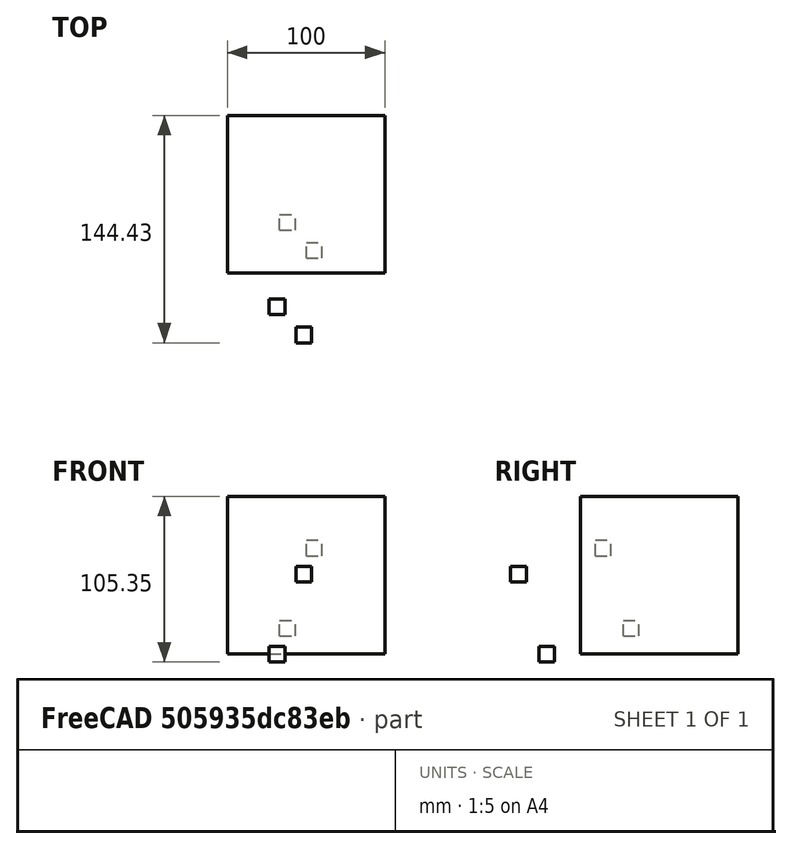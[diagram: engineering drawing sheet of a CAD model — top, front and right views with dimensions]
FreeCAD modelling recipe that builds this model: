
FCSTD DOCUMENT  (FreeCAD 0.20R29603 (Git))
Label: PartArrayPart
License: All rights reserved
LicenseURL: http://en.wikipedia.org/wiki/All_rights_reserved
objects: App::DocumentObjectGroupPython×1251, Part::FeaturePython×3, App::Part×2, Part::Part2DObjectPython×1
note: 4 computed .brp shape members not serialized (recipe doc carries the construction recipe); baked Part::Feature solids carry a one-line shape summary decoded from their .brp

FEATURE [App::DocumentObjectGroupPython] HALFPI  # scripted group (container) (typed FeaturePython)
  name = HALFPI
  value = pi/2.
FEATURE [App::DocumentObjectGroupPython] PI  # scripted group (container) (typed FeaturePython)
  name = PI
  value = 1.*pi
FEATURE [App::DocumentObjectGroupPython] TWOPI  # scripted group (container) (typed FeaturePython)
  name = TWOPI
  value = 2.*pi
FEATURE [App::DocumentObjectGroupPython] Constants  # scripted group (container) (typed FeaturePython)
  Group = -> [HALFPI,PI,TWOPI]
FEATURE [App::DocumentObjectGroupPython] Variables  # scripted group (container) (typed FeaturePython)
FEATURE [App::DocumentObjectGroupPython] Quantities  # scripted group (container) (typed FeaturePython)
FEATURE [App::DocumentObjectGroupPython] Isotopes  # scripted group (container) (typed FeaturePython)
FEATURE [App::DocumentObjectGroupPython] Elements  # scripted group (container) (typed FeaturePython)
FEATURE [App::DocumentObjectGroupPython] Matrix  # scripted group (container) (typed FeaturePython)
FEATURE [App::DocumentObjectGroupPython] Surfaces  # scripted group (container) (typed FeaturePython)
FEATURE [App::DocumentObjectGroupPython] Opticals  # scripted group (container) (typed FeaturePython)
  Group = -> [Matrix,Surfaces]
FEATURE [App::DocumentObjectGroupPython] G4Isotopes  # scripted group (container) (typed FeaturePython)
FEATURE [App::DocumentObjectGroupPython] H_element  # scripted group (container) (typed FeaturePython)
  Z = 1
  atom_value = 1.008
  formula = H
  name = H_element
FEATURE [App::DocumentObjectGroupPython] He_element  # scripted group (container) (typed FeaturePython)
  Z = 2
  atom_value = 4.0026
  formula = He
  name = He_element
FEATURE [App::DocumentObjectGroupPython] Li_element  # scripted group (container) (typed FeaturePython)
  Z = 3
  atom_value = 6.94
  formula = Li
  name = Li_element
FEATURE [App::DocumentObjectGroupPython] Be_element  # scripted group (container) (typed FeaturePython)
  Z = 4
  atom_value = 9.01218
  formula = Be
  name = Be_element
FEATURE [App::DocumentObjectGroupPython] B_element  # scripted group (container) (typed FeaturePython)
  Z = 5
  atom_value = 10.81
  formula = B
  name = B_element
FEATURE [App::DocumentObjectGroupPython] C_element  # scripted group (container) (typed FeaturePython)
  Z = 6
  atom_value = 12.011
  formula = C
  name = C_element
FEATURE [App::DocumentObjectGroupPython] N_element  # scripted group (container) (typed FeaturePython)
  Z = 7
  atom_value = 14.007
  formula = N
  name = N_element
FEATURE [App::DocumentObjectGroupPython] O_element  # scripted group (container) (typed FeaturePython)
  Z = 8
  atom_value = 15.999
  formula = O
  name = O_element
FEATURE [App::DocumentObjectGroupPython] F_element  # scripted group (container) (typed FeaturePython)
  Z = 9
  atom_value = 18.9984
  formula = F
  name = F_element
FEATURE [App::DocumentObjectGroupPython] Ne_element  # scripted group (container) (typed FeaturePython)
  Z = 10
  atom_value = 20.1797
  formula = Ne
  name = Ne_element
FEATURE [App::DocumentObjectGroupPython] Na_element  # scripted group (container) (typed FeaturePython)
  Z = 11
  atom_value = 22.9898
  formula = Na
  name = Na_element
FEATURE [App::DocumentObjectGroupPython] Mg_element  # scripted group (container) (typed FeaturePython)
  Z = 12
  atom_value = 24.305
  formula = Mg
  name = Mg_element
FEATURE [App::DocumentObjectGroupPython] Al_element  # scripted group (container) (typed FeaturePython)
  Z = 13
  atom_value = 26.9815
  formula = Al
  name = Al_element
FEATURE [App::DocumentObjectGroupPython] Si_element  # scripted group (container) (typed FeaturePython)
  Z = 14
  atom_value = 28.085
  formula = Si
  name = Si_element
FEATURE [App::DocumentObjectGroupPython] P_element  # scripted group (container) (typed FeaturePython)
  Z = 15
  atom_value = 30.9738
  formula = P
  name = P_element
FEATURE [App::DocumentObjectGroupPython] S_element  # scripted group (container) (typed FeaturePython)
  Z = 16
  atom_value = 32.06
  formula = S
  name = S_element
FEATURE [App::DocumentObjectGroupPython] Cl_element  # scripted group (container) (typed FeaturePython)
  Z = 17
  atom_value = 35.45
  formula = Cl
  name = Cl_element
FEATURE [App::DocumentObjectGroupPython] Ar_element  # scripted group (container) (typed FeaturePython)
  Z = 18
  atom_value = 39.95
  formula = Ar
  name = Ar_element
FEATURE [App::DocumentObjectGroupPython] K_element  # scripted group (container) (typed FeaturePython)
  Z = 19
  atom_value = 39.0983
  formula = K
  name = K_element
FEATURE [App::DocumentObjectGroupPython] Ca_element  # scripted group (container) (typed FeaturePython)
  Z = 20
  atom_value = 40.078
  formula = Ca
  name = Ca_element
FEATURE [App::DocumentObjectGroupPython] Sc_element  # scripted group (container) (typed FeaturePython)
  Z = 21
  atom_value = 44.9559
  formula = Sc
  name = Sc_element
FEATURE [App::DocumentObjectGroupPython] Ti_element  # scripted group (container) (typed FeaturePython)
  Z = 22
  atom_value = 47.867
  formula = Ti
  name = Ti_element
FEATURE [App::DocumentObjectGroupPython] V_element  # scripted group (container) (typed FeaturePython)
  Z = 23
  atom_value = 50.9415
  formula = V
  name = V_element
FEATURE [App::DocumentObjectGroupPython] Cr_element  # scripted group (container) (typed FeaturePython)
  Z = 24
  atom_value = 51.9961
  formula = Cr
  name = Cr_element
FEATURE [App::DocumentObjectGroupPython] Mn_element  # scripted group (container) (typed FeaturePython)
  Z = 25
  atom_value = 54.938
  formula = Mn
  name = Mn_element
FEATURE [App::DocumentObjectGroupPython] Fe_element  # scripted group (container) (typed FeaturePython)
  Z = 26
  atom_value = 55.845
  formula = Fe
  name = Fe_element
FEATURE [App::DocumentObjectGroupPython] Co_element  # scripted group (container) (typed FeaturePython)
  Z = 27
  atom_value = 58.9332
  formula = Co
  name = Co_element
FEATURE [App::DocumentObjectGroupPython] Ni_element  # scripted group (container) (typed FeaturePython)
  Z = 28
  atom_value = 58.6934
  formula = Ni
  name = Ni_element
FEATURE [App::DocumentObjectGroupPython] Cu_element  # scripted group (container) (typed FeaturePython)
  Z = 29
  atom_value = 63.546
  formula = Cu
  name = Cu_element
FEATURE [App::DocumentObjectGroupPython] Zn_element  # scripted group (container) (typed FeaturePython)
  Z = 30
  atom_value = 65.38
  formula = Zn
  name = Zn_element
FEATURE [App::DocumentObjectGroupPython] Ga_element  # scripted group (container) (typed FeaturePython)
  Z = 31
  atom_value = 69.723
  formula = Ga
  name = Ga_element
FEATURE [App::DocumentObjectGroupPython] Ge_element  # scripted group (container) (typed FeaturePython)
  Z = 32
  atom_value = 72.63
  formula = Ge
  name = Ge_element
FEATURE [App::DocumentObjectGroupPython] As_element  # scripted group (container) (typed FeaturePython)
  Z = 33
  atom_value = 74.9216
  formula = As
  name = As_element
FEATURE [App::DocumentObjectGroupPython] Se_element  # scripted group (container) (typed FeaturePython)
  Z = 34
  atom_value = 78.971
  formula = Se
  name = Se_element
FEATURE [App::DocumentObjectGroupPython] Br_element  # scripted group (container) (typed FeaturePython)
  Z = 35
  atom_value = 79.904
  formula = Br
  name = Br_element
FEATURE [App::DocumentObjectGroupPython] Kr_element  # scripted group (container) (typed FeaturePython)
  Z = 36
  atom_value = 83.798
  formula = Kr
  name = Kr_element
FEATURE [App::DocumentObjectGroupPython] Rb_element  # scripted group (container) (typed FeaturePython)
  Z = 37
  atom_value = 85.4678
  formula = Rb
  name = Rb_element
FEATURE [App::DocumentObjectGroupPython] Sr_element  # scripted group (container) (typed FeaturePython)
  Z = 38
  atom_value = 87.62
  formula = Sr
  name = Sr_element
FEATURE [App::DocumentObjectGroupPython] Y_element  # scripted group (container) (typed FeaturePython)
  Z = 39
  atom_value = 88.9058
  formula = Y
  name = Y_element
FEATURE [App::DocumentObjectGroupPython] Zr_element  # scripted group (container) (typed FeaturePython)
  Z = 40
  atom_value = 91.224
  formula = Zr
  name = Zr_element
FEATURE [App::DocumentObjectGroupPython] Nb_element  # scripted group (container) (typed FeaturePython)
  Z = 41
  atom_value = 92.9064
  formula = Nb
  name = Nb_element
FEATURE [App::DocumentObjectGroupPython] Mo_element  # scripted group (container) (typed FeaturePython)
  Z = 42
  atom_value = 95.95
  formula = Mo
  name = Mo_element
FEATURE [App::DocumentObjectGroupPython] Tc_element  # scripted group (container) (typed FeaturePython)
  Z = 43
  atom_value = 97
  formula = Tc
  name = Tc_element
FEATURE [App::DocumentObjectGroupPython] Ru_element  # scripted group (container) (typed FeaturePython)
  Z = 44
  atom_value = 101.07
  formula = Ru
  name = Ru_element
FEATURE [App::DocumentObjectGroupPython] Rh_element  # scripted group (container) (typed FeaturePython)
  Z = 45
  atom_value = 102.905
  formula = Rh
  name = Rh_element
FEATURE [App::DocumentObjectGroupPython] Pd_element  # scripted group (container) (typed FeaturePython)
  Z = 46
  atom_value = 106.42
  formula = Pd
  name = Pd_element
FEATURE [App::DocumentObjectGroupPython] Ag_element  # scripted group (container) (typed FeaturePython)
  Z = 47
  atom_value = 107.868
  formula = Ag
  name = Ag_element
FEATURE [App::DocumentObjectGroupPython] Cd_element  # scripted group (container) (typed FeaturePython)
  Z = 48
  atom_value = 112.414
  formula = Cd
  name = Cd_element
FEATURE [App::DocumentObjectGroupPython] In_element  # scripted group (container) (typed FeaturePython)
  Z = 49
  atom_value = 114.818
  formula = In
  name = In_element
FEATURE [App::DocumentObjectGroupPython] Sn_element  # scripted group (container) (typed FeaturePython)
  Z = 50
  atom_value = 118.71
  formula = Sn
  name = Sn_element
FEATURE [App::DocumentObjectGroupPython] Sb_element  # scripted group (container) (typed FeaturePython)
  Z = 51
  atom_value = 121.76
  formula = Sb
  name = Sb_element
FEATURE [App::DocumentObjectGroupPython] Te_element  # scripted group (container) (typed FeaturePython)
  Z = 52
  atom_value = 127.6
  formula = Te
  name = Te_element
FEATURE [App::DocumentObjectGroupPython] I_element  # scripted group (container) (typed FeaturePython)
  Z = 53
  atom_value = 126.904
  formula = I
  name = I_element
FEATURE [App::DocumentObjectGroupPython] Xe_element  # scripted group (container) (typed FeaturePython)
  Z = 54
  atom_value = 131.293
  formula = Xe
  name = Xe_element
FEATURE [App::DocumentObjectGroupPython] Cs_element  # scripted group (container) (typed FeaturePython)
  Z = 55
  atom_value = 132.905
  formula = Cs
  name = Cs_element
FEATURE [App::DocumentObjectGroupPython] Ba_element  # scripted group (container) (typed FeaturePython)
  Z = 56
  atom_value = 137.327
  formula = Ba
  name = Ba_element
FEATURE [App::DocumentObjectGroupPython] La_element  # scripted group (container) (typed FeaturePython)
  Z = 57
  atom_value = 138.905
  formula = La
  name = La_element
FEATURE [App::DocumentObjectGroupPython] Ce_element  # scripted group (container) (typed FeaturePython)
  Z = 58
  atom_value = 140.116
  formula = Ce
  name = Ce_element
FEATURE [App::DocumentObjectGroupPython] Pr_element  # scripted group (container) (typed FeaturePython)
  Z = 59
  atom_value = 140.908
  formula = Pr
  name = Pr_element
FEATURE [App::DocumentObjectGroupPython] Nd_element  # scripted group (container) (typed FeaturePython)
  Z = 60
  atom_value = 144.242
  formula = Nd
  name = Nd_element
FEATURE [App::DocumentObjectGroupPython] Pm_element  # scripted group (container) (typed FeaturePython)
  Z = 61
  atom_value = 145
  formula = Pm
  name = Pm_element
FEATURE [App::DocumentObjectGroupPython] Sm_element  # scripted group (container) (typed FeaturePython)
  Z = 62
  atom_value = 150.36
  formula = Sm
  name = Sm_element
FEATURE [App::DocumentObjectGroupPython] Eu_element  # scripted group (container) (typed FeaturePython)
  Z = 63
  atom_value = 151.964
  formula = Eu
  name = Eu_element
FEATURE [App::DocumentObjectGroupPython] Gd_element  # scripted group (container) (typed FeaturePython)
  Z = 64
  atom_value = 157.25
  formula = Gd
  name = Gd_element
FEATURE [App::DocumentObjectGroupPython] Tb_element  # scripted group (container) (typed FeaturePython)
  Z = 65
  atom_value = 158.925
  formula = Tb
  name = Tb_element
FEATURE [App::DocumentObjectGroupPython] Dy_element  # scripted group (container) (typed FeaturePython)
  Z = 66
  atom_value = 162.5
  formula = Dy
  name = Dy_element
FEATURE [App::DocumentObjectGroupPython] Ho_element  # scripted group (container) (typed FeaturePython)
  Z = 67
  atom_value = 164.93
  formula = Ho
  name = Ho_element
FEATURE [App::DocumentObjectGroupPython] Er_element  # scripted group (container) (typed FeaturePython)
  Z = 68
  atom_value = 167.259
  formula = Er
  name = Er_element
FEATURE [App::DocumentObjectGroupPython] Tm_element  # scripted group (container) (typed FeaturePython)
  Z = 69
  atom_value = 168.934
  formula = Tm
  name = Tm_element
FEATURE [App::DocumentObjectGroupPython] Yb_element  # scripted group (container) (typed FeaturePython)
  Z = 70
  atom_value = 173.045
  formula = Yb
  name = Yb_element
FEATURE [App::DocumentObjectGroupPython] Lu_element  # scripted group (container) (typed FeaturePython)
  Z = 71
  atom_value = 174.967
  formula = Lu
  name = Lu_element
FEATURE [App::DocumentObjectGroupPython] Hf_element  # scripted group (container) (typed FeaturePython)
  Z = 72
  atom_value = 178.49
  formula = Hf
  name = Hf_element
FEATURE [App::DocumentObjectGroupPython] Ta_element  # scripted group (container) (typed FeaturePython)
  Z = 73
  atom_value = 180.948
  formula = Ta
  name = Ta_element
FEATURE [App::DocumentObjectGroupPython] W_element  # scripted group (container) (typed FeaturePython)
  Z = 74
  atom_value = 183.84
  formula = W
  name = W_element
FEATURE [App::DocumentObjectGroupPython] Re_element  # scripted group (container) (typed FeaturePython)
  Z = 75
  atom_value = 186.207
  formula = Re
  name = Re_element
FEATURE [App::DocumentObjectGroupPython] Os_element  # scripted group (container) (typed FeaturePython)
  Z = 76
  atom_value = 190.23
  formula = Os
  name = Os_element
FEATURE [App::DocumentObjectGroupPython] Ir_element  # scripted group (container) (typed FeaturePython)
  Z = 77
  atom_value = 192.217
  formula = Ir
  name = Ir_element
FEATURE [App::DocumentObjectGroupPython] Pt_element  # scripted group (container) (typed FeaturePython)
  Z = 78
  atom_value = 195.084
  formula = Pt
  name = Pt_element
FEATURE [App::DocumentObjectGroupPython] Au_element  # scripted group (container) (typed FeaturePython)
  Z = 79
  atom_value = 196.967
  formula = Au
  name = Au_element
FEATURE [App::DocumentObjectGroupPython] Hg_element  # scripted group (container) (typed FeaturePython)
  Z = 80
  atom_value = 200.592
  formula = Hg
  name = Hg_element
FEATURE [App::DocumentObjectGroupPython] Tl_element  # scripted group (container) (typed FeaturePython)
  Z = 81
  atom_value = 204.38
  formula = Tl
  name = Tl_element
FEATURE [App::DocumentObjectGroupPython] Pb_element  # scripted group (container) (typed FeaturePython)
  Z = 82
  atom_value = 207.2
  formula = Pb
  name = Pb_element
FEATURE [App::DocumentObjectGroupPython] Bi_element  # scripted group (container) (typed FeaturePython)
  Z = 83
  atom_value = 208.98
  formula = Bi
  name = Bi_element
FEATURE [App::DocumentObjectGroupPython] Po_element  # scripted group (container) (typed FeaturePython)
  Z = 84
  atom_value = 209
  formula = Po
  name = Po_element
FEATURE [App::DocumentObjectGroupPython] At_element  # scripted group (container) (typed FeaturePython)
  Z = 85
  atom_value = 210
  formula = At
  name = At_element
FEATURE [App::DocumentObjectGroupPython] Rn_element  # scripted group (container) (typed FeaturePython)
  Z = 86
  atom_value = 222
  formula = Rn
  name = Rn_element
FEATURE [App::DocumentObjectGroupPython] Fr_element  # scripted group (container) (typed FeaturePython)
  Z = 87
  atom_value = 223
  formula = Fr
  name = Fr_element
FEATURE [App::DocumentObjectGroupPython] Ra_element  # scripted group (container) (typed FeaturePython)
  Z = 88
  atom_value = 226
  formula = Ra
  name = Ra_element
FEATURE [App::DocumentObjectGroupPython] Ac_element  # scripted group (container) (typed FeaturePython)
  Z = 89
  atom_value = 227
  formula = Ac
  name = Ac_element
FEATURE [App::DocumentObjectGroupPython] Th_element  # scripted group (container) (typed FeaturePython)
  Z = 90
  atom_value = 232.038
  formula = Th
  name = Th_element
FEATURE [App::DocumentObjectGroupPython] Pa_element  # scripted group (container) (typed FeaturePython)
  Z = 91
  atom_value = 231.036
  formula = Pa
  name = Pa_element
FEATURE [App::DocumentObjectGroupPython] U_element  # scripted group (container) (typed FeaturePython)
  Z = 92
  atom_value = 238.029
  formula = U
  name = U_element
FEATURE [App::DocumentObjectGroupPython] Np_element  # scripted group (container) (typed FeaturePython)
  Z = 93
  atom_value = 237
  formula = Np
  name = Np_element
FEATURE [App::DocumentObjectGroupPython] Pu_element  # scripted group (container) (typed FeaturePython)
  Z = 94
  atom_value = 244
  formula = Pu
  name = Pu_element
FEATURE [App::DocumentObjectGroupPython] Am_element  # scripted group (container) (typed FeaturePython)
  Z = 95
  atom_value = 243
  formula = Am
  name = Am_element
FEATURE [App::DocumentObjectGroupPython] Cm_element  # scripted group (container) (typed FeaturePython)
  Z = 96
  atom_value = 247
  formula = Cm
  name = Cm_element
FEATURE [App::DocumentObjectGroupPython] Bk_element  # scripted group (container) (typed FeaturePython)
  Z = 97
  atom_value = 247
  formula = Bk
  name = Bk_element
FEATURE [App::DocumentObjectGroupPython] Cf_element  # scripted group (container) (typed FeaturePython)
  Z = 98
  atom_value = 251
  formula = Cf
  name = Cf_element
FEATURE [App::DocumentObjectGroupPython] G4Elements  # scripted group (container) (typed FeaturePython)
  Group = -> [H_element,He_element,Li_element,Be_element,B_element,C_element,N_element,O_element,F_element,Ne_element,Na_element,Mg_element,Al_element,Si_element,P_element,S_element,Cl_element,Ar_element,K_element,Ca_element,Sc_element,Ti_element,V_element,Cr_element,Mn_element,Fe_element,Co_element,Ni_element,Cu_element,Zn_element,Ga_element,Ge_element,As_element,Se_element,Br_element,Kr_element,Rb_element,+61 more]
FEATURE [App::DocumentObjectGroupPython] H_element001  label="H_element : 0.101"  # scripted group (container) (typed FeaturePython)
  n = 0.101327
FEATURE [App::DocumentObjectGroupPython] C_element001  label="C_element : 0.775"  # scripted group (container) (typed FeaturePython)
  n = 0.7755
FEATURE [App::DocumentObjectGroupPython] N_element001  label="N_element : 0.035"  # scripted group (container) (typed FeaturePython)
  n = 0.035057
FEATURE [App::DocumentObjectGroupPython] O_element001  label="O_element : 0.052"  # scripted group (container) (typed FeaturePython)
  n = 0.0523159
FEATURE [App::DocumentObjectGroupPython] F_element001  label="F_element : 0.017"  # scripted group (container) (typed FeaturePython)
  n = 0.017422
FEATURE [App::DocumentObjectGroupPython] Ca_element001  label="Ca_element : 0.018"  # scripted group (container) (typed FeaturePython)
  n = 0.018378
FEATURE [App::DocumentObjectGroupPython] G4_A_150_TISSUE  label="G4_A-150_TISSUE"  # scripted group (container) (typed FeaturePython)
  Dunit = g/cm3
  Dvalue = 1.127
  Group = -> [H_element001,C_element001,N_element001,O_element001,F_element001,Ca_element001]
  conduct = 2
  density = 1
  expand = 3
  formula = G4_A-150_TISSUE
  name = G4_A-150_TISSUE
  specific = 4
FEATURE [App::DocumentObjectGroupPython] C_element002  label="C_element : 3"  # scripted group (container) (typed FeaturePython)
  n = 3
  ref = C_element
FEATURE [App::DocumentObjectGroupPython] H_element002  label="H_element : 6"  # scripted group (container) (typed FeaturePython)
  n = 6
  ref = H_element
FEATURE [App::DocumentObjectGroupPython] O_element002  label="O_element : 1"  # scripted group (container) (typed FeaturePython)
  n = 1
  ref = O_element
FEATURE [App::DocumentObjectGroupPython] G4_ACETONE  # scripted group (container) (typed FeaturePython)
  Dunit = g/cm3
  Dvalue = 0.7899
  Group = -> [C_element002,H_element002,O_element002]
  conduct = 2
  density = 1
  expand = 3
  formula = G4_ACETONE
  name = G4_ACETONE
  specific = 4
FEATURE [App::DocumentObjectGroupPython] C_element003  label="C_element : 2"  # scripted group (container) (typed FeaturePython)
  n = 2
  ref = C_element
FEATURE [App::DocumentObjectGroupPython] H_element003  label="H_element : 2"  # scripted group (container) (typed FeaturePython)
  n = 2
  ref = H_element
FEATURE [App::DocumentObjectGroupPython] G4_ACETYLENE  # scripted group (container) (typed FeaturePython)
  Dunit = g/cm3
  Dvalue = 0.0010967
  Group = -> [C_element003,H_element003]
  conduct = 2
  density = 1
  expand = 3
  formula = G4_ACETYLENE
  name = G4_ACETYLENE
  specific = 4
FEATURE [App::DocumentObjectGroupPython] C_element004  label="C_element : 5"  # scripted group (container) (typed FeaturePython)
  n = 5
  ref = C_element
FEATURE [App::DocumentObjectGroupPython] H_element004  label="H_element : 5"  # scripted group (container) (typed FeaturePython)
  n = 5
  ref = H_element
FEATURE [App::DocumentObjectGroupPython] N_element002  label="N_element : 5"  # scripted group (container) (typed FeaturePython)
  n = 5
  ref = N_element
FEATURE [App::DocumentObjectGroupPython] G4_ADENINE  # scripted group (container) (typed FeaturePython)
  Dunit = g/cm3
  Dvalue = 1.6
  Group = -> [C_element004,H_element004,N_element002]
  conduct = 2
  density = 1
  expand = 3
  formula = G4_ADENINE
  name = G4_ADENINE
  specific = 4
FEATURE [App::DocumentObjectGroupPython] H_element005  label="H_element : 0.114"  # scripted group (container) (typed FeaturePython)
  n = 0.114
FEATURE [App::DocumentObjectGroupPython] C_element005  label="C_element : 0.598"  # scripted group (container) (typed FeaturePython)
  n = 0.598
FEATURE [App::DocumentObjectGroupPython] N_element003  label="N_element : 0.007"  # scripted group (container) (typed FeaturePython)
  n = 0.007
FEATURE [App::DocumentObjectGroupPython] O_element003  label="O_element : 0.278"  # scripted group (container) (typed FeaturePython)
  n = 0.278
FEATURE [App::DocumentObjectGroupPython] Na_element001  label="Na_element : 0.001"  # scripted group (container) (typed FeaturePython)
  n = 0.001
FEATURE [App::DocumentObjectGroupPython] S_element001  label="S_element : 0.001"  # scripted group (container) (typed FeaturePython)
  n = 0.001
FEATURE [App::DocumentObjectGroupPython] Cl_element001  label="Cl_element : 0.001"  # scripted group (container) (typed FeaturePython)
  n = 0.001
FEATURE [App::DocumentObjectGroupPython] G4_ADIPOSE_TISSUE_ICRP  # scripted group (container) (typed FeaturePython)
  Dunit = g/cm3
  Dvalue = 0.95
  Group = -> [H_element005,C_element005,N_element003,O_element003,Na_element001,S_element001,Cl_element001]
  conduct = 2
  density = 1
  expand = 3
  formula = G4_ADIPOSE_TISSUE_ICRP
  name = G4_ADIPOSE_TISSUE_ICRP
  specific = 4
FEATURE [App::DocumentObjectGroupPython] C_element006  label="C_element : 0.000"  # scripted group (container) (typed FeaturePython)
  n = 0.000124
FEATURE [App::DocumentObjectGroupPython] N_element004  label="N_element : 0.755"  # scripted group (container) (typed FeaturePython)
  n = 0.755268
FEATURE [App::DocumentObjectGroupPython] O_element004  label="O_element : 0.232"  # scripted group (container) (typed FeaturePython)
  n = 0.231781
FEATURE [App::DocumentObjectGroupPython] Ar_element001  label="Ar_element : 0.013"  # scripted group (container) (typed FeaturePython)
  n = 0.012827
FEATURE [App::DocumentObjectGroupPython] G4_AIR  # scripted group (container) (typed FeaturePython)
  Dunit = g/cm3
  Dvalue = 0.00120479
  Group = -> [C_element006,N_element004,O_element004,Ar_element001]
  conduct = 2
  density = 1
  expand = 3
  formula = G4_AIR
  name = G4_AIR
  specific = 4
FEATURE [App::DocumentObjectGroupPython] C_element007  label="C_element : 006"  # scripted group (container) (typed FeaturePython)
  n = 3
  ref = C_element
FEATURE [App::DocumentObjectGroupPython] H_element006  label="H_element : 7"  # scripted group (container) (typed FeaturePython)
  n = 7
  ref = H_element
FEATURE [App::DocumentObjectGroupPython] N_element005  label="N_element : 1"  # scripted group (container) (typed FeaturePython)
  n = 1
  ref = N_element
FEATURE [App::DocumentObjectGroupPython] O_element005  label="O_element : 2"  # scripted group (container) (typed FeaturePython)
  n = 2
  ref = O_element
FEATURE [App::DocumentObjectGroupPython] G4_ALANINE  # scripted group (container) (typed FeaturePython)
  Dunit = g/cm3
  Dvalue = 1.42
  Group = -> [C_element007,H_element006,N_element005,O_element005]
  conduct = 2
  density = 1
  expand = 3
  formula = G4_ALANINE
  name = G4_ALANINE
  specific = 4
FEATURE [App::DocumentObjectGroupPython] Al_element001  label="Al_element : 2"  # scripted group (container) (typed FeaturePython)
  n = 2
  ref = Al_element
FEATURE [App::DocumentObjectGroupPython] O_element006  label="O_element : 3"  # scripted group (container) (typed FeaturePython)
  n = 3
  ref = O_element
FEATURE [App::DocumentObjectGroupPython] G4_ALUMINUM_OXIDE  # scripted group (container) (typed FeaturePython)
  Dunit = g/cm3
  Dvalue = 3.97
  Group = -> [Al_element001,O_element006]
  conduct = 2
  density = 1
  expand = 3
  formula = G4_ALUMINUM_OXIDE
  name = G4_ALUMINUM_OXIDE
  specific = 4
FEATURE [App::DocumentObjectGroupPython] H_element007  label="H_element : 0.106"  # scripted group (container) (typed FeaturePython)
  n = 0.10593
FEATURE [App::DocumentObjectGroupPython] C_element008  label="C_element : 0.789"  # scripted group (container) (typed FeaturePython)
  n = 0.788974
FEATURE [App::DocumentObjectGroupPython] O_element007  label="O_element : 0.105"  # scripted group (container) (typed FeaturePython)
  n = 0.105096
FEATURE [App::DocumentObjectGroupPython] G4_AMBER  # scripted group (container) (typed FeaturePython)
  Dunit = g/cm3
  Dvalue = 1.1
  Group = -> [H_element007,C_element008,O_element007]
  conduct = 2
  density = 1
  expand = 3
  formula = G4_AMBER
  name = G4_AMBER
  specific = 4
FEATURE [App::DocumentObjectGroupPython] N_element006  label="N_element : 006"  # scripted group (container) (typed FeaturePython)
  n = 1
  ref = N_element
FEATURE [App::DocumentObjectGroupPython] H_element008  label="H_element : 3"  # scripted group (container) (typed FeaturePython)
  n = 3
  ref = H_element
FEATURE [App::DocumentObjectGroupPython] G4_AMMONIA  # scripted group (container) (typed FeaturePython)
  Dunit = g/cm3
  Dvalue = 0.000826019
  Group = -> [N_element006,H_element008]
  conduct = 2
  density = 1
  expand = 3
  formula = G4_AMMONIA
  name = G4_AMMONIA
  specific = 4
FEATURE [App::DocumentObjectGroupPython] C_element009  label="C_element : 6"  # scripted group (container) (typed FeaturePython)
  n = 6
  ref = C_element
FEATURE [App::DocumentObjectGroupPython] H_element009  label="H_element : 008"  # scripted group (container) (typed FeaturePython)
  n = 7
  ref = H_element
FEATURE [App::DocumentObjectGroupPython] N_element007  label="N_element : 007"  # scripted group (container) (typed FeaturePython)
  n = 1
  ref = N_element
FEATURE [App::DocumentObjectGroupPython] G4_ANILINE  # scripted group (container) (typed FeaturePython)
  Dunit = g/cm3
  Dvalue = 1.0235
  Group = -> [C_element009,H_element009,N_element007]
  conduct = 2
  density = 1
  expand = 3
  formula = G4_ANILINE
  name = G4_ANILINE
  specific = 4
FEATURE [App::DocumentObjectGroupPython] C_element010  label="C_element : 14"  # scripted group (container) (typed FeaturePython)
  n = 14
  ref = C_element
FEATURE [App::DocumentObjectGroupPython] H_element010  label="H_element : 10"  # scripted group (container) (typed FeaturePython)
  n = 10
  ref = H_element
FEATURE [App::DocumentObjectGroupPython] G4_ANTHRACENE  # scripted group (container) (typed FeaturePython)
  Dunit = g/cm3
  Dvalue = 1.283
  Group = -> [C_element010,H_element010]
  conduct = 2
  density = 1
  expand = 3
  formula = G4_ANTHRACENE
  name = G4_ANTHRACENE
  specific = 4
FEATURE [App::DocumentObjectGroupPython] H_element011  label="H_element : 0.065"  # scripted group (container) (typed FeaturePython)
  n = 0.0654709
FEATURE [App::DocumentObjectGroupPython] C_element011  label="C_element : 0.537"  # scripted group (container) (typed FeaturePython)
  n = 0.536944
FEATURE [App::DocumentObjectGroupPython] N_element008  label="N_element : 0.021"  # scripted group (container) (typed FeaturePython)
  n = 0.0215
FEATURE [App::DocumentObjectGroupPython] O_element008  label="O_element : 0.032"  # scripted group (container) (typed FeaturePython)
  n = 0.032085
FEATURE [App::DocumentObjectGroupPython] F_element002  label="F_element : 0.167"  # scripted group (container) (typed FeaturePython)
  n = 0.167411
FEATURE [App::DocumentObjectGroupPython] Ca_element002  label="Ca_element : 0.177"  # scripted group (container) (typed FeaturePython)
  n = 0.176589
FEATURE [App::DocumentObjectGroupPython] G4_B_100_BONE  label="G4_B-100_BONE"  # scripted group (container) (typed FeaturePython)
  Dunit = g/cm3
  Dvalue = 1.45
  Group = -> [H_element011,C_element011,N_element008,O_element008,F_element002,Ca_element002]
  conduct = 2
  density = 1
  expand = 3
  formula = G4_B-100_BONE
  name = G4_B-100_BONE
  specific = 4
FEATURE [App::DocumentObjectGroupPython] H_element012  label="H_element : 0.057"  # scripted group (container) (typed FeaturePython)
  n = 0.057441
FEATURE [App::DocumentObjectGroupPython] C_element012  label="C_element : 0.790"  # scripted group (container) (typed FeaturePython)
  n = 0.774591
FEATURE [App::DocumentObjectGroupPython] O_element009  label="O_element : 0.168"  # scripted group (container) (typed FeaturePython)
  n = 0.167968
FEATURE [App::DocumentObjectGroupPython] G4_BAKELITE  # scripted group (container) (typed FeaturePython)
  Dunit = g/cm3
  Dvalue = 1.25
  Group = -> [H_element012,C_element012,O_element009]
  conduct = 2
  density = 1
  expand = 3
  formula = G4_BAKELITE
  name = G4_BAKELITE
  specific = 4
FEATURE [App::DocumentObjectGroupPython] Ba_element001  label="Ba_element : 1"  # scripted group (container) (typed FeaturePython)
  n = 1
  ref = Ba_element
FEATURE [App::DocumentObjectGroupPython] F_element003  label="F_element : 2"  # scripted group (container) (typed FeaturePython)
  n = 2
  ref = F_element
FEATURE [App::DocumentObjectGroupPython] G4_BARIUM_FLUORIDE  # scripted group (container) (typed FeaturePython)
  Dunit = g/cm3
  Dvalue = 4.89
  Group = -> [Ba_element001,F_element003]
  conduct = 2
  density = 1
  expand = 3
  formula = G4_BARIUM_FLUORIDE
  name = G4_BARIUM_FLUORIDE
  specific = 4
FEATURE [App::DocumentObjectGroupPython] Ba_element002  label="Ba_element : 002"  # scripted group (container) (typed FeaturePython)
  n = 1
  ref = Ba_element
FEATURE [App::DocumentObjectGroupPython] S_element002  label="S_element : 1"  # scripted group (container) (typed FeaturePython)
  n = 1
  ref = S_element
FEATURE [App::DocumentObjectGroupPython] O_element010  label="O_element : 4"  # scripted group (container) (typed FeaturePython)
  n = 4
  ref = O_element
FEATURE [App::DocumentObjectGroupPython] G4_BARIUM_SULFATE  # scripted group (container) (typed FeaturePython)
  Dunit = g/cm3
  Dvalue = 4.5
  Group = -> [Ba_element002,S_element002,O_element010]
  conduct = 2
  density = 1
  expand = 3
  formula = G4_BARIUM_SULFATE
  name = G4_BARIUM_SULFATE
  specific = 4
FEATURE [App::DocumentObjectGroupPython] C_element013  label="C_element : 007"  # scripted group (container) (typed FeaturePython)
  n = 6
  ref = C_element
FEATURE [App::DocumentObjectGroupPython] H_element013  label="H_element : 009"  # scripted group (container) (typed FeaturePython)
  n = 6
  ref = H_element
FEATURE [App::DocumentObjectGroupPython] G4_BENZENE  # scripted group (container) (typed FeaturePython)
  Dunit = g/cm3
  Dvalue = 0.87865
  Group = -> [C_element013,H_element013]
  conduct = 2
  density = 1
  expand = 3
  formula = G4_BENZENE
  name = G4_BENZENE
  specific = 4
FEATURE [App::DocumentObjectGroupPython] Be_element001  label="Be_element : 1"  # scripted group (container) (typed FeaturePython)
  n = 1
  ref = Be_element
FEATURE [App::DocumentObjectGroupPython] O_element011  label="O_element : 005"  # scripted group (container) (typed FeaturePython)
  n = 1
  ref = O_element
FEATURE [App::DocumentObjectGroupPython] G4_BERYLLIUM_OXIDE  # scripted group (container) (typed FeaturePython)
  Dunit = g/cm3
  Dvalue = 3.01
  Group = -> [Be_element001,O_element011]
  conduct = 2
  density = 1
  expand = 3
  formula = G4_BERYLLIUM_OXIDE
  name = G4_BERYLLIUM_OXIDE
  specific = 4
FEATURE [App::DocumentObjectGroupPython] Bi_element001  label="Bi_element : 4"  # scripted group (container) (typed FeaturePython)
  n = 4
  ref = Bi_element
FEATURE [App::DocumentObjectGroupPython] Ge_element001  label="Ge_element : 3"  # scripted group (container) (typed FeaturePython)
  n = 3
  ref = Ge_element
FEATURE [App::DocumentObjectGroupPython] O_element012  label="O_element : 12"  # scripted group (container) (typed FeaturePython)
  n = 12
  ref = O_element
FEATURE [App::DocumentObjectGroupPython] G4_BGO  # scripted group (container) (typed FeaturePython)
  Dunit = g/cm3
  Dvalue = 7.13
  Group = -> [Bi_element001,Ge_element001,O_element012]
  conduct = 2
  density = 1
  expand = 3
  formula = G4_BGO
  name = G4_BGO
  specific = 4
FEATURE [App::DocumentObjectGroupPython] H_element014  label="H_element : 0.102"  # scripted group (container) (typed FeaturePython)
  n = 0.102
FEATURE [App::DocumentObjectGroupPython] C_element014  label="C_element : 0.110"  # scripted group (container) (typed FeaturePython)
  n = 0.11
FEATURE [App::DocumentObjectGroupPython] N_element009  label="N_element : 0.033"  # scripted group (container) (typed FeaturePython)
  n = 0.033
FEATURE [App::DocumentObjectGroupPython] O_element013  label="O_element : 0.745"  # scripted group (container) (typed FeaturePython)
  n = 0.745
FEATURE [App::DocumentObjectGroupPython] Na_element002  label="Na_element : 0.002"  # scripted group (container) (typed FeaturePython)
  n = 0.001
FEATURE [App::DocumentObjectGroupPython] P_element001  label="P_element : 0.001"  # scripted group (container) (typed FeaturePython)
  n = 0.001
FEATURE [App::DocumentObjectGroupPython] S_element003  label="S_element : 0.002"  # scripted group (container) (typed FeaturePython)
  n = 0.002
FEATURE [App::DocumentObjectGroupPython] Cl_element002  label="Cl_element : 0.003"  # scripted group (container) (typed FeaturePython)
  n = 0.003
FEATURE [App::DocumentObjectGroupPython] K_element001  label="K_element : 0.002"  # scripted group (container) (typed FeaturePython)
  n = 0.002
FEATURE [App::DocumentObjectGroupPython] Fe_element001  label="Fe_element : 0.001"  # scripted group (container) (typed FeaturePython)
  n = 0.001
FEATURE [App::DocumentObjectGroupPython] G4_BLOOD_ICRP  # scripted group (container) (typed FeaturePython)
  Dunit = g/cm3
  Dvalue = 1.06
  Group = -> [H_element014,C_element014,N_element009,O_element013,Na_element002,P_element001,S_element003,Cl_element002,K_element001,Fe_element001]
  conduct = 2
  density = 1
  expand = 3
  formula = G4_BLOOD_ICRP
  name = G4_BLOOD_ICRP
  specific = 4
FEATURE [App::DocumentObjectGroupPython] H_element015  label="H_element : 0.064"  # scripted group (container) (typed FeaturePython)
  n = 0.064
FEATURE [App::DocumentObjectGroupPython] C_element015  label="C_element : 0.278"  # scripted group (container) (typed FeaturePython)
  n = 0.278
FEATURE [App::DocumentObjectGroupPython] N_element010  label="N_element : 0.027"  # scripted group (container) (typed FeaturePython)
  n = 0.027
FEATURE [App::DocumentObjectGroupPython] O_element014  label="O_element : 0.410"  # scripted group (container) (typed FeaturePython)
  n = 0.41
FEATURE [App::DocumentObjectGroupPython] Mg_element001  label="Mg_element : 0.002"  # scripted group (container) (typed FeaturePython)
  n = 0.002
FEATURE [App::DocumentObjectGroupPython] P_element002  label="P_element : 0.070"  # scripted group (container) (typed FeaturePython)
  n = 0.07
FEATURE [App::DocumentObjectGroupPython] S_element004  label="S_element : 0.003"  # scripted group (container) (typed FeaturePython)
  n = 0.002
FEATURE [App::DocumentObjectGroupPython] Ca_element003  label="Ca_element : 0.147"  # scripted group (container) (typed FeaturePython)
  n = 0.147
FEATURE [App::DocumentObjectGroupPython] G4_BONE_COMPACT_ICRU  # scripted group (container) (typed FeaturePython)
  Dunit = g/cm3
  Dvalue = 1.85
  Group = -> [H_element015,C_element015,N_element010,O_element014,Mg_element001,P_element002,S_element004,Ca_element003]
  conduct = 2
  density = 1
  expand = 3
  formula = G4_BONE_COMPACT_ICRU
  name = G4_BONE_COMPACT_ICRU
  specific = 4
FEATURE [App::DocumentObjectGroupPython] H_element016  label="H_element : 0.034"  # scripted group (container) (typed FeaturePython)
  n = 0.034
FEATURE [App::DocumentObjectGroupPython] C_element016  label="C_element : 0.155"  # scripted group (container) (typed FeaturePython)
  n = 0.155
FEATURE [App::DocumentObjectGroupPython] N_element011  label="N_element : 0.042"  # scripted group (container) (typed FeaturePython)
  n = 0.042
FEATURE [App::DocumentObjectGroupPython] O_element015  label="O_element : 0.435"  # scripted group (container) (typed FeaturePython)
  n = 0.435
FEATURE [App::DocumentObjectGroupPython] Na_element003  label="Na_element : 0.003"  # scripted group (container) (typed FeaturePython)
  n = 0.001
FEATURE [App::DocumentObjectGroupPython] Mg_element002  label="Mg_element : 0.003"  # scripted group (container) (typed FeaturePython)
  n = 0.002
FEATURE [App::DocumentObjectGroupPython] P_element003  label="P_element : 0.103"  # scripted group (container) (typed FeaturePython)
  n = 0.103
FEATURE [App::DocumentObjectGroupPython] S_element005  label="S_element : 0.004"  # scripted group (container) (typed FeaturePython)
  n = 0.003
FEATURE [App::DocumentObjectGroupPython] Ca_element004  label="Ca_element : 0.225"  # scripted group (container) (typed FeaturePython)
  n = 0.225
FEATURE [App::DocumentObjectGroupPython] G4_BONE_CORTICAL_ICRP  # scripted group (container) (typed FeaturePython)
  Dunit = g/cm3
  Dvalue = 1.92
  Group = -> [H_element016,C_element016,N_element011,O_element015,Na_element003,Mg_element002,P_element003,S_element005,Ca_element004]
  conduct = 2
  density = 1
  expand = 3
  formula = G4_BONE_CORTICAL_ICRP
  name = G4_BONE_CORTICAL_ICRP
  specific = 4
FEATURE [App::DocumentObjectGroupPython] B_element001  label="B_element : 4"  # scripted group (container) (typed FeaturePython)
  n = 4
  ref = B_element
FEATURE [App::DocumentObjectGroupPython] C_element017  label="C_element : 1"  # scripted group (container) (typed FeaturePython)
  n = 1
  ref = C_element
FEATURE [App::DocumentObjectGroupPython] G4_BORON_CARBIDE  # scripted group (container) (typed FeaturePython)
  Dunit = g/cm3
  Dvalue = 2.52
  Group = -> [B_element001,C_element017]
  conduct = 2
  density = 1
  expand = 3
  formula = G4_BORON_CARBIDE
  name = G4_BORON_CARBIDE
  specific = 4
FEATURE [App::DocumentObjectGroupPython] B_element002  label="B_element : 2"  # scripted group (container) (typed FeaturePython)
  n = 2
  ref = B_element
FEATURE [App::DocumentObjectGroupPython] O_element016  label="O_element : 006"  # scripted group (container) (typed FeaturePython)
  n = 3
  ref = O_element
FEATURE [App::DocumentObjectGroupPython] G4_BORON_OXIDE  # scripted group (container) (typed FeaturePython)
  Dunit = g/cm3
  Dvalue = 1.812
  Group = -> [B_element002,O_element016]
  conduct = 2
  density = 1
  expand = 3
  formula = G4_BORON_OXIDE
  name = G4_BORON_OXIDE
  specific = 4
FEATURE [App::DocumentObjectGroupPython] H_element017  label="H_element : 0.107"  # scripted group (container) (typed FeaturePython)
  n = 0.107
FEATURE [App::DocumentObjectGroupPython] C_element018  label="C_element : 0.145"  # scripted group (container) (typed FeaturePython)
  n = 0.145
FEATURE [App::DocumentObjectGroupPython] N_element012  label="N_element : 0.022"  # scripted group (container) (typed FeaturePython)
  n = 0.022
FEATURE [App::DocumentObjectGroupPython] O_element017  label="O_element : 0.712"  # scripted group (container) (typed FeaturePython)
  n = 0.712
FEATURE [App::DocumentObjectGroupPython] Na_element004  label="Na_element : 0.004"  # scripted group (container) (typed FeaturePython)
  n = 0.002
FEATURE [App::DocumentObjectGroupPython] P_element004  label="P_element : 0.004"  # scripted group (container) (typed FeaturePython)
  n = 0.004
FEATURE [App::DocumentObjectGroupPython] S_element006  label="S_element : 0.005"  # scripted group (container) (typed FeaturePython)
  n = 0.002
FEATURE [App::DocumentObjectGroupPython] Cl_element003  label="Cl_element : 0.004"  # scripted group (container) (typed FeaturePython)
  n = 0.003
FEATURE [App::DocumentObjectGroupPython] K_element002  label="K_element : 0.003"  # scripted group (container) (typed FeaturePython)
  n = 0.003
FEATURE [App::DocumentObjectGroupPython] G4_BRAIN_ICRP  # scripted group (container) (typed FeaturePython)
  Dunit = g/cm3
  Dvalue = 1.04
  Group = -> [H_element017,C_element018,N_element012,O_element017,Na_element004,P_element004,S_element006,Cl_element003,K_element002]
  conduct = 2
  density = 1
  expand = 3
  formula = G4_BRAIN_ICRP
  name = G4_BRAIN_ICRP
  specific = 4
FEATURE [App::DocumentObjectGroupPython] C_element019  label="C_element : 4"  # scripted group (container) (typed FeaturePython)
  n = 4
  ref = C_element
FEATURE [App::DocumentObjectGroupPython] H_element018  label="H_element : 010"  # scripted group (container) (typed FeaturePython)
  n = 10
  ref = H_element
FEATURE [App::DocumentObjectGroupPython] G4_BUTANE  # scripted group (container) (typed FeaturePython)
  Dunit = g/cm3
  Dvalue = 0.00249343
  Group = -> [C_element019,H_element018]
  conduct = 2
  density = 1
  expand = 3
  formula = G4_BUTANE
  name = G4_BUTANE
  specific = 4
FEATURE [App::DocumentObjectGroupPython] C_element020  label="C_element : 008"  # scripted group (container) (typed FeaturePython)
  n = 4
  ref = C_element
FEATURE [App::DocumentObjectGroupPython] H_element019  label="H_element : 011"  # scripted group (container) (typed FeaturePython)
  n = 10
  ref = H_element
FEATURE [App::DocumentObjectGroupPython] O_element018  label="O_element : 007"  # scripted group (container) (typed FeaturePython)
  n = 1
  ref = O_element
FEATURE [App::DocumentObjectGroupPython] G4_N_BUTYL_ALCOHOL  label="G4_N-BUTYL_ALCOHOL"  # scripted group (container) (typed FeaturePython)
  Dunit = g/cm3
  Dvalue = 0.8098
  Group = -> [C_element020,H_element019,O_element018]
  conduct = 2
  density = 1
  expand = 3
  formula = G4_N-BUTYL_ALCOHOL
  name = G4_N-BUTYL_ALCOHOL
  specific = 4
FEATURE [App::DocumentObjectGroupPython] H_element020  label="H_element : 0.025"  # scripted group (container) (typed FeaturePython)
  n = 0.02468
FEATURE [App::DocumentObjectGroupPython] C_element021  label="C_element : 0.502"  # scripted group (container) (typed FeaturePython)
  n = 0.501611
FEATURE [App::DocumentObjectGroupPython] O_element019  label="O_element : 0.005"  # scripted group (container) (typed FeaturePython)
  n = 0.004527
FEATURE [App::DocumentObjectGroupPython] F_element004  label="F_element : 0.465"  # scripted group (container) (typed FeaturePython)
  n = 0.465209
FEATURE [App::DocumentObjectGroupPython] Si_element001  label="Si_element : 0.004"  # scripted group (container) (typed FeaturePython)
  n = 0.003973
FEATURE [App::DocumentObjectGroupPython] G4_C_552  label="G4_C-552"  # scripted group (container) (typed FeaturePython)
  Dunit = g/cm3
  Dvalue = 1.76
  Group = -> [H_element020,C_element021,O_element019,F_element004,Si_element001]
  conduct = 2
  density = 1
  expand = 3
  formula = G4_C-552
  name = G4_C-552
  specific = 4
FEATURE [App::DocumentObjectGroupPython] Cd_element001  label="Cd_element : 1"  # scripted group (container) (typed FeaturePython)
  n = 1
  ref = Cd_element
FEATURE [App::DocumentObjectGroupPython] Te_element001  label="Te_element : 1"  # scripted group (container) (typed FeaturePython)
  n = 1
  ref = Te_element
FEATURE [App::DocumentObjectGroupPython] G4_CADMIUM_TELLURIDE  # scripted group (container) (typed FeaturePython)
  Dunit = g/cm3
  Dvalue = 6.2
  Group = -> [Cd_element001,Te_element001]
  conduct = 2
  density = 1
  expand = 3
  formula = G4_CADMIUM_TELLURIDE
  name = G4_CADMIUM_TELLURIDE
  specific = 4
FEATURE [App::DocumentObjectGroupPython] Cd_element002  label="Cd_element : 002"  # scripted group (container) (typed FeaturePython)
  n = 1
  ref = Cd_element
FEATURE [App::DocumentObjectGroupPython] W_element001  label="W_element : 1"  # scripted group (container) (typed FeaturePython)
  n = 1
  ref = W_element
FEATURE [App::DocumentObjectGroupPython] O_element020  label="O_element : 008"  # scripted group (container) (typed FeaturePython)
  n = 4
  ref = O_element
FEATURE [App::DocumentObjectGroupPython] G4_CADMIUM_TUNGSTATE  # scripted group (container) (typed FeaturePython)
  Dunit = g/cm3
  Dvalue = 7.9
  Group = -> [Cd_element002,W_element001,O_element020]
  conduct = 2
  density = 1
  expand = 3
  formula = G4_CADMIUM_TUNGSTATE
  name = G4_CADMIUM_TUNGSTATE
  specific = 4
FEATURE [App::DocumentObjectGroupPython] Ca_element005  label="Ca_element : 1"  # scripted group (container) (typed FeaturePython)
  n = 1
  ref = Ca_element
FEATURE [App::DocumentObjectGroupPython] C_element022  label="C_element : 009"  # scripted group (container) (typed FeaturePython)
  n = 1
  ref = C_element
FEATURE [App::DocumentObjectGroupPython] O_element021  label="O_element : 009"  # scripted group (container) (typed FeaturePython)
  n = 3
  ref = O_element
FEATURE [App::DocumentObjectGroupPython] G4_CALCIUM_CARBONATE  # scripted group (container) (typed FeaturePython)
  Dunit = g/cm3
  Dvalue = 2.8
  Group = -> [Ca_element005,C_element022,O_element021]
  conduct = 2
  density = 1
  expand = 3
  formula = G4_CALCIUM_CARBONATE
  name = G4_CALCIUM_CARBONATE
  specific = 4
FEATURE [App::DocumentObjectGroupPython] Ca_element006  label="Ca_element : 002"  # scripted group (container) (typed FeaturePython)
  n = 1
  ref = Ca_element
FEATURE [App::DocumentObjectGroupPython] F_element005  label="F_element : 003"  # scripted group (container) (typed FeaturePython)
  n = 2
  ref = F_element
FEATURE [App::DocumentObjectGroupPython] G4_CALCIUM_FLUORIDE  # scripted group (container) (typed FeaturePython)
  Dunit = g/cm3
  Dvalue = 3.18
  Group = -> [Ca_element006,F_element005]
  conduct = 2
  density = 1
  expand = 3
  formula = G4_CALCIUM_FLUORIDE
  name = G4_CALCIUM_FLUORIDE
  specific = 4
FEATURE [App::DocumentObjectGroupPython] Ca_element007  label="Ca_element : 003"  # scripted group (container) (typed FeaturePython)
  n = 1
  ref = Ca_element
FEATURE [App::DocumentObjectGroupPython] O_element022  label="O_element : 010"  # scripted group (container) (typed FeaturePython)
  n = 1
  ref = O_element
FEATURE [App::DocumentObjectGroupPython] G4_CALCIUM_OXIDE  # scripted group (container) (typed FeaturePython)
  Dunit = g/cm3
  Dvalue = 3.3
  Group = -> [Ca_element007,O_element022]
  conduct = 2
  density = 1
  expand = 3
  formula = G4_CALCIUM_OXIDE
  name = G4_CALCIUM_OXIDE
  specific = 4
FEATURE [App::DocumentObjectGroupPython] Ca_element008  label="Ca_element : 004"  # scripted group (container) (typed FeaturePython)
  n = 1
  ref = Ca_element
FEATURE [App::DocumentObjectGroupPython] S_element007  label="S_element : 002"  # scripted group (container) (typed FeaturePython)
  n = 1
  ref = S_element
FEATURE [App::DocumentObjectGroupPython] O_element023  label="O_element : 011"  # scripted group (container) (typed FeaturePython)
  n = 4
  ref = O_element
FEATURE [App::DocumentObjectGroupPython] G4_CALCIUM_SULFATE  # scripted group (container) (typed FeaturePython)
  Dunit = g/cm3
  Dvalue = 2.96
  Group = -> [Ca_element008,S_element007,O_element023]
  conduct = 2
  density = 1
  expand = 3
  formula = G4_CALCIUM_SULFATE
  name = G4_CALCIUM_SULFATE
  specific = 4
FEATURE [App::DocumentObjectGroupPython] Ca_element009  label="Ca_element : 005"  # scripted group (container) (typed FeaturePython)
  n = 1
  ref = Ca_element
FEATURE [App::DocumentObjectGroupPython] W_element002  label="W_element : 002"  # scripted group (container) (typed FeaturePython)
  n = 1
  ref = W_element
FEATURE [App::DocumentObjectGroupPython] O_element024  label="O_element : 012"  # scripted group (container) (typed FeaturePython)
  n = 4
  ref = O_element
FEATURE [App::DocumentObjectGroupPython] G4_CALCIUM_TUNGSTATE  # scripted group (container) (typed FeaturePython)
  Dunit = g/cm3
  Dvalue = 6.062
  Group = -> [Ca_element009,W_element002,O_element024]
  conduct = 2
  density = 1
  expand = 3
  formula = G4_CALCIUM_TUNGSTATE
  name = G4_CALCIUM_TUNGSTATE
  specific = 4
FEATURE [App::DocumentObjectGroupPython] C_element023  label="C_element : 010"  # scripted group (container) (typed FeaturePython)
  n = 1
  ref = C_element
FEATURE [App::DocumentObjectGroupPython] O_element025  label="O_element : 013"  # scripted group (container) (typed FeaturePython)
  n = 2
  ref = O_element
FEATURE [App::DocumentObjectGroupPython] G4_CARBON_DIOXIDE  # scripted group (container) (typed FeaturePython)
  Dunit = g/cm3
  Dvalue = 0.00184212
  Group = -> [C_element023,O_element025]
  conduct = 2
  density = 1
  expand = 3
  formula = G4_CARBON_DIOXIDE
  name = G4_CARBON_DIOXIDE
  specific = 4
FEATURE [App::DocumentObjectGroupPython] C_element024  label="C_element : 011"  # scripted group (container) (typed FeaturePython)
  n = 1
  ref = C_element
FEATURE [App::DocumentObjectGroupPython] Cl_element004  label="Cl_element : 4"  # scripted group (container) (typed FeaturePython)
  n = 4
  ref = Cl_element
FEATURE [App::DocumentObjectGroupPython] G4_CARBON_TETRACHLORIDE  # scripted group (container) (typed FeaturePython)
  Dunit = g/cm3
  Dvalue = 1.594
  Group = -> [C_element024,Cl_element004]
  conduct = 2
  density = 1
  expand = 3
  formula = G4_CARBON_TETRACHLORIDE
  name = G4_CARBON_TETRACHLORIDE
  specific = 4
FEATURE [App::DocumentObjectGroupPython] C_element025  label="C_element : 012"  # scripted group (container) (typed FeaturePython)
  n = 6
  ref = C_element
FEATURE [App::DocumentObjectGroupPython] H_element021  label="H_element : 012"  # scripted group (container) (typed FeaturePython)
  n = 10
  ref = H_element
FEATURE [App::DocumentObjectGroupPython] O_element026  label="O_element : 5"  # scripted group (container) (typed FeaturePython)
  n = 5
  ref = O_element
FEATURE [App::DocumentObjectGroupPython] G4_CELLULOSE_CELLOPHANE  # scripted group (container) (typed FeaturePython)
  Dunit = g/cm3
  Dvalue = 1.42
  Group = -> [C_element025,H_element021,O_element026]
  conduct = 2
  density = 1
  expand = 3
  formula = G4_CELLULOSE_CELLOPHANE
  name = G4_CELLULOSE_CELLOPHANE
  specific = 4
FEATURE [App::DocumentObjectGroupPython] H_element022  label="H_element : 0.067"  # scripted group (container) (typed FeaturePython)
  n = 0.067125
FEATURE [App::DocumentObjectGroupPython] C_element026  label="C_element : 0.545"  # scripted group (container) (typed FeaturePython)
  n = 0.545403
FEATURE [App::DocumentObjectGroupPython] O_element027  label="O_element : 0.387"  # scripted group (container) (typed FeaturePython)
  n = 0.387472
FEATURE [App::DocumentObjectGroupPython] G4_CELLULOSE_BUTYRATE  # scripted group (container) (typed FeaturePython)
  Dunit = g/cm3
  Dvalue = 1.2
  Group = -> [H_element022,C_element026,O_element027]
  conduct = 2
  density = 1
  expand = 3
  formula = G4_CELLULOSE_BUTYRATE
  name = G4_CELLULOSE_BUTYRATE
  specific = 4
FEATURE [App::DocumentObjectGroupPython] H_element023  label="H_element : 0.029"  # scripted group (container) (typed FeaturePython)
  n = 0.029216
FEATURE [App::DocumentObjectGroupPython] C_element027  label="C_element : 0.271"  # scripted group (container) (typed FeaturePython)
  n = 0.271296
FEATURE [App::DocumentObjectGroupPython] N_element013  label="N_element : 0.121"  # scripted group (container) (typed FeaturePython)
  n = 0.121276
FEATURE [App::DocumentObjectGroupPython] O_element028  label="O_element : 0.578"  # scripted group (container) (typed FeaturePython)
  n = 0.578212
FEATURE [App::DocumentObjectGroupPython] G4_CELLULOSE_NITRATE  # scripted group (container) (typed FeaturePython)
  Dunit = g/cm3
  Dvalue = 1.49
  Group = -> [H_element023,C_element027,N_element013,O_element028]
  conduct = 2
  density = 1
  expand = 3
  formula = G4_CELLULOSE_NITRATE
  name = G4_CELLULOSE_NITRATE
  specific = 4
FEATURE [App::DocumentObjectGroupPython] H_element024  label="H_element : 0.108"  # scripted group (container) (typed FeaturePython)
  n = 0.107596
FEATURE [App::DocumentObjectGroupPython] N_element014  label="N_element : 0.001"  # scripted group (container) (typed FeaturePython)
  n = 0.0008
FEATURE [App::DocumentObjectGroupPython] O_element029  label="O_element : 0.875"  # scripted group (container) (typed FeaturePython)
  n = 0.874976
FEATURE [App::DocumentObjectGroupPython] S_element008  label="S_element : 0.015"  # scripted group (container) (typed FeaturePython)
  n = 0.014627
FEATURE [App::DocumentObjectGroupPython] Ce_element001  label="Ce_element : 0.002"  # scripted group (container) (typed FeaturePython)
  n = 0.002001
FEATURE [App::DocumentObjectGroupPython] G4_CERIC_SULFATE  # scripted group (container) (typed FeaturePython)
  Dunit = g/cm3
  Dvalue = 1.03
  Group = -> [H_element024,N_element014,O_element029,S_element008,Ce_element001]
  conduct = 2
  density = 1
  expand = 3
  formula = G4_CERIC_SULFATE
  name = G4_CERIC_SULFATE
  specific = 4
FEATURE [App::DocumentObjectGroupPython] Cs_element001  label="Cs_element : 1"  # scripted group (container) (typed FeaturePython)
  n = 1
  ref = Cs_element
FEATURE [App::DocumentObjectGroupPython] F_element006  label="F_element : 1"  # scripted group (container) (typed FeaturePython)
  n = 1
  ref = F_element
FEATURE [App::DocumentObjectGroupPython] G4_CESIUM_FLUORIDE  # scripted group (container) (typed FeaturePython)
  Dunit = g/cm3
  Dvalue = 4.115
  Group = -> [Cs_element001,F_element006]
  conduct = 2
  density = 1
  expand = 3
  formula = G4_CESIUM_FLUORIDE
  name = G4_CESIUM_FLUORIDE
  specific = 4
FEATURE [App::DocumentObjectGroupPython] Cs_element002  label="Cs_element : 002"  # scripted group (container) (typed FeaturePython)
  n = 1
  ref = Cs_element
FEATURE [App::DocumentObjectGroupPython] I_element001  label="I_element : 1"  # scripted group (container) (typed FeaturePython)
  n = 1
  ref = I_element
FEATURE [App::DocumentObjectGroupPython] G4_CESIUM_IODIDE  # scripted group (container) (typed FeaturePython)
  Dunit = g/cm3
  Dvalue = 4.51
  Group = -> [Cs_element002,I_element001]
  conduct = 2
  density = 1
  expand = 3
  formula = G4_CESIUM_IODIDE
  name = G4_CESIUM_IODIDE
  specific = 4
FEATURE [App::DocumentObjectGroupPython] C_element028  label="C_element : 013"  # scripted group (container) (typed FeaturePython)
  n = 6
  ref = C_element
FEATURE [App::DocumentObjectGroupPython] H_element025  label="H_element : 013"  # scripted group (container) (typed FeaturePython)
  n = 5
  ref = H_element
FEATURE [App::DocumentObjectGroupPython] Cl_element005  label="Cl_element : 1"  # scripted group (container) (typed FeaturePython)
  n = 1
  ref = Cl_element
FEATURE [App::DocumentObjectGroupPython] G4_CHLOROBENZENE  # scripted group (container) (typed FeaturePython)
  Dunit = g/cm3
  Dvalue = 1.1058
  Group = -> [C_element028,H_element025,Cl_element005]
  conduct = 2
  density = 1
  expand = 3
  formula = G4_CHLOROBENZENE
  name = G4_CHLOROBENZENE
  specific = 4
FEATURE [App::DocumentObjectGroupPython] C_element029  label="C_element : 014"  # scripted group (container) (typed FeaturePython)
  n = 1
  ref = C_element
FEATURE [App::DocumentObjectGroupPython] H_element026  label="H_element : 1"  # scripted group (container) (typed FeaturePython)
  n = 1
  ref = H_element
FEATURE [App::DocumentObjectGroupPython] Cl_element006  label="Cl_element : 3"  # scripted group (container) (typed FeaturePython)
  n = 3
  ref = Cl_element
FEATURE [App::DocumentObjectGroupPython] G4_CHLOROFORM  # scripted group (container) (typed FeaturePython)
  Dunit = g/cm3
  Dvalue = 1.4832
  Group = -> [C_element029,H_element026,Cl_element006]
  conduct = 2
  density = 1
  expand = 3
  formula = G4_CHLOROFORM
  name = G4_CHLOROFORM
  specific = 4
FEATURE [App::DocumentObjectGroupPython] H_element027  label="H_element : 0.010"  # scripted group (container) (typed FeaturePython)
  n = 0.01
FEATURE [App::DocumentObjectGroupPython] C_element030  label="C_element : 0.001"  # scripted group (container) (typed FeaturePython)
  n = 0.001
FEATURE [App::DocumentObjectGroupPython] O_element030  label="O_element : 0.529"  # scripted group (container) (typed FeaturePython)
  n = 0.529107
FEATURE [App::DocumentObjectGroupPython] Na_element005  label="Na_element : 0.016"  # scripted group (container) (typed FeaturePython)
  n = 0.016
FEATURE [App::DocumentObjectGroupPython] Mg_element003  label="Mg_element : 0.004"  # scripted group (container) (typed FeaturePython)
  n = 0.002
FEATURE [App::DocumentObjectGroupPython] Al_element002  label="Al_element : 0.034"  # scripted group (container) (typed FeaturePython)
  n = 0.033872
FEATURE [App::DocumentObjectGroupPython] Si_element002  label="Si_element : 0.337"  # scripted group (container) (typed FeaturePython)
  n = 0.337021
FEATURE [App::DocumentObjectGroupPython] K_element003  label="K_element : 0.013"  # scripted group (container) (typed FeaturePython)
  n = 0.013
FEATURE [App::DocumentObjectGroupPython] Ca_element010  label="Ca_element : 0.044"  # scripted group (container) (typed FeaturePython)
  n = 0.044
FEATURE [App::DocumentObjectGroupPython] Fe_element002  label="Fe_element : 0.014"  # scripted group (container) (typed FeaturePython)
  n = 0.014
FEATURE [App::DocumentObjectGroupPython] G4_CONCRETE  # scripted group (container) (typed FeaturePython)
  Dunit = g/cm3
  Dvalue = 2.3
  Group = -> [H_element027,C_element030,O_element030,Na_element005,Mg_element003,Al_element002,Si_element002,K_element003,Ca_element010,Fe_element002]
  conduct = 2
  density = 1
  expand = 3
  formula = G4_CONCRETE
  name = G4_CONCRETE
  specific = 4
FEATURE [App::DocumentObjectGroupPython] C_element031  label="C_element : 015"  # scripted group (container) (typed FeaturePython)
  n = 6
  ref = C_element
FEATURE [App::DocumentObjectGroupPython] H_element028  label="H_element : 12"  # scripted group (container) (typed FeaturePython)
  n = 12
  ref = H_element
FEATURE [App::DocumentObjectGroupPython] G4_CYCLOHEXANE  # scripted group (container) (typed FeaturePython)
  Dunit = g/cm3
  Dvalue = 0.779
  Group = -> [C_element031,H_element028]
  conduct = 2
  density = 1
  expand = 3
  formula = G4_CYCLOHEXANE
  name = G4_CYCLOHEXANE
  specific = 4
FEATURE [App::DocumentObjectGroupPython] C_element032  label="C_element : 016"  # scripted group (container) (typed FeaturePython)
  n = 6
  ref = C_element
FEATURE [App::DocumentObjectGroupPython] H_element029  label="H_element : 4"  # scripted group (container) (typed FeaturePython)
  n = 4
  ref = H_element
FEATURE [App::DocumentObjectGroupPython] Cl_element007  label="Cl_element : 2"  # scripted group (container) (typed FeaturePython)
  n = 2
  ref = Cl_element
FEATURE [App::DocumentObjectGroupPython] G4_1_2_DICHLOROBENZENE  label="G4_1.2-DICHLOROBENZENE"  # scripted group (container) (typed FeaturePython)
  Dunit = g/cm3
  Dvalue = 1.3048
  Group = -> [C_element032,H_element029,Cl_element007]
  conduct = 2
  density = 1
  expand = 3
  formula = G4_1.2-DICHLOROBENZENE
  name = G4_1.2-DICHLOROBENZENE
  specific = 4
FEATURE [App::DocumentObjectGroupPython] C_element033  label="C_element : 017"  # scripted group (container) (typed FeaturePython)
  n = 4
  ref = C_element
FEATURE [App::DocumentObjectGroupPython] H_element030  label="H_element : 8"  # scripted group (container) (typed FeaturePython)
  n = 8
  ref = H_element
FEATURE [App::DocumentObjectGroupPython] O_element031  label="O_element : 014"  # scripted group (container) (typed FeaturePython)
  n = 1
  ref = O_element
FEATURE [App::DocumentObjectGroupPython] Cl_element008  label="Cl_element : 005"  # scripted group (container) (typed FeaturePython)
  n = 2
  ref = Cl_element
FEATURE [App::DocumentObjectGroupPython] G4_DICHLORODIETHYL_ETHER  # scripted group (container) (typed FeaturePython)
  Dunit = g/cm3
  Dvalue = 1.2199
  Group = -> [C_element033,H_element030,O_element031,Cl_element008]
  conduct = 2
  density = 1
  expand = 3
  formula = G4_DICHLORODIETHYL_ETHER
  name = G4_DICHLORODIETHYL_ETHER
  specific = 4
FEATURE [App::DocumentObjectGroupPython] C_element034  label="C_element : 018"  # scripted group (container) (typed FeaturePython)
  n = 2
  ref = C_element
FEATURE [App::DocumentObjectGroupPython] H_element031  label="H_element : 014"  # scripted group (container) (typed FeaturePython)
  n = 4
  ref = H_element
FEATURE [App::DocumentObjectGroupPython] Cl_element009  label="Cl_element : 006"  # scripted group (container) (typed FeaturePython)
  n = 2
  ref = Cl_element
FEATURE [App::DocumentObjectGroupPython] G4_1_2_DICHLOROETHANE  label="G4_1.2-DICHLOROETHANE"  # scripted group (container) (typed FeaturePython)
  Dunit = g/cm3
  Dvalue = 1.2351
  Group = -> [C_element034,H_element031,Cl_element009]
  conduct = 2
  density = 1
  expand = 3
  formula = G4_1.2-DICHLOROETHANE
  name = G4_1.2-DICHLOROETHANE
  specific = 4
FEATURE [App::DocumentObjectGroupPython] C_element035  label="C_element : 019"  # scripted group (container) (typed FeaturePython)
  n = 4
  ref = C_element
FEATURE [App::DocumentObjectGroupPython] H_element032  label="H_element : 015"  # scripted group (container) (typed FeaturePython)
  n = 10
  ref = H_element
FEATURE [App::DocumentObjectGroupPython] O_element032  label="O_element : 015"  # scripted group (container) (typed FeaturePython)
  n = 1
  ref = O_element
FEATURE [App::DocumentObjectGroupPython] G4_DIETHYL_ETHER  # scripted group (container) (typed FeaturePython)
  Dunit = g/cm3
  Dvalue = 0.71378
  Group = -> [C_element035,H_element032,O_element032]
  conduct = 2
  density = 1
  expand = 3
  formula = G4_DIETHYL_ETHER
  name = G4_DIETHYL_ETHER
  specific = 4
FEATURE [App::DocumentObjectGroupPython] C_element036  label="C_element : 020"  # scripted group (container) (typed FeaturePython)
  n = 3
  ref = C_element
FEATURE [App::DocumentObjectGroupPython] H_element033  label="H_element : 016"  # scripted group (container) (typed FeaturePython)
  n = 7
  ref = H_element
FEATURE [App::DocumentObjectGroupPython] N_element015  label="N_element : 008"  # scripted group (container) (typed FeaturePython)
  n = 1
  ref = N_element
FEATURE [App::DocumentObjectGroupPython] O_element033  label="O_element : 016"  # scripted group (container) (typed FeaturePython)
  n = 1
  ref = O_element
FEATURE [App::DocumentObjectGroupPython] G4_N_N_DIMETHYL_FORMAMIDE  label="G4_N.N-DIMETHYL_FORMAMIDE"  # scripted group (container) (typed FeaturePython)
  Dunit = g/cm3
  Dvalue = 0.9487
  Group = -> [C_element036,H_element033,N_element015,O_element033]
  conduct = 2
  density = 1
  expand = 3
  formula = G4_N.N-DIMETHYL_FORMAMIDE
  name = G4_N.N-DIMETHYL_FORMAMIDE
  specific = 4
FEATURE [App::DocumentObjectGroupPython] C_element037  label="C_element : 021"  # scripted group (container) (typed FeaturePython)
  n = 2
  ref = C_element
FEATURE [App::DocumentObjectGroupPython] H_element034  label="H_element : 017"  # scripted group (container) (typed FeaturePython)
  n = 6
  ref = H_element
FEATURE [App::DocumentObjectGroupPython] O_element034  label="O_element : 017"  # scripted group (container) (typed FeaturePython)
  n = 1
  ref = O_element
FEATURE [App::DocumentObjectGroupPython] S_element009  label="S_element : 003"  # scripted group (container) (typed FeaturePython)
  n = 1
  ref = S_element
FEATURE [App::DocumentObjectGroupPython] G4_DIMETHYL_SULFOXIDE  # scripted group (container) (typed FeaturePython)
  Dunit = g/cm3
  Dvalue = 1.1014
  Group = -> [C_element037,H_element034,O_element034,S_element009]
  conduct = 2
  density = 1
  expand = 3
  formula = G4_DIMETHYL_SULFOXIDE
  name = G4_DIMETHYL_SULFOXIDE
  specific = 4
FEATURE [App::DocumentObjectGroupPython] C_element038  label="C_element : 022"  # scripted group (container) (typed FeaturePython)
  n = 2
  ref = C_element
FEATURE [App::DocumentObjectGroupPython] H_element035  label="H_element : 018"  # scripted group (container) (typed FeaturePython)
  n = 6
  ref = H_element
FEATURE [App::DocumentObjectGroupPython] G4_ETHANE  # scripted group (container) (typed FeaturePython)
  Dunit = g/cm3
  Dvalue = 0.00125324
  Group = -> [C_element038,H_element035]
  conduct = 2
  density = 1
  expand = 3
  formula = G4_ETHANE
  name = G4_ETHANE
  specific = 4
FEATURE [App::DocumentObjectGroupPython] C_element039  label="C_element : 023"  # scripted group (container) (typed FeaturePython)
  n = 2
  ref = C_element
FEATURE [App::DocumentObjectGroupPython] H_element036  label="H_element : 019"  # scripted group (container) (typed FeaturePython)
  n = 6
  ref = H_element
FEATURE [App::DocumentObjectGroupPython] O_element035  label="O_element : 018"  # scripted group (container) (typed FeaturePython)
  n = 1
  ref = O_element
FEATURE [App::DocumentObjectGroupPython] G4_ETHYL_ALCOHOL  # scripted group (container) (typed FeaturePython)
  Dunit = g/cm3
  Dvalue = 0.7893
  Group = -> [C_element039,H_element036,O_element035]
  conduct = 2
  density = 1
  expand = 3
  formula = G4_ETHYL_ALCOHOL
  name = G4_ETHYL_ALCOHOL
  specific = 4
FEATURE [App::DocumentObjectGroupPython] H_element037  label="H_element : 0.090"  # scripted group (container) (typed FeaturePython)
  n = 0.090027
FEATURE [App::DocumentObjectGroupPython] C_element040  label="C_element : 0.585"  # scripted group (container) (typed FeaturePython)
  n = 0.585182
FEATURE [App::DocumentObjectGroupPython] O_element036  label="O_element : 0.325"  # scripted group (container) (typed FeaturePython)
  n = 0.324791
FEATURE [App::DocumentObjectGroupPython] G4_ETHYL_CELLULOSE  # scripted group (container) (typed FeaturePython)
  Dunit = g/cm3
  Dvalue = 1.13
  Group = -> [H_element037,C_element040,O_element036]
  conduct = 2
  density = 1
  expand = 3
  formula = G4_ETHYL_CELLULOSE
  name = G4_ETHYL_CELLULOSE
  specific = 4
FEATURE [App::DocumentObjectGroupPython] C_element041  label="C_element : 024"  # scripted group (container) (typed FeaturePython)
  n = 2
  ref = C_element
FEATURE [App::DocumentObjectGroupPython] H_element038  label="H_element : 020"  # scripted group (container) (typed FeaturePython)
  n = 4
  ref = H_element
FEATURE [App::DocumentObjectGroupPython] G4_ETHYLENE  # scripted group (container) (typed FeaturePython)
  Dunit = g/cm3
  Dvalue = 0.00117497
  Group = -> [C_element041,H_element038]
  conduct = 2
  density = 1
  expand = 3
  formula = G4_ETHYLENE
  name = G4_ETHYLENE
  specific = 4
FEATURE [App::DocumentObjectGroupPython] H_element039  label="H_element : 0.096"  # scripted group (container) (typed FeaturePython)
  n = 0.096
FEATURE [App::DocumentObjectGroupPython] C_element042  label="C_element : 0.195"  # scripted group (container) (typed FeaturePython)
  n = 0.195
FEATURE [App::DocumentObjectGroupPython] N_element016  label="N_element : 0.057"  # scripted group (container) (typed FeaturePython)
  n = 0.057
FEATURE [App::DocumentObjectGroupPython] O_element037  label="O_element : 0.646"  # scripted group (container) (typed FeaturePython)
  n = 0.646
FEATURE [App::DocumentObjectGroupPython] Na_element006  label="Na_element : 0.017"  # scripted group (container) (typed FeaturePython)
  n = 0.001
FEATURE [App::DocumentObjectGroupPython] P_element005  label="P_element : 0.104"  # scripted group (container) (typed FeaturePython)
  n = 0.001
FEATURE [App::DocumentObjectGroupPython] S_element010  label="S_element : 0.016"  # scripted group (container) (typed FeaturePython)
  n = 0.003
FEATURE [App::DocumentObjectGroupPython] Cl_element010  label="Cl_element : 0.005"  # scripted group (container) (typed FeaturePython)
  n = 0.001
FEATURE [App::DocumentObjectGroupPython] G4_EYE_LENS_ICRP  # scripted group (container) (typed FeaturePython)
  Dunit = g/cm3
  Dvalue = 1.07
  Group = -> [H_element039,C_element042,N_element016,O_element037,Na_element006,P_element005,S_element010,Cl_element010]
  conduct = 2
  density = 1
  expand = 3
  formula = G4_EYE_LENS_ICRP
  name = G4_EYE_LENS_ICRP
  specific = 4
FEATURE [App::DocumentObjectGroupPython] Fe_element003  label="Fe_element : 2"  # scripted group (container) (typed FeaturePython)
  n = 2
  ref = Fe_element
FEATURE [App::DocumentObjectGroupPython] O_element038  label="O_element : 019"  # scripted group (container) (typed FeaturePython)
  n = 3
  ref = O_element
FEATURE [App::DocumentObjectGroupPython] G4_FERRIC_OXIDE  # scripted group (container) (typed FeaturePython)
  Dunit = g/cm3
  Dvalue = 5.2
  Group = -> [Fe_element003,O_element038]
  conduct = 2
  density = 1
  expand = 3
  formula = G4_FERRIC_OXIDE
  name = G4_FERRIC_OXIDE
  specific = 4
FEATURE [App::DocumentObjectGroupPython] Fe_element004  label="Fe_element : 1"  # scripted group (container) (typed FeaturePython)
  n = 1
  ref = Fe_element
FEATURE [App::DocumentObjectGroupPython] B_element003  label="B_element : 1"  # scripted group (container) (typed FeaturePython)
  n = 1
  ref = B_element
FEATURE [App::DocumentObjectGroupPython] G4_FERROBORIDE  # scripted group (container) (typed FeaturePython)
  Dunit = g/cm3
  Dvalue = 7.15
  Group = -> [Fe_element004,B_element003]
  conduct = 2
  density = 1
  expand = 3
  formula = G4_FERROBORIDE
  name = G4_FERROBORIDE
  specific = 4
FEATURE [App::DocumentObjectGroupPython] Fe_element005  label="Fe_element : 003"  # scripted group (container) (typed FeaturePython)
  n = 1
  ref = Fe_element
FEATURE [App::DocumentObjectGroupPython] O_element039  label="O_element : 020"  # scripted group (container) (typed FeaturePython)
  n = 1
  ref = O_element
FEATURE [App::DocumentObjectGroupPython] G4_FERROUS_OXIDE  # scripted group (container) (typed FeaturePython)
  Dunit = g/cm3
  Dvalue = 5.7
  Group = -> [Fe_element005,O_element039]
  conduct = 2
  density = 1
  expand = 3
  formula = G4_FERROUS_OXIDE
  name = G4_FERROUS_OXIDE
  specific = 4
FEATURE [App::DocumentObjectGroupPython] H_element040  label="H_element : 0.115"  # scripted group (container) (typed FeaturePython)
  n = 0.108259
FEATURE [App::DocumentObjectGroupPython] N_element017  label="N_element : 0.000"  # scripted group (container) (typed FeaturePython)
  n = 2.7e-05
FEATURE [App::DocumentObjectGroupPython] O_element040  label="O_element : 0.879"  # scripted group (container) (typed FeaturePython)
  n = 0.878636
FEATURE [App::DocumentObjectGroupPython] Na_element007  label="Na_element : 0.000"  # scripted group (container) (typed FeaturePython)
  n = 2.2e-05
FEATURE [App::DocumentObjectGroupPython] S_element011  label="S_element : 0.013"  # scripted group (container) (typed FeaturePython)
  n = 0.012968
FEATURE [App::DocumentObjectGroupPython] Cl_element011  label="Cl_element : 0.000"  # scripted group (container) (typed FeaturePython)
  n = 3.4e-05
FEATURE [App::DocumentObjectGroupPython] Fe_element006  label="Fe_element : 0.000"  # scripted group (container) (typed FeaturePython)
  n = 5.4e-05
FEATURE [App::DocumentObjectGroupPython] G4_FERROUS_SULFATE  # scripted group (container) (typed FeaturePython)
  Dunit = g/cm3
  Dvalue = 1.024
  Group = -> [H_element040,N_element017,O_element040,Na_element007,S_element011,Cl_element011,Fe_element006]
  conduct = 2
  density = 1
  expand = 3
  formula = G4_FERROUS_SULFATE
  name = G4_FERROUS_SULFATE
  specific = 4
FEATURE [App::DocumentObjectGroupPython] C_element043  label="C_element : 0.099"  # scripted group (container) (typed FeaturePython)
  n = 0.099335
FEATURE [App::DocumentObjectGroupPython] F_element007  label="F_element : 0.314"  # scripted group (container) (typed FeaturePython)
  n = 0.314247
FEATURE [App::DocumentObjectGroupPython] Cl_element012  label="Cl_element : 0.586"  # scripted group (container) (typed FeaturePython)
  n = 0.586418
FEATURE [App::DocumentObjectGroupPython] G4_FREON_12  label="G4_FREON-12"  # scripted group (container) (typed FeaturePython)
  Dunit = g/cm3
  Dvalue = 1.12
  Group = -> [C_element043,F_element007,Cl_element012]
  conduct = 2
  density = 1
  expand = 3
  formula = G4_FREON-12
  name = G4_FREON-12
  specific = 4
FEATURE [App::DocumentObjectGroupPython] C_element044  label="C_element : 0.057"  # scripted group (container) (typed FeaturePython)
  n = 0.057245
FEATURE [App::DocumentObjectGroupPython] F_element008  label="F_element : 0.181"  # scripted group (container) (typed FeaturePython)
  n = 0.181096
FEATURE [App::DocumentObjectGroupPython] Br_element001  label="Br_element : 0.762"  # scripted group (container) (typed FeaturePython)
  n = 0.761659
FEATURE [App::DocumentObjectGroupPython] G4_FREON_12B2  label="G4_FREON-12B2"  # scripted group (container) (typed FeaturePython)
  Dunit = g/cm3
  Dvalue = 1.8
  Group = -> [C_element044,F_element008,Br_element001]
  conduct = 2
  density = 1
  expand = 3
  formula = G4_FREON-12B2
  name = G4_FREON-12B2
  specific = 4
FEATURE [App::DocumentObjectGroupPython] C_element045  label="C_element : 0.115"  # scripted group (container) (typed FeaturePython)
  n = 0.114983
FEATURE [App::DocumentObjectGroupPython] F_element009  label="F_element : 0.546"  # scripted group (container) (typed FeaturePython)
  n = 0.545621
FEATURE [App::DocumentObjectGroupPython] Cl_element013  label="Cl_element : 0.339"  # scripted group (container) (typed FeaturePython)
  n = 0.339396
FEATURE [App::DocumentObjectGroupPython] G4_FREON_13  label="G4_FREON-13"  # scripted group (container) (typed FeaturePython)
  Dunit = g/cm3
  Dvalue = 0.95
  Group = -> [C_element045,F_element009,Cl_element013]
  conduct = 2
  density = 1
  expand = 3
  formula = G4_FREON-13
  name = G4_FREON-13
  specific = 4
FEATURE [App::DocumentObjectGroupPython] C_element046  label="C_element : 025"  # scripted group (container) (typed FeaturePython)
  n = 1
  ref = C_element
FEATURE [App::DocumentObjectGroupPython] F_element010  label="F_element : 3"  # scripted group (container) (typed FeaturePython)
  n = 3
  ref = F_element
FEATURE [App::DocumentObjectGroupPython] Br_element002  label="Br_element : 1"  # scripted group (container) (typed FeaturePython)
  n = 1
  ref = Br_element
FEATURE [App::DocumentObjectGroupPython] G4_FREON_13B1  label="G4_FREON-13B1"  # scripted group (container) (typed FeaturePython)
  Dunit = g/cm3
  Dvalue = 1.5
  Group = -> [C_element046,F_element010,Br_element002]
  conduct = 2
  density = 1
  expand = 3
  formula = G4_FREON-13B1
  name = G4_FREON-13B1
  specific = 4
FEATURE [App::DocumentObjectGroupPython] C_element047  label="C_element : 0.061"  # scripted group (container) (typed FeaturePython)
  n = 0.061309
FEATURE [App::DocumentObjectGroupPython] F_element011  label="F_element : 0.291"  # scripted group (container) (typed FeaturePython)
  n = 0.290924
FEATURE [App::DocumentObjectGroupPython] I_element002  label="I_element : 0.648"  # scripted group (container) (typed FeaturePython)
  n = 0.647767
FEATURE [App::DocumentObjectGroupPython] G4_FREON_13I1  label="G4_FREON-13I1"  # scripted group (container) (typed FeaturePython)
  Dunit = g/cm3
  Dvalue = 1.8
  Group = -> [C_element047,F_element011,I_element002]
  conduct = 2
  density = 1
  expand = 3
  formula = G4_FREON-13I1
  name = G4_FREON-13I1
  specific = 4
FEATURE [App::DocumentObjectGroupPython] Gd_element001  label="Gd_element : 2"  # scripted group (container) (typed FeaturePython)
  n = 2
  ref = Gd_element
FEATURE [App::DocumentObjectGroupPython] O_element041  label="O_element : 021"  # scripted group (container) (typed FeaturePython)
  n = 2
  ref = O_element
FEATURE [App::DocumentObjectGroupPython] S_element012  label="S_element : 004"  # scripted group (container) (typed FeaturePython)
  n = 1
  ref = S_element
FEATURE [App::DocumentObjectGroupPython] G4_GADOLINIUM_OXYSULFIDE  # scripted group (container) (typed FeaturePython)
  Dunit = g/cm3
  Dvalue = 7.44
  Group = -> [Gd_element001,O_element041,S_element012]
  conduct = 2
  density = 1
  expand = 3
  formula = G4_GADOLINIUM_OXYSULFIDE
  name = G4_GADOLINIUM_OXYSULFIDE
  specific = 4
FEATURE [App::DocumentObjectGroupPython] Ga_element001  label="Ga_element : 1"  # scripted group (container) (typed FeaturePython)
  n = 1
  ref = Ga_element
FEATURE [App::DocumentObjectGroupPython] As_element001  label="As_element : 1"  # scripted group (container) (typed FeaturePython)
  n = 1
  ref = As_element
FEATURE [App::DocumentObjectGroupPython] G4_GALLIUM_ARSENIDE  # scripted group (container) (typed FeaturePython)
  Dunit = g/cm3
  Dvalue = 5.31
  Group = -> [Ga_element001,As_element001]
  conduct = 2
  density = 1
  expand = 3
  formula = G4_GALLIUM_ARSENIDE
  name = G4_GALLIUM_ARSENIDE
  specific = 4
FEATURE [App::DocumentObjectGroupPython] H_element041  label="H_element : 0.081"  # scripted group (container) (typed FeaturePython)
  n = 0.08118
FEATURE [App::DocumentObjectGroupPython] C_element048  label="C_element : 0.416"  # scripted group (container) (typed FeaturePython)
  n = 0.41606
FEATURE [App::DocumentObjectGroupPython] N_element018  label="N_element : 0.111"  # scripted group (container) (typed FeaturePython)
  n = 0.11124
FEATURE [App::DocumentObjectGroupPython] O_element042  label="O_element : 0.381"  # scripted group (container) (typed FeaturePython)
  n = 0.38064
FEATURE [App::DocumentObjectGroupPython] S_element013  label="S_element : 0.011"  # scripted group (container) (typed FeaturePython)
  n = 0.01088
FEATURE [App::DocumentObjectGroupPython] G4_GEL_PHOTO_EMULSION  # scripted group (container) (typed FeaturePython)
  Dunit = g/cm3
  Dvalue = 1.2914
  Group = -> [H_element041,C_element048,N_element018,O_element042,S_element013]
  conduct = 2
  density = 1
  expand = 3
  formula = G4_GEL_PHOTO_EMULSION
  name = G4_GEL_PHOTO_EMULSION
  specific = 4
FEATURE [App::DocumentObjectGroupPython] B_element004  label="B_element : 0.040"  # scripted group (container) (typed FeaturePython)
  n = 0.0400639
FEATURE [App::DocumentObjectGroupPython] O_element043  label="O_element : 0.540"  # scripted group (container) (typed FeaturePython)
  n = 0.539561
FEATURE [App::DocumentObjectGroupPython] Na_element008  label="Na_element : 0.028"  # scripted group (container) (typed FeaturePython)
  n = 0.0281909
FEATURE [App::DocumentObjectGroupPython] Al_element003  label="Al_element : 0.012"  # scripted group (container) (typed FeaturePython)
  n = 0.011644
FEATURE [App::DocumentObjectGroupPython] Si_element003  label="Si_element : 0.377"  # scripted group (container) (typed FeaturePython)
  n = 0.377219
FEATURE [App::DocumentObjectGroupPython] K_element004  label="K_element : 0.014"  # scripted group (container) (typed FeaturePython)
  n = 0.00332099
FEATURE [App::DocumentObjectGroupPython] G4_Pyrex_Glass  # scripted group (container) (typed FeaturePython)
  Dunit = g/cm3
  Dvalue = 2.23
  Group = -> [B_element004,O_element043,Na_element008,Al_element003,Si_element003,K_element004]
  conduct = 2
  density = 1
  expand = 3
  formula = G4_Pyrex_Glass
  name = G4_Pyrex_Glass
  specific = 4
FEATURE [App::DocumentObjectGroupPython] O_element044  label="O_element : 0.156"  # scripted group (container) (typed FeaturePython)
  n = 0.156453
FEATURE [App::DocumentObjectGroupPython] Si_element004  label="Si_element : 0.081"  # scripted group (container) (typed FeaturePython)
  n = 0.080866
FEATURE [App::DocumentObjectGroupPython] Ti_element001  label="Ti_element : 0.008"  # scripted group (container) (typed FeaturePython)
  n = 0.008092
FEATURE [App::DocumentObjectGroupPython] As_element002  label="As_element : 0.003"  # scripted group (container) (typed FeaturePython)
  n = 0.002651
FEATURE [App::DocumentObjectGroupPython] Pb_element001  label="Pb_element : 0.752"  # scripted group (container) (typed FeaturePython)
  n = 0.751938
FEATURE [App::DocumentObjectGroupPython] G4_GLASS_LEAD  # scripted group (container) (typed FeaturePython)
  Dunit = g/cm3
  Dvalue = 6.22
  Group = -> [O_element044,Si_element004,Ti_element001,As_element002,Pb_element001]
  conduct = 2
  density = 1
  expand = 3
  formula = G4_GLASS_LEAD
  name = G4_GLASS_LEAD
  specific = 4
FEATURE [App::DocumentObjectGroupPython] O_element045  label="O_element : 0.460"  # scripted group (container) (typed FeaturePython)
  n = 0.4598
FEATURE [App::DocumentObjectGroupPython] Na_element009  label="Na_element : 0.096"  # scripted group (container) (typed FeaturePython)
  n = 0.0964411
FEATURE [App::DocumentObjectGroupPython] Si_element005  label="Si_element : 0.378"  # scripted group (container) (typed FeaturePython)
  n = 0.336553
FEATURE [App::DocumentObjectGroupPython] Ca_element011  label="Ca_element : 0.107"  # scripted group (container) (typed FeaturePython)
  n = 0.107205
FEATURE [App::DocumentObjectGroupPython] G4_GLASS_PLATE  # scripted group (container) (typed FeaturePython)
  Dunit = g/cm3
  Dvalue = 2.4
  Group = -> [O_element045,Na_element009,Si_element005,Ca_element011]
  conduct = 2
  density = 1
  expand = 3
  formula = G4_GLASS_PLATE
  name = G4_GLASS_PLATE
  specific = 4
FEATURE [App::DocumentObjectGroupPython] C_element049  label="C_element : 026"  # scripted group (container) (typed FeaturePython)
  n = 5
  ref = C_element
FEATURE [App::DocumentObjectGroupPython] H_element042  label="H_element : 021"  # scripted group (container) (typed FeaturePython)
  n = 10
  ref = H_element
FEATURE [App::DocumentObjectGroupPython] N_element019  label="N_element : 2"  # scripted group (container) (typed FeaturePython)
  n = 2
  ref = N_element
FEATURE [App::DocumentObjectGroupPython] O_element046  label="O_element : 022"  # scripted group (container) (typed FeaturePython)
  n = 3
  ref = O_element
FEATURE [App::DocumentObjectGroupPython] G4_GLUTAMINE  # scripted group (container) (typed FeaturePython)
  Dunit = g/cm3
  Dvalue = 1.46
  Group = -> [C_element049,H_element042,N_element019,O_element046]
  conduct = 2
  density = 1
  expand = 3
  formula = G4_GLUTAMINE
  name = G4_GLUTAMINE
  specific = 4
FEATURE [App::DocumentObjectGroupPython] C_element050  label="C_element : 027"  # scripted group (container) (typed FeaturePython)
  n = 3
  ref = C_element
FEATURE [App::DocumentObjectGroupPython] H_element043  label="H_element : 022"  # scripted group (container) (typed FeaturePython)
  n = 8
  ref = H_element
FEATURE [App::DocumentObjectGroupPython] O_element047  label="O_element : 023"  # scripted group (container) (typed FeaturePython)
  n = 3
  ref = O_element
FEATURE [App::DocumentObjectGroupPython] G4_GLYCEROL  # scripted group (container) (typed FeaturePython)
  Dunit = g/cm3
  Dvalue = 1.2613
  Group = -> [C_element050,H_element043,O_element047]
  conduct = 2
  density = 1
  expand = 3
  formula = G4_GLYCEROL
  name = G4_GLYCEROL
  specific = 4
FEATURE [App::DocumentObjectGroupPython] C_element051  label="C_element : 028"  # scripted group (container) (typed FeaturePython)
  n = 5
  ref = C_element
FEATURE [App::DocumentObjectGroupPython] H_element044  label="H_element : 023"  # scripted group (container) (typed FeaturePython)
  n = 5
  ref = H_element
FEATURE [App::DocumentObjectGroupPython] N_element020  label="N_element : 009"  # scripted group (container) (typed FeaturePython)
  n = 5
  ref = N_element
FEATURE [App::DocumentObjectGroupPython] O_element048  label="O_element : 024"  # scripted group (container) (typed FeaturePython)
  n = 1
  ref = O_element
FEATURE [App::DocumentObjectGroupPython] G4_GUANINE  # scripted group (container) (typed FeaturePython)
  Dunit = g/cm3
  Dvalue = 2.2
  Group = -> [C_element051,H_element044,N_element020,O_element048]
  conduct = 2
  density = 1
  expand = 3
  formula = G4_GUANINE
  name = G4_GUANINE
  specific = 4
FEATURE [App::DocumentObjectGroupPython] Ca_element012  label="Ca_element : 006"  # scripted group (container) (typed FeaturePython)
  n = 1
  ref = Ca_element
FEATURE [App::DocumentObjectGroupPython] S_element014  label="S_element : 005"  # scripted group (container) (typed FeaturePython)
  n = 1
  ref = S_element
FEATURE [App::DocumentObjectGroupPython] O_element049  label="O_element : 6"  # scripted group (container) (typed FeaturePython)
  n = 6
  ref = O_element
FEATURE [App::DocumentObjectGroupPython] H_element045  label="H_element : 024"  # scripted group (container) (typed FeaturePython)
  n = 4
  ref = H_element
FEATURE [App::DocumentObjectGroupPython] G4_GYPSUM  # scripted group (container) (typed FeaturePython)
  Dunit = g/cm3
  Dvalue = 2.32
  Group = -> [Ca_element012,S_element014,O_element049,H_element045]
  conduct = 2
  density = 1
  expand = 3
  formula = G4_GYPSUM
  name = G4_GYPSUM
  specific = 4
FEATURE [App::DocumentObjectGroupPython] C_element052  label="C_element : 7"  # scripted group (container) (typed FeaturePython)
  n = 7
  ref = C_element
FEATURE [App::DocumentObjectGroupPython] H_element046  label="H_element : 16"  # scripted group (container) (typed FeaturePython)
  n = 16
  ref = H_element
FEATURE [App::DocumentObjectGroupPython] G4_N_HEPTANE  label="G4_N-HEPTANE"  # scripted group (container) (typed FeaturePython)
  Dunit = g/cm3
  Dvalue = 0.68376
  Group = -> [C_element052,H_element046]
  conduct = 2
  density = 1
  expand = 3
  formula = G4_N-HEPTANE
  name = G4_N-HEPTANE
  specific = 4
FEATURE [App::DocumentObjectGroupPython] C_element053  label="C_element : 029"  # scripted group (container) (typed FeaturePython)
  n = 6
  ref = C_element
FEATURE [App::DocumentObjectGroupPython] H_element047  label="H_element : 14"  # scripted group (container) (typed FeaturePython)
  n = 14
  ref = H_element
FEATURE [App::DocumentObjectGroupPython] G4_N_HEXANE  label="G4_N-HEXANE"  # scripted group (container) (typed FeaturePython)
  Dunit = g/cm3
  Dvalue = 0.6603
  Group = -> [C_element053,H_element047]
  conduct = 2
  density = 1
  expand = 3
  formula = G4_N-HEXANE
  name = G4_N-HEXANE
  specific = 4
FEATURE [App::DocumentObjectGroupPython] C_element054  label="C_element : 22"  # scripted group (container) (typed FeaturePython)
  n = 22
  ref = C_element
FEATURE [App::DocumentObjectGroupPython] H_element048  label="H_element : 025"  # scripted group (container) (typed FeaturePython)
  n = 10
  ref = H_element
FEATURE [App::DocumentObjectGroupPython] N_element021  label="N_element : 010"  # scripted group (container) (typed FeaturePython)
  n = 2
  ref = N_element
FEATURE [App::DocumentObjectGroupPython] O_element050  label="O_element : 025"  # scripted group (container) (typed FeaturePython)
  n = 5
  ref = O_element
FEATURE [App::DocumentObjectGroupPython] G4_KAPTON  # scripted group (container) (typed FeaturePython)
  Dunit = g/cm3
  Dvalue = 1.42
  Group = -> [C_element054,H_element048,N_element021,O_element050]
  conduct = 2
  density = 1
  expand = 3
  formula = G4_KAPTON
  name = G4_KAPTON
  specific = 4
FEATURE [App::DocumentObjectGroupPython] La_element001  label="La_element : 1"  # scripted group (container) (typed FeaturePython)
  n = 1
  ref = La_element
FEATURE [App::DocumentObjectGroupPython] Br_element003  label="Br_element : 002"  # scripted group (container) (typed FeaturePython)
  n = 1
  ref = Br_element
FEATURE [App::DocumentObjectGroupPython] O_element051  label="O_element : 026"  # scripted group (container) (typed FeaturePython)
  n = 1
  ref = O_element
FEATURE [App::DocumentObjectGroupPython] G4_LANTHANUM_OXYBROMIDE  # scripted group (container) (typed FeaturePython)
  Dunit = g/cm3
  Dvalue = 6.28
  Group = -> [La_element001,Br_element003,O_element051]
  conduct = 2
  density = 1
  expand = 3
  formula = G4_LANTHANUM_OXYBROMIDE
  name = G4_LANTHANUM_OXYBROMIDE
  specific = 4
FEATURE [App::DocumentObjectGroupPython] La_element002  label="La_element : 2"  # scripted group (container) (typed FeaturePython)
  n = 2
  ref = La_element
FEATURE [App::DocumentObjectGroupPython] O_element052  label="O_element : 027"  # scripted group (container) (typed FeaturePython)
  n = 2
  ref = O_element
FEATURE [App::DocumentObjectGroupPython] S_element015  label="S_element : 006"  # scripted group (container) (typed FeaturePython)
  n = 1
  ref = S_element
FEATURE [App::DocumentObjectGroupPython] G4_LANTHANUM_OXYSULFIDE  # scripted group (container) (typed FeaturePython)
  Dunit = g/cm3
  Dvalue = 5.86
  Group = -> [La_element002,O_element052,S_element015]
  conduct = 2
  density = 1
  expand = 3
  formula = G4_LANTHANUM_OXYSULFIDE
  name = G4_LANTHANUM_OXYSULFIDE
  specific = 4
FEATURE [App::DocumentObjectGroupPython] O_element053  label="O_element : 0.072"  # scripted group (container) (typed FeaturePython)
  n = 0.071682
FEATURE [App::DocumentObjectGroupPython] Pb_element002  label="Pb_element : 0.928"  # scripted group (container) (typed FeaturePython)
  n = 0.928318
FEATURE [App::DocumentObjectGroupPython] G4_LEAD_OXIDE  # scripted group (container) (typed FeaturePython)
  Dunit = g/cm3
  Dvalue = 9.53
  Group = -> [O_element053,Pb_element002]
  conduct = 2
  density = 1
  expand = 3
  formula = G4_LEAD_OXIDE
  name = G4_LEAD_OXIDE
  specific = 4
FEATURE [App::DocumentObjectGroupPython] Li_element001  label="Li_element : 1"  # scripted group (container) (typed FeaturePython)
  n = 1
  ref = Li_element
FEATURE [App::DocumentObjectGroupPython] N_element022  label="N_element : 011"  # scripted group (container) (typed FeaturePython)
  n = 1
  ref = N_element
FEATURE [App::DocumentObjectGroupPython] H_element049  label="H_element : 026"  # scripted group (container) (typed FeaturePython)
  n = 2
  ref = H_element
FEATURE [App::DocumentObjectGroupPython] G4_LITHIUM_AMIDE  # scripted group (container) (typed FeaturePython)
  Dunit = g/cm3
  Dvalue = 1.178
  Group = -> [Li_element001,N_element022,H_element049]
  conduct = 2
  density = 1
  expand = 3
  formula = G4_LITHIUM_AMIDE
  name = G4_LITHIUM_AMIDE
  specific = 4
FEATURE [App::DocumentObjectGroupPython] Li_element002  label="Li_element : 2"  # scripted group (container) (typed FeaturePython)
  n = 2
  ref = Li_element
FEATURE [App::DocumentObjectGroupPython] C_element055  label="C_element : 030"  # scripted group (container) (typed FeaturePython)
  n = 1
  ref = C_element
FEATURE [App::DocumentObjectGroupPython] O_element054  label="O_element : 028"  # scripted group (container) (typed FeaturePython)
  n = 3
  ref = O_element
FEATURE [App::DocumentObjectGroupPython] G4_LITHIUM_CARBONATE  # scripted group (container) (typed FeaturePython)
  Dunit = g/cm3
  Dvalue = 2.11
  Group = -> [Li_element002,C_element055,O_element054]
  conduct = 2
  density = 1
  expand = 3
  formula = G4_LITHIUM_CARBONATE
  name = G4_LITHIUM_CARBONATE
  specific = 4
FEATURE [App::DocumentObjectGroupPython] Li_element003  label="Li_element : 003"  # scripted group (container) (typed FeaturePython)
  n = 1
  ref = Li_element
FEATURE [App::DocumentObjectGroupPython] F_element012  label="F_element : 004"  # scripted group (container) (typed FeaturePython)
  n = 1
  ref = F_element
FEATURE [App::DocumentObjectGroupPython] G4_LITHIUM_FLUORIDE  # scripted group (container) (typed FeaturePython)
  Dunit = g/cm3
  Dvalue = 2.635
  Group = -> [Li_element003,F_element012]
  conduct = 2
  density = 1
  expand = 3
  formula = G4_LITHIUM_FLUORIDE
  name = G4_LITHIUM_FLUORIDE
  specific = 4
FEATURE [App::DocumentObjectGroupPython] Li_element004  label="Li_element : 004"  # scripted group (container) (typed FeaturePython)
  n = 1
  ref = Li_element
FEATURE [App::DocumentObjectGroupPython] H_element050  label="H_element : 027"  # scripted group (container) (typed FeaturePython)
  n = 1
  ref = H_element
FEATURE [App::DocumentObjectGroupPython] G4_LITHIUM_HYDRIDE  # scripted group (container) (typed FeaturePython)
  Dunit = g/cm3
  Dvalue = 0.82
  Group = -> [Li_element004,H_element050]
  conduct = 2
  density = 1
  expand = 3
  formula = G4_LITHIUM_HYDRIDE
  name = G4_LITHIUM_HYDRIDE
  specific = 4
FEATURE [App::DocumentObjectGroupPython] Li_element005  label="Li_element : 005"  # scripted group (container) (typed FeaturePython)
  n = 1
  ref = Li_element
FEATURE [App::DocumentObjectGroupPython] I_element003  label="I_element : 002"  # scripted group (container) (typed FeaturePython)
  n = 1
  ref = I_element
FEATURE [App::DocumentObjectGroupPython] G4_LITHIUM_IODIDE  # scripted group (container) (typed FeaturePython)
  Dunit = g/cm3
  Dvalue = 3.494
  Group = -> [Li_element005,I_element003]
  conduct = 2
  density = 1
  expand = 3
  formula = G4_LITHIUM_IODIDE
  name = G4_LITHIUM_IODIDE
  specific = 4
FEATURE [App::DocumentObjectGroupPython] Li_element006  label="Li_element : 006"  # scripted group (container) (typed FeaturePython)
  n = 2
  ref = Li_element
FEATURE [App::DocumentObjectGroupPython] O_element055  label="O_element : 029"  # scripted group (container) (typed FeaturePython)
  n = 1
  ref = O_element
FEATURE [App::DocumentObjectGroupPython] G4_LITHIUM_OXIDE  # scripted group (container) (typed FeaturePython)
  Dunit = g/cm3
  Dvalue = 2.013
  Group = -> [Li_element006,O_element055]
  conduct = 2
  density = 1
  expand = 3
  formula = G4_LITHIUM_OXIDE
  name = G4_LITHIUM_OXIDE
  specific = 4
FEATURE [App::DocumentObjectGroupPython] Li_element007  label="Li_element : 007"  # scripted group (container) (typed FeaturePython)
  n = 2
  ref = Li_element
FEATURE [App::DocumentObjectGroupPython] B_element005  label="B_element : 005"  # scripted group (container) (typed FeaturePython)
  n = 4
  ref = B_element
FEATURE [App::DocumentObjectGroupPython] O_element056  label="O_element : 7"  # scripted group (container) (typed FeaturePython)
  n = 7
  ref = O_element
FEATURE [App::DocumentObjectGroupPython] G4_LITHIUM_TETRABORATE  # scripted group (container) (typed FeaturePython)
  Dunit = g/cm3
  Dvalue = 2.44
  Group = -> [Li_element007,B_element005,O_element056]
  conduct = 2
  density = 1
  expand = 3
  formula = G4_LITHIUM_TETRABORATE
  name = G4_LITHIUM_TETRABORATE
  specific = 4
FEATURE [App::DocumentObjectGroupPython] H_element051  label="H_element : 0.105"  # scripted group (container) (typed FeaturePython)
  n = 0.105
FEATURE [App::DocumentObjectGroupPython] C_element056  label="C_element : 0.083"  # scripted group (container) (typed FeaturePython)
  n = 0.083
FEATURE [App::DocumentObjectGroupPython] N_element023  label="N_element : 0.023"  # scripted group (container) (typed FeaturePython)
  n = 0.023
FEATURE [App::DocumentObjectGroupPython] O_element057  label="O_element : 0.779"  # scripted group (container) (typed FeaturePython)
  n = 0.779
FEATURE [App::DocumentObjectGroupPython] Na_element010  label="Na_element : 0.097"  # scripted group (container) (typed FeaturePython)
  n = 0.002
FEATURE [App::DocumentObjectGroupPython] P_element006  label="P_element : 0.105"  # scripted group (container) (typed FeaturePython)
  n = 0.001
FEATURE [App::DocumentObjectGroupPython] S_element016  label="S_element : 0.017"  # scripted group (container) (typed FeaturePython)
  n = 0.002
FEATURE [App::DocumentObjectGroupPython] Cl_element014  label="Cl_element : 0.587"  # scripted group (container) (typed FeaturePython)
  n = 0.003
FEATURE [App::DocumentObjectGroupPython] K_element005  label="K_element : 0.015"  # scripted group (container) (typed FeaturePython)
  n = 0.002
FEATURE [App::DocumentObjectGroupPython] G4_LUNG_ICRP  # scripted group (container) (typed FeaturePython)
  Dunit = g/cm3
  Dvalue = 1.04
  Group = -> [H_element051,C_element056,N_element023,O_element057,Na_element010,P_element006,S_element016,Cl_element014,K_element005]
  conduct = 2
  density = 1
  expand = 3
  formula = G4_LUNG_ICRP
  name = G4_LUNG_ICRP
  specific = 4
FEATURE [App::DocumentObjectGroupPython] H_element052  label="H_element : 0.116"  # scripted group (container) (typed FeaturePython)
  n = 0.114318
FEATURE [App::DocumentObjectGroupPython] C_element057  label="C_element : 0.656"  # scripted group (container) (typed FeaturePython)
  n = 0.655824
FEATURE [App::DocumentObjectGroupPython] O_element058  label="O_element : 0.092"  # scripted group (container) (typed FeaturePython)
  n = 0.0921831
FEATURE [App::DocumentObjectGroupPython] Mg_element004  label="Mg_element : 0.135"  # scripted group (container) (typed FeaturePython)
  n = 0.134792
FEATURE [App::DocumentObjectGroupPython] Ca_element013  label="Ca_element : 0.003"  # scripted group (container) (typed FeaturePython)
  n = 0.002883
FEATURE [App::DocumentObjectGroupPython] G4_M3_WAX  # scripted group (container) (typed FeaturePython)
  Dunit = g/cm3
  Dvalue = 1.05
  Group = -> [H_element052,C_element057,O_element058,Mg_element004,Ca_element013]
  conduct = 2
  density = 1
  expand = 3
  formula = G4_M3_WAX
  name = G4_M3_WAX
  specific = 4
FEATURE [App::DocumentObjectGroupPython] Mg_element005  label="Mg_element : 1"  # scripted group (container) (typed FeaturePython)
  n = 1
  ref = Mg_element
FEATURE [App::DocumentObjectGroupPython] C_element058  label="C_element : 031"  # scripted group (container) (typed FeaturePython)
  n = 1
  ref = C_element
FEATURE [App::DocumentObjectGroupPython] O_element059  label="O_element : 030"  # scripted group (container) (typed FeaturePython)
  n = 3
  ref = O_element
FEATURE [App::DocumentObjectGroupPython] G4_MAGNESIUM_CARBONATE  # scripted group (container) (typed FeaturePython)
  Dunit = g/cm3
  Dvalue = 2.958
  Group = -> [Mg_element005,C_element058,O_element059]
  conduct = 2
  density = 1
  expand = 3
  formula = G4_MAGNESIUM_CARBONATE
  name = G4_MAGNESIUM_CARBONATE
  specific = 4
FEATURE [App::DocumentObjectGroupPython] Mg_element006  label="Mg_element : 002"  # scripted group (container) (typed FeaturePython)
  n = 1
  ref = Mg_element
FEATURE [App::DocumentObjectGroupPython] F_element013  label="F_element : 005"  # scripted group (container) (typed FeaturePython)
  n = 2
  ref = F_element
FEATURE [App::DocumentObjectGroupPython] G4_MAGNESIUM_FLUORIDE  # scripted group (container) (typed FeaturePython)
  Dunit = g/cm3
  Dvalue = 3
  Group = -> [Mg_element006,F_element013]
  conduct = 2
  density = 1
  expand = 3
  formula = G4_MAGNESIUM_FLUORIDE
  name = G4_MAGNESIUM_FLUORIDE
  specific = 4
FEATURE [App::DocumentObjectGroupPython] Mg_element007  label="Mg_element : 003"  # scripted group (container) (typed FeaturePython)
  n = 1
  ref = Mg_element
FEATURE [App::DocumentObjectGroupPython] O_element060  label="O_element : 031"  # scripted group (container) (typed FeaturePython)
  n = 1
  ref = O_element
FEATURE [App::DocumentObjectGroupPython] G4_MAGNESIUM_OXIDE  # scripted group (container) (typed FeaturePython)
  Dunit = g/cm3
  Dvalue = 3.58
  Group = -> [Mg_element007,O_element060]
  conduct = 2
  density = 1
  expand = 3
  formula = G4_MAGNESIUM_OXIDE
  name = G4_MAGNESIUM_OXIDE
  specific = 4
FEATURE [App::DocumentObjectGroupPython] Mg_element008  label="Mg_element : 004"  # scripted group (container) (typed FeaturePython)
  n = 1
  ref = Mg_element
FEATURE [App::DocumentObjectGroupPython] B_element006  label="B_element : 006"  # scripted group (container) (typed FeaturePython)
  n = 4
  ref = B_element
FEATURE [App::DocumentObjectGroupPython] O_element061  label="O_element : 032"  # scripted group (container) (typed FeaturePython)
  n = 7
  ref = O_element
FEATURE [App::DocumentObjectGroupPython] G4_MAGNESIUM_TETRABORATE  # scripted group (container) (typed FeaturePython)
  Dunit = g/cm3
  Dvalue = 2.53
  Group = -> [Mg_element008,B_element006,O_element061]
  conduct = 2
  density = 1
  expand = 3
  formula = G4_MAGNESIUM_TETRABORATE
  name = G4_MAGNESIUM_TETRABORATE
  specific = 4
FEATURE [App::DocumentObjectGroupPython] Hg_element001  label="Hg_element : 1"  # scripted group (container) (typed FeaturePython)
  n = 1
  ref = Hg_element
FEATURE [App::DocumentObjectGroupPython] I_element004  label="I_element : 2"  # scripted group (container) (typed FeaturePython)
  n = 2
  ref = I_element
FEATURE [App::DocumentObjectGroupPython] G4_MERCURIC_IODIDE  # scripted group (container) (typed FeaturePython)
  Dunit = g/cm3
  Dvalue = 6.36
  Group = -> [Hg_element001,I_element004]
  conduct = 2
  density = 1
  expand = 3
  formula = G4_MERCURIC_IODIDE
  name = G4_MERCURIC_IODIDE
  specific = 4
FEATURE [App::DocumentObjectGroupPython] C_element059  label="C_element : 032"  # scripted group (container) (typed FeaturePython)
  n = 1
  ref = C_element
FEATURE [App::DocumentObjectGroupPython] H_element053  label="H_element : 028"  # scripted group (container) (typed FeaturePython)
  n = 4
  ref = H_element
FEATURE [App::DocumentObjectGroupPython] G4_METHANE  # scripted group (container) (typed FeaturePython)
  Dunit = g/cm3
  Dvalue = 0.000667151
  Group = -> [C_element059,H_element053]
  conduct = 2
  density = 1
  expand = 3
  formula = G4_METHANE
  name = G4_METHANE
  specific = 4
FEATURE [App::DocumentObjectGroupPython] C_element060  label="C_element : 033"  # scripted group (container) (typed FeaturePython)
  n = 1
  ref = C_element
FEATURE [App::DocumentObjectGroupPython] H_element054  label="H_element : 029"  # scripted group (container) (typed FeaturePython)
  n = 4
  ref = H_element
FEATURE [App::DocumentObjectGroupPython] O_element062  label="O_element : 033"  # scripted group (container) (typed FeaturePython)
  n = 1
  ref = O_element
FEATURE [App::DocumentObjectGroupPython] G4_METHANOL  # scripted group (container) (typed FeaturePython)
  Dunit = g/cm3
  Dvalue = 0.7914
  Group = -> [C_element060,H_element054,O_element062]
  conduct = 2
  density = 1
  expand = 3
  formula = G4_METHANOL
  name = G4_METHANOL
  specific = 4
FEATURE [App::DocumentObjectGroupPython] H_element055  label="H_element : 0.134"  # scripted group (container) (typed FeaturePython)
  n = 0.13404
FEATURE [App::DocumentObjectGroupPython] C_element061  label="C_element : 0.778"  # scripted group (container) (typed FeaturePython)
  n = 0.77796
FEATURE [App::DocumentObjectGroupPython] O_element063  label="O_element : 0.035"  # scripted group (container) (typed FeaturePython)
  n = 0.03502
FEATURE [App::DocumentObjectGroupPython] Mg_element009  label="Mg_element : 0.039"  # scripted group (container) (typed FeaturePython)
  n = 0.038594
FEATURE [App::DocumentObjectGroupPython] Ti_element002  label="Ti_element : 0.014"  # scripted group (container) (typed FeaturePython)
  n = 0.014386
FEATURE [App::DocumentObjectGroupPython] G4_MIX_D_WAX  # scripted group (container) (typed FeaturePython)
  Dunit = g/cm3
  Dvalue = 0.99
  Group = -> [H_element055,C_element061,O_element063,Mg_element009,Ti_element002]
  conduct = 2
  density = 1
  expand = 3
  formula = G4_MIX_D_WAX
  name = G4_MIX_D_WAX
  specific = 4
FEATURE [App::DocumentObjectGroupPython] H_element056  label="H_element : 0.135"  # scripted group (container) (typed FeaturePython)
  n = 0.081192
FEATURE [App::DocumentObjectGroupPython] C_element062  label="C_element : 0.583"  # scripted group (container) (typed FeaturePython)
  n = 0.583442
FEATURE [App::DocumentObjectGroupPython] N_element024  label="N_element : 0.018"  # scripted group (container) (typed FeaturePython)
  n = 0.017798
FEATURE [App::DocumentObjectGroupPython] O_element064  label="O_element : 0.186"  # scripted group (container) (typed FeaturePython)
  n = 0.186381
FEATURE [App::DocumentObjectGroupPython] Mg_element010  label="Mg_element : 0.130"  # scripted group (container) (typed FeaturePython)
  n = 0.130287
FEATURE [App::DocumentObjectGroupPython] Cl_element015  label="Cl_element : 0.588"  # scripted group (container) (typed FeaturePython)
  n = 0.0009
FEATURE [App::DocumentObjectGroupPython] G4_MS20_TISSUE  # scripted group (container) (typed FeaturePython)
  Dunit = g/cm3
  Dvalue = 1
  Group = -> [H_element056,C_element062,N_element024,O_element064,Mg_element010,Cl_element015]
  conduct = 2
  density = 1
  expand = 3
  formula = G4_MS20_TISSUE
  name = G4_MS20_TISSUE
  specific = 4
FEATURE [App::DocumentObjectGroupPython] H_element057  label="H_element : 0.136"  # scripted group (container) (typed FeaturePython)
  n = 0.102
FEATURE [App::DocumentObjectGroupPython] C_element063  label="C_element : 0.143"  # scripted group (container) (typed FeaturePython)
  n = 0.143
FEATURE [App::DocumentObjectGroupPython] N_element025  label="N_element : 0.034"  # scripted group (container) (typed FeaturePython)
  n = 0.034
FEATURE [App::DocumentObjectGroupPython] O_element065  label="O_element : 0.710"  # scripted group (container) (typed FeaturePython)
  n = 0.71
FEATURE [App::DocumentObjectGroupPython] Na_element011  label="Na_element : 0.098"  # scripted group (container) (typed FeaturePython)
  n = 0.001
FEATURE [App::DocumentObjectGroupPython] P_element007  label="P_element : 0.002"  # scripted group (container) (typed FeaturePython)
  n = 0.002
FEATURE [App::DocumentObjectGroupPython] S_element017  label="S_element : 0.018"  # scripted group (container) (typed FeaturePython)
  n = 0.003
FEATURE [App::DocumentObjectGroupPython] Cl_element016  label="Cl_element : 0.589"  # scripted group (container) (typed FeaturePython)
  n = 0.001
FEATURE [App::DocumentObjectGroupPython] K_element006  label="K_element : 0.004"  # scripted group (container) (typed FeaturePython)
  n = 0.004
FEATURE [App::DocumentObjectGroupPython] G4_MUSCLE_SKELETAL_ICRP  # scripted group (container) (typed FeaturePython)
  Dunit = g/cm3
  Dvalue = 1.05
  Group = -> [H_element057,C_element063,N_element025,O_element065,Na_element011,P_element007,S_element017,Cl_element016,K_element006]
  conduct = 2
  density = 1
  expand = 3
  formula = G4_MUSCLE_SKELETAL_ICRP
  name = G4_MUSCLE_SKELETAL_ICRP
  specific = 4
FEATURE [App::DocumentObjectGroupPython] H_element058  label="H_element : 0.137"  # scripted group (container) (typed FeaturePython)
  n = 0.102102
FEATURE [App::DocumentObjectGroupPython] C_element064  label="C_element : 0.123"  # scripted group (container) (typed FeaturePython)
  n = 0.123123
FEATURE [App::DocumentObjectGroupPython] N_element026  label="N_element : 0.756"  # scripted group (container) (typed FeaturePython)
  n = 0.035035
FEATURE [App::DocumentObjectGroupPython] O_element066  label="O_element : 0.730"  # scripted group (container) (typed FeaturePython)
  n = 0.72973
FEATURE [App::DocumentObjectGroupPython] Na_element012  label="Na_element : 0.099"  # scripted group (container) (typed FeaturePython)
  n = 0.001001
FEATURE [App::DocumentObjectGroupPython] P_element008  label="P_element : 0.106"  # scripted group (container) (typed FeaturePython)
  n = 0.002002
FEATURE [App::DocumentObjectGroupPython] S_element018  label="S_element : 0.019"  # scripted group (container) (typed FeaturePython)
  n = 0.004004
FEATURE [App::DocumentObjectGroupPython] K_element007  label="K_element : 0.016"  # scripted group (container) (typed FeaturePython)
  n = 0.003003
FEATURE [App::DocumentObjectGroupPython] G4_MUSCLE_STRIATED_ICRU  # scripted group (container) (typed FeaturePython)
  Dunit = g/cm3
  Dvalue = 1.04
  Group = -> [H_element058,C_element064,N_element026,O_element066,Na_element012,P_element008,S_element018,K_element007]
  conduct = 2
  density = 1
  expand = 3
  formula = G4_MUSCLE_STRIATED_ICRU
  name = G4_MUSCLE_STRIATED_ICRU
  specific = 4
FEATURE [App::DocumentObjectGroupPython] H_element059  label="H_element : 0.098"  # scripted group (container) (typed FeaturePython)
  n = 0.0982341
FEATURE [App::DocumentObjectGroupPython] C_element065  label="C_element : 0.156"  # scripted group (container) (typed FeaturePython)
  n = 0.156214
FEATURE [App::DocumentObjectGroupPython] N_element027  label="N_element : 0.757"  # scripted group (container) (typed FeaturePython)
  n = 0.035451
FEATURE [App::DocumentObjectGroupPython] O_element067  label="O_element : 0.880"  # scripted group (container) (typed FeaturePython)
  n = 0.710101
FEATURE [App::DocumentObjectGroupPython] G4_MUSCLE_WITH_SUCROSE  # scripted group (container) (typed FeaturePython)
  Dunit = g/cm3
  Dvalue = 1.11
  Group = -> [H_element059,C_element065,N_element027,O_element067]
  conduct = 2
  density = 1
  expand = 3
  formula = G4_MUSCLE_WITH_SUCROSE
  name = G4_MUSCLE_WITH_SUCROSE
  specific = 4
FEATURE [App::DocumentObjectGroupPython] H_element060  label="H_element : 0.138"  # scripted group (container) (typed FeaturePython)
  n = 0.101969
FEATURE [App::DocumentObjectGroupPython] C_element066  label="C_element : 0.120"  # scripted group (container) (typed FeaturePython)
  n = 0.120058
FEATURE [App::DocumentObjectGroupPython] N_element028  label="N_element : 0.758"  # scripted group (container) (typed FeaturePython)
  n = 0.035451
FEATURE [App::DocumentObjectGroupPython] O_element068  label="O_element : 0.743"  # scripted group (container) (typed FeaturePython)
  n = 0.742522
FEATURE [App::DocumentObjectGroupPython] G4_MUSCLE_WITHOUT_SUCROSE  # scripted group (container) (typed FeaturePython)
  Dunit = g/cm3
  Dvalue = 1.07
  Group = -> [H_element060,C_element066,N_element028,O_element068]
  conduct = 2
  density = 1
  expand = 3
  formula = G4_MUSCLE_WITHOUT_SUCROSE
  name = G4_MUSCLE_WITHOUT_SUCROSE
  specific = 4
FEATURE [App::DocumentObjectGroupPython] C_element067  label="C_element : 10"  # scripted group (container) (typed FeaturePython)
  n = 10
  ref = C_element
FEATURE [App::DocumentObjectGroupPython] H_element061  label="H_element : 030"  # scripted group (container) (typed FeaturePython)
  n = 8
  ref = H_element
FEATURE [App::DocumentObjectGroupPython] G4_NAPHTHALENE  # scripted group (container) (typed FeaturePython)
  Dunit = g/cm3
  Dvalue = 1.145
  Group = -> [C_element067,H_element061]
  conduct = 2
  density = 1
  expand = 3
  formula = G4_NAPHTHALENE
  name = G4_NAPHTHALENE
  specific = 4
FEATURE [App::DocumentObjectGroupPython] C_element068  label="C_element : 034"  # scripted group (container) (typed FeaturePython)
  n = 6
  ref = C_element
FEATURE [App::DocumentObjectGroupPython] H_element062  label="H_element : 031"  # scripted group (container) (typed FeaturePython)
  n = 5
  ref = H_element
FEATURE [App::DocumentObjectGroupPython] N_element029  label="N_element : 012"  # scripted group (container) (typed FeaturePython)
  n = 1
  ref = N_element
FEATURE [App::DocumentObjectGroupPython] O_element069  label="O_element : 034"  # scripted group (container) (typed FeaturePython)
  n = 2
  ref = O_element
FEATURE [App::DocumentObjectGroupPython] G4_NITROBENZENE  # scripted group (container) (typed FeaturePython)
  Dunit = g/cm3
  Dvalue = 1.19867
  Group = -> [C_element068,H_element062,N_element029,O_element069]
  conduct = 2
  density = 1
  expand = 3
  formula = G4_NITROBENZENE
  name = G4_NITROBENZENE
  specific = 4
FEATURE [App::DocumentObjectGroupPython] N_element030  label="N_element : 013"  # scripted group (container) (typed FeaturePython)
  n = 2
  ref = N_element
FEATURE [App::DocumentObjectGroupPython] O_element070  label="O_element : 035"  # scripted group (container) (typed FeaturePython)
  n = 1
  ref = O_element
FEATURE [App::DocumentObjectGroupPython] G4_NITROUS_OXIDE  # scripted group (container) (typed FeaturePython)
  Dunit = g/cm3
  Dvalue = 0.00183094
  Group = -> [N_element030,O_element070]
  conduct = 2
  density = 1
  expand = 3
  formula = G4_NITROUS_OXIDE
  name = G4_NITROUS_OXIDE
  specific = 4
FEATURE [App::DocumentObjectGroupPython] H_element063  label="H_element : 0.104"  # scripted group (container) (typed FeaturePython)
  n = 0.103509
FEATURE [App::DocumentObjectGroupPython] C_element069  label="C_element : 0.648"  # scripted group (container) (typed FeaturePython)
  n = 0.648416
FEATURE [App::DocumentObjectGroupPython] N_element031  label="N_element : 0.100"  # scripted group (container) (typed FeaturePython)
  n = 0.0995361
FEATURE [App::DocumentObjectGroupPython] O_element071  label="O_element : 0.149"  # scripted group (container) (typed FeaturePython)
  n = 0.148539
FEATURE [App::DocumentObjectGroupPython] G4_NYLON_8062  label="G4_NYLON-8062"  # scripted group (container) (typed FeaturePython)
  Dunit = g/cm3
  Dvalue = 1.08
  Group = -> [H_element063,C_element069,N_element031,O_element071]
  conduct = 2
  density = 1
  expand = 3
  formula = G4_NYLON-8062
  name = G4_NYLON-8062
  specific = 4
FEATURE [App::DocumentObjectGroupPython] C_element070  label="C_element : 035"  # scripted group (container) (typed FeaturePython)
  n = 6
  ref = C_element
FEATURE [App::DocumentObjectGroupPython] H_element064  label="H_element : 11"  # scripted group (container) (typed FeaturePython)
  n = 11
  ref = H_element
FEATURE [App::DocumentObjectGroupPython] N_element032  label="N_element : 014"  # scripted group (container) (typed FeaturePython)
  n = 1
  ref = N_element
FEATURE [App::DocumentObjectGroupPython] O_element072  label="O_element : 036"  # scripted group (container) (typed FeaturePython)
  n = 1
  ref = O_element
FEATURE [App::DocumentObjectGroupPython] G4_NYLON_6_6  label="G4_NYLON-6-6"  # scripted group (container) (typed FeaturePython)
  Dunit = g/cm3
  Dvalue = 1.14
  Group = -> [C_element070,H_element064,N_element032,O_element072]
  conduct = 2
  density = 1
  expand = 3
  formula = G4_NYLON-6-6
  name = G4_NYLON-6-6
  specific = 4
FEATURE [App::DocumentObjectGroupPython] H_element065  label="H_element : 0.139"  # scripted group (container) (typed FeaturePython)
  n = 0.107062
FEATURE [App::DocumentObjectGroupPython] C_element071  label="C_element : 0.680"  # scripted group (container) (typed FeaturePython)
  n = 0.680449
FEATURE [App::DocumentObjectGroupPython] N_element033  label="N_element : 0.099"  # scripted group (container) (typed FeaturePython)
  n = 0.099189
FEATURE [App::DocumentObjectGroupPython] O_element073  label="O_element : 0.113"  # scripted group (container) (typed FeaturePython)
  n = 0.1133
FEATURE [App::DocumentObjectGroupPython] G4_NYLON_6_10  label="G4_NYLON-6-10"  # scripted group (container) (typed FeaturePython)
  Dunit = g/cm3
  Dvalue = 1.14
  Group = -> [H_element065,C_element071,N_element033,O_element073]
  conduct = 2
  density = 1
  expand = 3
  formula = G4_NYLON-6-10
  name = G4_NYLON-6-10
  specific = 4
FEATURE [App::DocumentObjectGroupPython] H_element066  label="H_element : 0.140"  # scripted group (container) (typed FeaturePython)
  n = 0.115476
FEATURE [App::DocumentObjectGroupPython] C_element072  label="C_element : 0.721"  # scripted group (container) (typed FeaturePython)
  n = 0.720818
FEATURE [App::DocumentObjectGroupPython] N_element034  label="N_element : 0.076"  # scripted group (container) (typed FeaturePython)
  n = 0.0764169
FEATURE [App::DocumentObjectGroupPython] O_element074  label="O_element : 0.087"  # scripted group (container) (typed FeaturePython)
  n = 0.0872889
FEATURE [App::DocumentObjectGroupPython] G4_NYLON_11_RILSAN  label="G4_NYLON-11_RILSAN"  # scripted group (container) (typed FeaturePython)
  Dunit = g/cm3
  Dvalue = 1.425
  Group = -> [H_element066,C_element072,N_element034,O_element074]
  conduct = 2
  density = 1
  expand = 3
  formula = G4_NYLON-11_RILSAN
  name = G4_NYLON-11_RILSAN
  specific = 4
FEATURE [App::DocumentObjectGroupPython] C_element073  label="C_element : 8"  # scripted group (container) (typed FeaturePython)
  n = 8
  ref = C_element
FEATURE [App::DocumentObjectGroupPython] H_element067  label="H_element : 18"  # scripted group (container) (typed FeaturePython)
  n = 18
  ref = H_element
FEATURE [App::DocumentObjectGroupPython] G4_OCTANE  # scripted group (container) (typed FeaturePython)
  Dunit = g/cm3
  Dvalue = 0.7026
  Group = -> [C_element073,H_element067]
  conduct = 2
  density = 1
  expand = 3
  formula = G4_OCTANE
  name = G4_OCTANE
  specific = 4
FEATURE [App::DocumentObjectGroupPython] C_element074  label="C_element : 25"  # scripted group (container) (typed FeaturePython)
  n = 25
  ref = C_element
FEATURE [App::DocumentObjectGroupPython] H_element068  label="H_element : 52"  # scripted group (container) (typed FeaturePython)
  n = 52
  ref = H_element
FEATURE [App::DocumentObjectGroupPython] G4_PARAFFIN  # scripted group (container) (typed FeaturePython)
  Dunit = g/cm3
  Dvalue = 0.93
  Group = -> [C_element074,H_element068]
  conduct = 2
  density = 1
  expand = 3
  formula = G4_PARAFFIN
  name = G4_PARAFFIN
  specific = 4
FEATURE [App::DocumentObjectGroupPython] C_element075  label="C_element : 036"  # scripted group (container) (typed FeaturePython)
  n = 5
  ref = C_element
FEATURE [App::DocumentObjectGroupPython] H_element069  label="H_element : 032"  # scripted group (container) (typed FeaturePython)
  n = 12
  ref = H_element
FEATURE [App::DocumentObjectGroupPython] G4_N_PENTANE  label="G4_N-PENTANE"  # scripted group (container) (typed FeaturePython)
  Dunit = g/cm3
  Dvalue = 0.6262
  Group = -> [C_element075,H_element069]
  conduct = 2
  density = 1
  expand = 3
  formula = G4_N-PENTANE
  name = G4_N-PENTANE
  specific = 4
FEATURE [App::DocumentObjectGroupPython] H_element070  label="H_element : 0.014"  # scripted group (container) (typed FeaturePython)
  n = 0.0141
FEATURE [App::DocumentObjectGroupPython] C_element076  label="C_element : 0.072"  # scripted group (container) (typed FeaturePython)
  n = 0.072261
FEATURE [App::DocumentObjectGroupPython] N_element035  label="N_element : 0.019"  # scripted group (container) (typed FeaturePython)
  n = 0.01932
FEATURE [App::DocumentObjectGroupPython] O_element075  label="O_element : 0.066"  # scripted group (container) (typed FeaturePython)
  n = 0.066101
FEATURE [App::DocumentObjectGroupPython] S_element019  label="S_element : 0.020"  # scripted group (container) (typed FeaturePython)
  n = 0.00189
FEATURE [App::DocumentObjectGroupPython] Br_element004  label="Br_element : 0.349"  # scripted group (container) (typed FeaturePython)
  n = 0.349103
FEATURE [App::DocumentObjectGroupPython] Ag_element001  label="Ag_element : 0.474"  # scripted group (container) (typed FeaturePython)
  n = 0.474105
FEATURE [App::DocumentObjectGroupPython] I_element005  label="I_element : 0.003"  # scripted group (container) (typed FeaturePython)
  n = 0.00312
FEATURE [App::DocumentObjectGroupPython] G4_PHOTO_EMULSION  # scripted group (container) (typed FeaturePython)
  Dunit = g/cm3
  Dvalue = 3.815
  Group = -> [H_element070,C_element076,N_element035,O_element075,S_element019,Br_element004,Ag_element001,I_element005]
  conduct = 2
  density = 1
  expand = 3
  formula = G4_PHOTO_EMULSION
  name = G4_PHOTO_EMULSION
  specific = 4
FEATURE [App::DocumentObjectGroupPython] C_element077  label="C_element : 9"  # scripted group (container) (typed FeaturePython)
  n = 9
  ref = C_element
FEATURE [App::DocumentObjectGroupPython] H_element071  label="H_element : 033"  # scripted group (container) (typed FeaturePython)
  n = 10
  ref = H_element
FEATURE [App::DocumentObjectGroupPython] G4_PLASTIC_SC_VINYLTOLUENE  # scripted group (container) (typed FeaturePython)
  Dunit = g/cm3
  Dvalue = 1.032
  Group = -> [C_element077,H_element071]
  conduct = 2
  density = 1
  expand = 3
  formula = G4_PLASTIC_SC_VINYLTOLUENE
  name = G4_PLASTIC_SC_VINYLTOLUENE
  specific = 4
FEATURE [App::DocumentObjectGroupPython] Pu_element001  label="Pu_element : 1"  # scripted group (container) (typed FeaturePython)
  n = 1
  ref = Pu_element
FEATURE [App::DocumentObjectGroupPython] O_element076  label="O_element : 037"  # scripted group (container) (typed FeaturePython)
  n = 2
  ref = O_element
FEATURE [App::DocumentObjectGroupPython] G4_PLUTONIUM_DIOXIDE  # scripted group (container) (typed FeaturePython)
  Dunit = g/cm3
  Dvalue = 11.46
  Group = -> [Pu_element001,O_element076]
  conduct = 2
  density = 1
  expand = 3
  formula = G4_PLUTONIUM_DIOXIDE
  name = G4_PLUTONIUM_DIOXIDE
  specific = 4
FEATURE [App::DocumentObjectGroupPython] C_element078  label="C_element : 037"  # scripted group (container) (typed FeaturePython)
  n = 3
  ref = C_element
FEATURE [App::DocumentObjectGroupPython] H_element072  label="H_element : 034"  # scripted group (container) (typed FeaturePython)
  n = 3
  ref = H_element
FEATURE [App::DocumentObjectGroupPython] N_element036  label="N_element : 015"  # scripted group (container) (typed FeaturePython)
  n = 1
  ref = N_element
FEATURE [App::DocumentObjectGroupPython] G4_POLYACRYLONITRILE  # scripted group (container) (typed FeaturePython)
  Dunit = g/cm3
  Dvalue = 1.17
  Group = -> [C_element078,H_element072,N_element036]
  conduct = 2
  density = 1
  expand = 3
  formula = G4_POLYACRYLONITRILE
  name = G4_POLYACRYLONITRILE
  specific = 4
FEATURE [App::DocumentObjectGroupPython] C_element079  label="C_element : 16"  # scripted group (container) (typed FeaturePython)
  n = 16
  ref = C_element
FEATURE [App::DocumentObjectGroupPython] H_element073  label="H_element : 035"  # scripted group (container) (typed FeaturePython)
  n = 14
  ref = H_element
FEATURE [App::DocumentObjectGroupPython] O_element077  label="O_element : 038"  # scripted group (container) (typed FeaturePython)
  n = 3
  ref = O_element
FEATURE [App::DocumentObjectGroupPython] G4_POLYCARBONATE  # scripted group (container) (typed FeaturePython)
  Dunit = g/cm3
  Dvalue = 1.2
  Group = -> [C_element079,H_element073,O_element077]
  conduct = 2
  density = 1
  expand = 3
  formula = G4_POLYCARBONATE
  name = G4_POLYCARBONATE
  specific = 4
FEATURE [App::DocumentObjectGroupPython] C_element080  label="C_element : 038"  # scripted group (container) (typed FeaturePython)
  n = 8
  ref = C_element
FEATURE [App::DocumentObjectGroupPython] H_element074  label="H_element : 036"  # scripted group (container) (typed FeaturePython)
  n = 7
  ref = H_element
FEATURE [App::DocumentObjectGroupPython] Cl_element017  label="Cl_element : 007"  # scripted group (container) (typed FeaturePython)
  n = 1
  ref = Cl_element
FEATURE [App::DocumentObjectGroupPython] G4_POLYCHLOROSTYRENE  # scripted group (container) (typed FeaturePython)
  Dunit = g/cm3
  Dvalue = 1.3
  Group = -> [C_element080,H_element074,Cl_element017]
  conduct = 2
  density = 1
  expand = 3
  formula = G4_POLYCHLOROSTYRENE
  name = G4_POLYCHLOROSTYRENE
  specific = 4
FEATURE [App::DocumentObjectGroupPython] C_element081  label="C_element : 039"  # scripted group (container) (typed FeaturePython)
  n = 1
  ref = C_element
FEATURE [App::DocumentObjectGroupPython] H_element075  label="H_element : 037"  # scripted group (container) (typed FeaturePython)
  n = 2
  ref = H_element
FEATURE [App::DocumentObjectGroupPython] G4_POLYETHYLENE  # scripted group (container) (typed FeaturePython)
  Dunit = g/cm3
  Dvalue = 0.94
  Group = -> [C_element081,H_element075]
  conduct = 2
  density = 1
  expand = 3
  formula = G4_POLYETHYLENE
  name = G4_POLYETHYLENE
  specific = 4
FEATURE [App::DocumentObjectGroupPython] C_element082  label="C_element : 040"  # scripted group (container) (typed FeaturePython)
  n = 10
  ref = C_element
FEATURE [App::DocumentObjectGroupPython] H_element076  label="H_element : 038"  # scripted group (container) (typed FeaturePython)
  n = 8
  ref = H_element
FEATURE [App::DocumentObjectGroupPython] O_element078  label="O_element : 039"  # scripted group (container) (typed FeaturePython)
  n = 4
  ref = O_element
FEATURE [App::DocumentObjectGroupPython] G4_MYLAR  # scripted group (container) (typed FeaturePython)
  Dunit = g/cm3
  Dvalue = 1.4
  Group = -> [C_element082,H_element076,O_element078]
  conduct = 2
  density = 1
  expand = 3
  formula = G4_MYLAR
  name = G4_MYLAR
  specific = 4
FEATURE [App::DocumentObjectGroupPython] C_element083  label="C_element : 041"  # scripted group (container) (typed FeaturePython)
  n = 5
  ref = C_element
FEATURE [App::DocumentObjectGroupPython] H_element077  label="H_element : 039"  # scripted group (container) (typed FeaturePython)
  n = 8
  ref = H_element
FEATURE [App::DocumentObjectGroupPython] O_element079  label="O_element : 040"  # scripted group (container) (typed FeaturePython)
  n = 2
  ref = O_element
FEATURE [App::DocumentObjectGroupPython] G4_PLEXIGLASS  # scripted group (container) (typed FeaturePython)
  Dunit = g/cm3
  Dvalue = 1.19
  Group = -> [C_element083,H_element077,O_element079]
  conduct = 2
  density = 1
  expand = 3
  formula = G4_PLEXIGLASS
  name = G4_PLEXIGLASS
  specific = 4
FEATURE [App::DocumentObjectGroupPython] C_element084  label="C_element : 042"  # scripted group (container) (typed FeaturePython)
  n = 1
  ref = C_element
FEATURE [App::DocumentObjectGroupPython] H_element078  label="H_element : 040"  # scripted group (container) (typed FeaturePython)
  n = 2
  ref = H_element
FEATURE [App::DocumentObjectGroupPython] O_element080  label="O_element : 041"  # scripted group (container) (typed FeaturePython)
  n = 1
  ref = O_element
FEATURE [App::DocumentObjectGroupPython] G4_POLYOXYMETHYLENE  # scripted group (container) (typed FeaturePython)
  Dunit = g/cm3
  Dvalue = 1.425
  Group = -> [C_element084,H_element078,O_element080]
  conduct = 2
  density = 1
  expand = 3
  formula = G4_POLYOXYMETHYLENE
  name = G4_POLYOXYMETHYLENE
  specific = 4
FEATURE [App::DocumentObjectGroupPython] C_element085  label="C_element : 043"  # scripted group (container) (typed FeaturePython)
  n = 2
  ref = C_element
FEATURE [App::DocumentObjectGroupPython] H_element079  label="H_element : 041"  # scripted group (container) (typed FeaturePython)
  n = 4
  ref = H_element
FEATURE [App::DocumentObjectGroupPython] G4_POLYPROPYLENE  # scripted group (container) (typed FeaturePython)
  Dunit = g/cm3
  Dvalue = 0.9
  Group = -> [C_element085,H_element079]
  conduct = 2
  density = 1
  expand = 3
  formula = G4_POLYPROPYLENE
  name = G4_POLYPROPYLENE
  specific = 4
FEATURE [App::DocumentObjectGroupPython] C_element086  label="C_element : 044"  # scripted group (container) (typed FeaturePython)
  n = 8
  ref = C_element
FEATURE [App::DocumentObjectGroupPython] H_element080  label="H_element : 042"  # scripted group (container) (typed FeaturePython)
  n = 8
  ref = H_element
FEATURE [App::DocumentObjectGroupPython] G4_POLYSTYRENE  # scripted group (container) (typed FeaturePython)
  Dunit = g/cm3
  Dvalue = 1.06
  Group = -> [C_element086,H_element080]
  conduct = 2
  density = 1
  expand = 3
  formula = G4_POLYSTYRENE
  name = G4_POLYSTYRENE
  specific = 4
FEATURE [App::DocumentObjectGroupPython] C_element087  label="C_element : 045"  # scripted group (container) (typed FeaturePython)
  n = 2
  ref = C_element
FEATURE [App::DocumentObjectGroupPython] F_element014  label="F_element : 4"  # scripted group (container) (typed FeaturePython)
  n = 4
  ref = F_element
FEATURE [App::DocumentObjectGroupPython] G4_TEFLON  # scripted group (container) (typed FeaturePython)
  Dunit = g/cm3
  Dvalue = 2.2
  Group = -> [C_element087,F_element014]
  conduct = 2
  density = 1
  expand = 3
  formula = G4_TEFLON
  name = G4_TEFLON
  specific = 4
FEATURE [App::DocumentObjectGroupPython] C_element088  label="C_element : 046"  # scripted group (container) (typed FeaturePython)
  n = 2
  ref = C_element
FEATURE [App::DocumentObjectGroupPython] F_element015  label="F_element : 006"  # scripted group (container) (typed FeaturePython)
  n = 3
  ref = F_element
FEATURE [App::DocumentObjectGroupPython] Cl_element018  label="Cl_element : 008"  # scripted group (container) (typed FeaturePython)
  n = 1
  ref = Cl_element
FEATURE [App::DocumentObjectGroupPython] G4_POLYTRIFLUOROCHLOROETHYLENE  # scripted group (container) (typed FeaturePython)
  Dunit = g/cm3
  Dvalue = 2.1
  Group = -> [C_element088,F_element015,Cl_element018]
  conduct = 2
  density = 1
  expand = 3
  formula = G4_POLYTRIFLUOROCHLOROETHYLENE
  name = G4_POLYTRIFLUOROCHLOROETHYLENE
  specific = 4
FEATURE [App::DocumentObjectGroupPython] C_element089  label="C_element : 047"  # scripted group (container) (typed FeaturePython)
  n = 4
  ref = C_element
FEATURE [App::DocumentObjectGroupPython] H_element081  label="H_element : 043"  # scripted group (container) (typed FeaturePython)
  n = 6
  ref = H_element
FEATURE [App::DocumentObjectGroupPython] O_element081  label="O_element : 042"  # scripted group (container) (typed FeaturePython)
  n = 2
  ref = O_element
FEATURE [App::DocumentObjectGroupPython] G4_POLYVINYL_ACETATE  # scripted group (container) (typed FeaturePython)
  Dunit = g/cm3
  Dvalue = 1.19
  Group = -> [C_element089,H_element081,O_element081]
  conduct = 2
  density = 1
  expand = 3
  formula = G4_POLYVINYL_ACETATE
  name = G4_POLYVINYL_ACETATE
  specific = 4
FEATURE [App::DocumentObjectGroupPython] C_element090  label="C_element : 048"  # scripted group (container) (typed FeaturePython)
  n = 2
  ref = C_element
FEATURE [App::DocumentObjectGroupPython] H_element082  label="H_element : 044"  # scripted group (container) (typed FeaturePython)
  n = 4
  ref = H_element
FEATURE [App::DocumentObjectGroupPython] O_element082  label="O_element : 043"  # scripted group (container) (typed FeaturePython)
  n = 1
  ref = O_element
FEATURE [App::DocumentObjectGroupPython] G4_POLYVINYL_ALCOHOL  # scripted group (container) (typed FeaturePython)
  Dunit = g/cm3
  Dvalue = 1.3
  Group = -> [C_element090,H_element082,O_element082]
  conduct = 2
  density = 1
  expand = 3
  formula = G4_POLYVINYL_ALCOHOL
  name = G4_POLYVINYL_ALCOHOL
  specific = 4
FEATURE [App::DocumentObjectGroupPython] C_element091  label="C_element : 049"  # scripted group (container) (typed FeaturePython)
  n = 8
  ref = C_element
FEATURE [App::DocumentObjectGroupPython] H_element083  label="H_element : 045"  # scripted group (container) (typed FeaturePython)
  n = 14
  ref = H_element
FEATURE [App::DocumentObjectGroupPython] O_element083  label="O_element : 044"  # scripted group (container) (typed FeaturePython)
  n = 2
  ref = O_element
FEATURE [App::DocumentObjectGroupPython] G4_POLYVINYL_BUTYRAL  # scripted group (container) (typed FeaturePython)
  Dunit = g/cm3
  Dvalue = 1.12
  Group = -> [C_element091,H_element083,O_element083]
  conduct = 2
  density = 1
  expand = 3
  formula = G4_POLYVINYL_BUTYRAL
  name = G4_POLYVINYL_BUTYRAL
  specific = 4
FEATURE [App::DocumentObjectGroupPython] C_element092  label="C_element : 050"  # scripted group (container) (typed FeaturePython)
  n = 2
  ref = C_element
FEATURE [App::DocumentObjectGroupPython] H_element084  label="H_element : 046"  # scripted group (container) (typed FeaturePython)
  n = 3
  ref = H_element
FEATURE [App::DocumentObjectGroupPython] Cl_element019  label="Cl_element : 009"  # scripted group (container) (typed FeaturePython)
  n = 1
  ref = Cl_element
FEATURE [App::DocumentObjectGroupPython] G4_POLYVINYL_CHLORIDE  # scripted group (container) (typed FeaturePython)
  Dunit = g/cm3
  Dvalue = 1.3
  Group = -> [C_element092,H_element084,Cl_element019]
  conduct = 2
  density = 1
  expand = 3
  formula = G4_POLYVINYL_CHLORIDE
  name = G4_POLYVINYL_CHLORIDE
  specific = 4
FEATURE [App::DocumentObjectGroupPython] C_element093  label="C_element : 051"  # scripted group (container) (typed FeaturePython)
  n = 2
  ref = C_element
FEATURE [App::DocumentObjectGroupPython] H_element085  label="H_element : 047"  # scripted group (container) (typed FeaturePython)
  n = 2
  ref = H_element
FEATURE [App::DocumentObjectGroupPython] Cl_element020  label="Cl_element : 010"  # scripted group (container) (typed FeaturePython)
  n = 2
  ref = Cl_element
FEATURE [App::DocumentObjectGroupPython] G4_POLYVINYLIDENE_CHLORIDE  # scripted group (container) (typed FeaturePython)
  Dunit = g/cm3
  Dvalue = 1.7
  Group = -> [C_element093,H_element085,Cl_element020]
  conduct = 2
  density = 1
  expand = 3
  formula = G4_POLYVINYLIDENE_CHLORIDE
  name = G4_POLYVINYLIDENE_CHLORIDE
  specific = 4
FEATURE [App::DocumentObjectGroupPython] C_element094  label="C_element : 052"  # scripted group (container) (typed FeaturePython)
  n = 2
  ref = C_element
FEATURE [App::DocumentObjectGroupPython] H_element086  label="H_element : 048"  # scripted group (container) (typed FeaturePython)
  n = 2
  ref = H_element
FEATURE [App::DocumentObjectGroupPython] F_element016  label="F_element : 007"  # scripted group (container) (typed FeaturePython)
  n = 2
  ref = F_element
FEATURE [App::DocumentObjectGroupPython] G4_POLYVINYLIDENE_FLUORIDE  # scripted group (container) (typed FeaturePython)
  Dunit = g/cm3
  Dvalue = 1.76
  Group = -> [C_element094,H_element086,F_element016]
  conduct = 2
  density = 1
  expand = 3
  formula = G4_POLYVINYLIDENE_FLUORIDE
  name = G4_POLYVINYLIDENE_FLUORIDE
  specific = 4
FEATURE [App::DocumentObjectGroupPython] C_element095  label="C_element : 053"  # scripted group (container) (typed FeaturePython)
  n = 6
  ref = C_element
FEATURE [App::DocumentObjectGroupPython] H_element087  label="H_element : 9"  # scripted group (container) (typed FeaturePython)
  n = 9
  ref = H_element
FEATURE [App::DocumentObjectGroupPython] N_element037  label="N_element : 016"  # scripted group (container) (typed FeaturePython)
  n = 1
  ref = N_element
FEATURE [App::DocumentObjectGroupPython] O_element084  label="O_element : 045"  # scripted group (container) (typed FeaturePython)
  n = 1
  ref = O_element
FEATURE [App::DocumentObjectGroupPython] G4_POLYVINYL_PYRROLIDONE  # scripted group (container) (typed FeaturePython)
  Dunit = g/cm3
  Dvalue = 1.25
  Group = -> [C_element095,H_element087,N_element037,O_element084]
  conduct = 2
  density = 1
  expand = 3
  formula = G4_POLYVINYL_PYRROLIDONE
  name = G4_POLYVINYL_PYRROLIDONE
  specific = 4
FEATURE [App::DocumentObjectGroupPython] K_element008  label="K_element : 1"  # scripted group (container) (typed FeaturePython)
  n = 1
  ref = K_element
FEATURE [App::DocumentObjectGroupPython] I_element006  label="I_element : 003"  # scripted group (container) (typed FeaturePython)
  n = 1
  ref = I_element
FEATURE [App::DocumentObjectGroupPython] G4_POTASSIUM_IODIDE  # scripted group (container) (typed FeaturePython)
  Dunit = g/cm3
  Dvalue = 3.13
  Group = -> [K_element008,I_element006]
  conduct = 2
  density = 1
  expand = 3
  formula = G4_POTASSIUM_IODIDE
  name = G4_POTASSIUM_IODIDE
  specific = 4
FEATURE [App::DocumentObjectGroupPython] K_element009  label="K_element : 2"  # scripted group (container) (typed FeaturePython)
  n = 2
  ref = K_element
FEATURE [App::DocumentObjectGroupPython] O_element085  label="O_element : 046"  # scripted group (container) (typed FeaturePython)
  n = 1
  ref = O_element
FEATURE [App::DocumentObjectGroupPython] G4_POTASSIUM_OXIDE  # scripted group (container) (typed FeaturePython)
  Dunit = g/cm3
  Dvalue = 2.32
  Group = -> [K_element009,O_element085]
  conduct = 2
  density = 1
  expand = 3
  formula = G4_POTASSIUM_OXIDE
  name = G4_POTASSIUM_OXIDE
  specific = 4
FEATURE [App::DocumentObjectGroupPython] C_element096  label="C_element : 054"  # scripted group (container) (typed FeaturePython)
  n = 3
  ref = C_element
FEATURE [App::DocumentObjectGroupPython] H_element088  label="H_element : 049"  # scripted group (container) (typed FeaturePython)
  n = 8
  ref = H_element
FEATURE [App::DocumentObjectGroupPython] G4_PROPANE  # scripted group (container) (typed FeaturePython)
  Dunit = g/cm3
  Dvalue = 0.00187939
  Group = -> [C_element096,H_element088]
  conduct = 2
  density = 1
  expand = 3
  formula = G4_PROPANE
  name = G4_PROPANE
  specific = 4
FEATURE [App::DocumentObjectGroupPython] C_element097  label="C_element : 055"  # scripted group (container) (typed FeaturePython)
  n = 3
  ref = C_element
FEATURE [App::DocumentObjectGroupPython] H_element089  label="H_element : 050"  # scripted group (container) (typed FeaturePython)
  n = 8
  ref = H_element
FEATURE [App::DocumentObjectGroupPython] G4_lPROPANE  # scripted group (container) (typed FeaturePython)
  Dunit = g/cm3
  Dvalue = 0.43
  Group = -> [C_element097,H_element089]
  conduct = 2
  density = 1
  expand = 3
  formula = G4_lPROPANE
  name = G4_lPROPANE
  specific = 4
FEATURE [App::DocumentObjectGroupPython] C_element098  label="C_element : 056"  # scripted group (container) (typed FeaturePython)
  n = 3
  ref = C_element
FEATURE [App::DocumentObjectGroupPython] H_element090  label="H_element : 051"  # scripted group (container) (typed FeaturePython)
  n = 8
  ref = H_element
FEATURE [App::DocumentObjectGroupPython] O_element086  label="O_element : 047"  # scripted group (container) (typed FeaturePython)
  n = 1
  ref = O_element
FEATURE [App::DocumentObjectGroupPython] G4_N_PROPYL_ALCOHOL  label="G4_N-PROPYL_ALCOHOL"  # scripted group (container) (typed FeaturePython)
  Dunit = g/cm3
  Dvalue = 0.8035
  Group = -> [C_element098,H_element090,O_element086]
  conduct = 2
  density = 1
  expand = 3
  formula = G4_N-PROPYL_ALCOHOL
  name = G4_N-PROPYL_ALCOHOL
  specific = 4
FEATURE [App::DocumentObjectGroupPython] C_element099  label="C_element : 057"  # scripted group (container) (typed FeaturePython)
  n = 5
  ref = C_element
FEATURE [App::DocumentObjectGroupPython] H_element091  label="H_element : 052"  # scripted group (container) (typed FeaturePython)
  n = 5
  ref = H_element
FEATURE [App::DocumentObjectGroupPython] N_element038  label="N_element : 017"  # scripted group (container) (typed FeaturePython)
  n = 1
  ref = N_element
FEATURE [App::DocumentObjectGroupPython] G4_PYRIDINE  # scripted group (container) (typed FeaturePython)
  Dunit = g/cm3
  Dvalue = 0.9819
  Group = -> [C_element099,H_element091,N_element038]
  conduct = 2
  density = 1
  expand = 3
  formula = G4_PYRIDINE
  name = G4_PYRIDINE
  specific = 4
FEATURE [App::DocumentObjectGroupPython] H_element092  label="H_element : 0.144"  # scripted group (container) (typed FeaturePython)
  n = 0.143711
FEATURE [App::DocumentObjectGroupPython] C_element100  label="C_element : 0.856"  # scripted group (container) (typed FeaturePython)
  n = 0.856289
FEATURE [App::DocumentObjectGroupPython] G4_RUBBER_BUTYL  # scripted group (container) (typed FeaturePython)
  Dunit = g/cm3
  Dvalue = 0.92
  Group = -> [H_element092,C_element100]
  conduct = 2
  density = 1
  expand = 3
  formula = G4_RUBBER_BUTYL
  name = G4_RUBBER_BUTYL
  specific = 4
FEATURE [App::DocumentObjectGroupPython] H_element093  label="H_element : 0.118"  # scripted group (container) (typed FeaturePython)
  n = 0.118371
FEATURE [App::DocumentObjectGroupPython] C_element101  label="C_element : 0.882"  # scripted group (container) (typed FeaturePython)
  n = 0.881629
FEATURE [App::DocumentObjectGroupPython] G4_RUBBER_NATURAL  # scripted group (container) (typed FeaturePython)
  Dunit = g/cm3
  Dvalue = 0.92
  Group = -> [H_element093,C_element101]
  conduct = 2
  density = 1
  expand = 3
  formula = G4_RUBBER_NATURAL
  name = G4_RUBBER_NATURAL
  specific = 4
FEATURE [App::DocumentObjectGroupPython] H_element094  label="H_element : 0.145"  # scripted group (container) (typed FeaturePython)
  n = 0.05692
FEATURE [App::DocumentObjectGroupPython] C_element102  label="C_element : 0.543"  # scripted group (container) (typed FeaturePython)
  n = 0.542646
FEATURE [App::DocumentObjectGroupPython] Cl_element021  label="Cl_element : 0.400"  # scripted group (container) (typed FeaturePython)
  n = 0.400434
FEATURE [App::DocumentObjectGroupPython] G4_RUBBER_NEOPRENE  # scripted group (container) (typed FeaturePython)
  Dunit = g/cm3
  Dvalue = 1.23
  Group = -> [H_element094,C_element102,Cl_element021]
  conduct = 2
  density = 1
  expand = 3
  formula = G4_RUBBER_NEOPRENE
  name = G4_RUBBER_NEOPRENE
  specific = 4
FEATURE [App::DocumentObjectGroupPython] Si_element006  label="Si_element : 1"  # scripted group (container) (typed FeaturePython)
  n = 1
  ref = Si_element
FEATURE [App::DocumentObjectGroupPython] O_element087  label="O_element : 048"  # scripted group (container) (typed FeaturePython)
  n = 2
  ref = O_element
FEATURE [App::DocumentObjectGroupPython] G4_SILICON_DIOXIDE  # scripted group (container) (typed FeaturePython)
  Dunit = g/cm3
  Dvalue = 2.32
  Group = -> [Si_element006,O_element087]
  conduct = 2
  density = 1
  expand = 3
  formula = G4_SILICON_DIOXIDE
  name = G4_SILICON_DIOXIDE
  specific = 4
FEATURE [App::DocumentObjectGroupPython] Ag_element002  label="Ag_element : 1"  # scripted group (container) (typed FeaturePython)
  n = 1
  ref = Ag_element
FEATURE [App::DocumentObjectGroupPython] Br_element005  label="Br_element : 003"  # scripted group (container) (typed FeaturePython)
  n = 1
  ref = Br_element
FEATURE [App::DocumentObjectGroupPython] G4_SILVER_BROMIDE  # scripted group (container) (typed FeaturePython)
  Dunit = g/cm3
  Dvalue = 6.473
  Group = -> [Ag_element002,Br_element005]
  conduct = 2
  density = 1
  expand = 3
  formula = G4_SILVER_BROMIDE
  name = G4_SILVER_BROMIDE
  specific = 4
FEATURE [App::DocumentObjectGroupPython] Ag_element003  label="Ag_element : 002"  # scripted group (container) (typed FeaturePython)
  n = 1
  ref = Ag_element
FEATURE [App::DocumentObjectGroupPython] Cl_element022  label="Cl_element : 011"  # scripted group (container) (typed FeaturePython)
  n = 1
  ref = Cl_element
FEATURE [App::DocumentObjectGroupPython] G4_SILVER_CHLORIDE  # scripted group (container) (typed FeaturePython)
  Dunit = g/cm3
  Dvalue = 5.56
  Group = -> [Ag_element003,Cl_element022]
  conduct = 2
  density = 1
  expand = 3
  formula = G4_SILVER_CHLORIDE
  name = G4_SILVER_CHLORIDE
  specific = 4
FEATURE [App::DocumentObjectGroupPython] Br_element006  label="Br_element : 0.423"  # scripted group (container) (typed FeaturePython)
  n = 0.422895
FEATURE [App::DocumentObjectGroupPython] Ag_element004  label="Ag_element : 0.574"  # scripted group (container) (typed FeaturePython)
  n = 0.573748
FEATURE [App::DocumentObjectGroupPython] I_element007  label="I_element : 0.649"  # scripted group (container) (typed FeaturePython)
  n = 0.003357
FEATURE [App::DocumentObjectGroupPython] G4_SILVER_HALIDES  # scripted group (container) (typed FeaturePython)
  Dunit = g/cm3
  Dvalue = 6.47
  Group = -> [Br_element006,Ag_element004,I_element007]
  conduct = 2
  density = 1
  expand = 3
  formula = G4_SILVER_HALIDES
  name = G4_SILVER_HALIDES
  specific = 4
FEATURE [App::DocumentObjectGroupPython] Ag_element005  label="Ag_element : 003"  # scripted group (container) (typed FeaturePython)
  n = 1
  ref = Ag_element
FEATURE [App::DocumentObjectGroupPython] I_element008  label="I_element : 004"  # scripted group (container) (typed FeaturePython)
  n = 1
  ref = I_element
FEATURE [App::DocumentObjectGroupPython] G4_SILVER_IODIDE  # scripted group (container) (typed FeaturePython)
  Dunit = g/cm3
  Dvalue = 6.01
  Group = -> [Ag_element005,I_element008]
  conduct = 2
  density = 1
  expand = 3
  formula = G4_SILVER_IODIDE
  name = G4_SILVER_IODIDE
  specific = 4
FEATURE [App::DocumentObjectGroupPython] H_element095  label="H_element : 0.100"  # scripted group (container) (typed FeaturePython)
  n = 0.1
FEATURE [App::DocumentObjectGroupPython] C_element103  label="C_element : 0.204"  # scripted group (container) (typed FeaturePython)
  n = 0.204
FEATURE [App::DocumentObjectGroupPython] N_element039  label="N_element : 0.759"  # scripted group (container) (typed FeaturePython)
  n = 0.042
FEATURE [App::DocumentObjectGroupPython] O_element088  label="O_element : 0.645"  # scripted group (container) (typed FeaturePython)
  n = 0.645
FEATURE [App::DocumentObjectGroupPython] Na_element013  label="Na_element : 0.100"  # scripted group (container) (typed FeaturePython)
  n = 0.002
FEATURE [App::DocumentObjectGroupPython] P_element009  label="P_element : 0.107"  # scripted group (container) (typed FeaturePython)
  n = 0.001
FEATURE [App::DocumentObjectGroupPython] S_element020  label="S_element : 0.021"  # scripted group (container) (typed FeaturePython)
  n = 0.002
FEATURE [App::DocumentObjectGroupPython] Cl_element023  label="Cl_element : 0.590"  # scripted group (container) (typed FeaturePython)
  n = 0.003
FEATURE [App::DocumentObjectGroupPython] K_element010  label="K_element : 0.001"  # scripted group (container) (typed FeaturePython)
  n = 0.001
FEATURE [App::DocumentObjectGroupPython] G4_SKIN_ICRP  # scripted group (container) (typed FeaturePython)
  Dunit = g/cm3
  Dvalue = 1.09
  Group = -> [H_element095,C_element103,N_element039,O_element088,Na_element013,P_element009,S_element020,Cl_element023,K_element010]
  conduct = 2
  density = 1
  expand = 3
  formula = G4_SKIN_ICRP
  name = G4_SKIN_ICRP
  specific = 4
FEATURE [App::DocumentObjectGroupPython] Na_element014  label="Na_element : 2"  # scripted group (container) (typed FeaturePython)
  n = 2
  ref = Na_element
FEATURE [App::DocumentObjectGroupPython] C_element104  label="C_element : 058"  # scripted group (container) (typed FeaturePython)
  n = 1
  ref = C_element
FEATURE [App::DocumentObjectGroupPython] O_element089  label="O_element : 049"  # scripted group (container) (typed FeaturePython)
  n = 3
  ref = O_element
FEATURE [App::DocumentObjectGroupPython] G4_SODIUM_CARBONATE  # scripted group (container) (typed FeaturePython)
  Dunit = g/cm3
  Dvalue = 2.532
  Group = -> [Na_element014,C_element104,O_element089]
  conduct = 2
  density = 1
  expand = 3
  formula = G4_SODIUM_CARBONATE
  name = G4_SODIUM_CARBONATE
  specific = 4
FEATURE [App::DocumentObjectGroupPython] Na_element015  label="Na_element : 1"  # scripted group (container) (typed FeaturePython)
  n = 1
  ref = Na_element
FEATURE [App::DocumentObjectGroupPython] I_element009  label="I_element : 005"  # scripted group (container) (typed FeaturePython)
  n = 1
  ref = I_element
FEATURE [App::DocumentObjectGroupPython] G4_SODIUM_IODIDE  # scripted group (container) (typed FeaturePython)
  Dunit = g/cm3
  Dvalue = 3.667
  Group = -> [Na_element015,I_element009]
  conduct = 2
  density = 1
  expand = 3
  formula = G4_SODIUM_IODIDE
  name = G4_SODIUM_IODIDE
  specific = 4
FEATURE [App::DocumentObjectGroupPython] Na_element016  label="Na_element : 003"  # scripted group (container) (typed FeaturePython)
  n = 2
  ref = Na_element
FEATURE [App::DocumentObjectGroupPython] O_element090  label="O_element : 050"  # scripted group (container) (typed FeaturePython)
  n = 1
  ref = O_element
FEATURE [App::DocumentObjectGroupPython] G4_SODIUM_MONOXIDE  # scripted group (container) (typed FeaturePython)
  Dunit = g/cm3
  Dvalue = 2.27
  Group = -> [Na_element016,O_element090]
  conduct = 2
  density = 1
  expand = 3
  formula = G4_SODIUM_MONOXIDE
  name = G4_SODIUM_MONOXIDE
  specific = 4
FEATURE [App::DocumentObjectGroupPython] Na_element017  label="Na_element : 004"  # scripted group (container) (typed FeaturePython)
  n = 1
  ref = Na_element
FEATURE [App::DocumentObjectGroupPython] N_element040  label="N_element : 018"  # scripted group (container) (typed FeaturePython)
  n = 1
  ref = N_element
FEATURE [App::DocumentObjectGroupPython] O_element091  label="O_element : 051"  # scripted group (container) (typed FeaturePython)
  n = 3
  ref = O_element
FEATURE [App::DocumentObjectGroupPython] G4_SODIUM_NITRATE  # scripted group (container) (typed FeaturePython)
  Dunit = g/cm3
  Dvalue = 2.261
  Group = -> [Na_element017,N_element040,O_element091]
  conduct = 2
  density = 1
  expand = 3
  formula = G4_SODIUM_NITRATE
  name = G4_SODIUM_NITRATE
  specific = 4
FEATURE [App::DocumentObjectGroupPython] C_element105  label="C_element : 059"  # scripted group (container) (typed FeaturePython)
  n = 14
  ref = C_element
FEATURE [App::DocumentObjectGroupPython] H_element096  label="H_element : 053"  # scripted group (container) (typed FeaturePython)
  n = 12
  ref = H_element
FEATURE [App::DocumentObjectGroupPython] G4_STILBENE  # scripted group (container) (typed FeaturePython)
  Dunit = g/cm3
  Dvalue = 0.9707
  Group = -> [C_element105,H_element096]
  conduct = 2
  density = 1
  expand = 3
  formula = G4_STILBENE
  name = G4_STILBENE
  specific = 4
FEATURE [App::DocumentObjectGroupPython] C_element106  label="C_element : 12"  # scripted group (container) (typed FeaturePython)
  n = 12
  ref = C_element
FEATURE [App::DocumentObjectGroupPython] H_element097  label="H_element : 22"  # scripted group (container) (typed FeaturePython)
  n = 22
  ref = H_element
FEATURE [App::DocumentObjectGroupPython] O_element092  label="O_element : 11"  # scripted group (container) (typed FeaturePython)
  n = 11
  ref = O_element
FEATURE [App::DocumentObjectGroupPython] G4_SUCROSE  # scripted group (container) (typed FeaturePython)
  Dunit = g/cm3
  Dvalue = 1.5805
  Group = -> [C_element106,H_element097,O_element092]
  conduct = 2
  density = 1
  expand = 3
  formula = G4_SUCROSE
  name = G4_SUCROSE
  specific = 4
FEATURE [App::DocumentObjectGroupPython] C_element107  label="C_element : 18"  # scripted group (container) (typed FeaturePython)
  n = 18
  ref = C_element
FEATURE [App::DocumentObjectGroupPython] H_element098  label="H_element : 054"  # scripted group (container) (typed FeaturePython)
  n = 14
  ref = H_element
FEATURE [App::DocumentObjectGroupPython] G4_TERPHENYL  # scripted group (container) (typed FeaturePython)
  Dunit = g/cm3
  Dvalue = 1.24
  Group = -> [C_element107,H_element098]
  conduct = 2
  density = 1
  expand = 3
  formula = G4_TERPHENYL
  name = G4_TERPHENYL
  specific = 4
FEATURE [App::DocumentObjectGroupPython] H_element099  label="H_element : 0.146"  # scripted group (container) (typed FeaturePython)
  n = 0.106
FEATURE [App::DocumentObjectGroupPython] C_element108  label="C_element : 0.883"  # scripted group (container) (typed FeaturePython)
  n = 0.099
FEATURE [App::DocumentObjectGroupPython] N_element041  label="N_element : 0.020"  # scripted group (container) (typed FeaturePython)
  n = 0.02
FEATURE [App::DocumentObjectGroupPython] O_element093  label="O_element : 0.766"  # scripted group (container) (typed FeaturePython)
  n = 0.766
FEATURE [App::DocumentObjectGroupPython] Na_element018  label="Na_element : 0.101"  # scripted group (container) (typed FeaturePython)
  n = 0.002
FEATURE [App::DocumentObjectGroupPython] P_element010  label="P_element : 0.108"  # scripted group (container) (typed FeaturePython)
  n = 0.001
FEATURE [App::DocumentObjectGroupPython] S_element021  label="S_element : 0.022"  # scripted group (container) (typed FeaturePython)
  n = 0.002
FEATURE [App::DocumentObjectGroupPython] Cl_element024  label="Cl_element : 0.002"  # scripted group (container) (typed FeaturePython)
  n = 0.002
FEATURE [App::DocumentObjectGroupPython] K_element011  label="K_element : 0.017"  # scripted group (container) (typed FeaturePython)
  n = 0.002
FEATURE [App::DocumentObjectGroupPython] G4_TESTIS_ICRP  # scripted group (container) (typed FeaturePython)
  Dunit = g/cm3
  Dvalue = 1.04
  Group = -> [H_element099,C_element108,N_element041,O_element093,Na_element018,P_element010,S_element021,Cl_element024,K_element011]
  conduct = 2
  density = 1
  expand = 3
  formula = G4_TESTIS_ICRP
  name = G4_TESTIS_ICRP
  specific = 4
FEATURE [App::DocumentObjectGroupPython] C_element109  label="C_element : 060"  # scripted group (container) (typed FeaturePython)
  n = 2
  ref = C_element
FEATURE [App::DocumentObjectGroupPython] Cl_element025  label="Cl_element : 012"  # scripted group (container) (typed FeaturePython)
  n = 4
  ref = Cl_element
FEATURE [App::DocumentObjectGroupPython] G4_TETRACHLOROETHYLENE  # scripted group (container) (typed FeaturePython)
  Dunit = g/cm3
  Dvalue = 1.625
  Group = -> [C_element109,Cl_element025]
  conduct = 2
  density = 1
  expand = 3
  formula = G4_TETRACHLOROETHYLENE
  name = G4_TETRACHLOROETHYLENE
  specific = 4
FEATURE [App::DocumentObjectGroupPython] Tl_element001  label="Tl_element : 1"  # scripted group (container) (typed FeaturePython)
  n = 1
  ref = Tl_element
FEATURE [App::DocumentObjectGroupPython] Cl_element026  label="Cl_element : 013"  # scripted group (container) (typed FeaturePython)
  n = 1
  ref = Cl_element
FEATURE [App::DocumentObjectGroupPython] G4_THALLIUM_CHLORIDE  # scripted group (container) (typed FeaturePython)
  Dunit = g/cm3
  Dvalue = 7.004
  Group = -> [Tl_element001,Cl_element026]
  conduct = 2
  density = 1
  expand = 3
  formula = G4_THALLIUM_CHLORIDE
  name = G4_THALLIUM_CHLORIDE
  specific = 4
FEATURE [App::DocumentObjectGroupPython] H_element100  label="H_element : 0.147"  # scripted group (container) (typed FeaturePython)
  n = 0.105
FEATURE [App::DocumentObjectGroupPython] C_element110  label="C_element : 0.256"  # scripted group (container) (typed FeaturePython)
  n = 0.256
FEATURE [App::DocumentObjectGroupPython] N_element042  label="N_element : 0.760"  # scripted group (container) (typed FeaturePython)
  n = 0.027
FEATURE [App::DocumentObjectGroupPython] O_element094  label="O_element : 0.602"  # scripted group (container) (typed FeaturePython)
  n = 0.602
FEATURE [App::DocumentObjectGroupPython] Na_element019  label="Na_element : 0.102"  # scripted group (container) (typed FeaturePython)
  n = 0.001
FEATURE [App::DocumentObjectGroupPython] P_element011  label="P_element : 0.109"  # scripted group (container) (typed FeaturePython)
  n = 0.002
FEATURE [App::DocumentObjectGroupPython] S_element022  label="S_element : 0.023"  # scripted group (container) (typed FeaturePython)
  n = 0.003
FEATURE [App::DocumentObjectGroupPython] Cl_element027  label="Cl_element : 0.591"  # scripted group (container) (typed FeaturePython)
  n = 0.002
FEATURE [App::DocumentObjectGroupPython] K_element012  label="K_element : 0.018"  # scripted group (container) (typed FeaturePython)
  n = 0.002
FEATURE [App::DocumentObjectGroupPython] G4_TISSUE_SOFT_ICRP  # scripted group (container) (typed FeaturePython)
  Dunit = g/cm3
  Dvalue = 1.03
  Group = -> [H_element100,C_element110,N_element042,O_element094,Na_element019,P_element011,S_element022,Cl_element027,K_element012]
  conduct = 2
  density = 1
  expand = 3
  formula = G4_TISSUE_SOFT_ICRP
  name = G4_TISSUE_SOFT_ICRP
  specific = 4
FEATURE [App::DocumentObjectGroupPython] H_element101  label="H_element : 0.148"  # scripted group (container) (typed FeaturePython)
  n = 0.101
FEATURE [App::DocumentObjectGroupPython] C_element111  label="C_element : 0.111"  # scripted group (container) (typed FeaturePython)
  n = 0.111
FEATURE [App::DocumentObjectGroupPython] N_element043  label="N_element : 0.026"  # scripted group (container) (typed FeaturePython)
  n = 0.026
FEATURE [App::DocumentObjectGroupPython] O_element095  label="O_element : 0.762"  # scripted group (container) (typed FeaturePython)
  n = 0.762
FEATURE [App::DocumentObjectGroupPython] G4_TISSUE_SOFT_ICRU_4  label="G4_TISSUE_SOFT_ICRU-4"  # scripted group (container) (typed FeaturePython)
  Dunit = g/cm3
  Dvalue = 1
  Group = -> [H_element101,C_element111,N_element043,O_element095]
  conduct = 2
  density = 1
  expand = 3
  formula = G4_TISSUE_SOFT_ICRU-4
  name = G4_TISSUE_SOFT_ICRU-4
  specific = 4
FEATURE [App::DocumentObjectGroupPython] H_element102  label="H_element : 0.149"  # scripted group (container) (typed FeaturePython)
  n = 0.101869
FEATURE [App::DocumentObjectGroupPython] C_element112  label="C_element : 0.456"  # scripted group (container) (typed FeaturePython)
  n = 0.456179
FEATURE [App::DocumentObjectGroupPython] N_element044  label="N_element : 0.761"  # scripted group (container) (typed FeaturePython)
  n = 0.035172
FEATURE [App::DocumentObjectGroupPython] O_element096  label="O_element : 0.407"  # scripted group (container) (typed FeaturePython)
  n = 0.40678
FEATURE [App::DocumentObjectGroupPython] G4_TISSUE_METHANE  label="G4_TISSUE-METHANE"  # scripted group (container) (typed FeaturePython)
  Dunit = g/cm3
  Dvalue = 0.00106409
  Group = -> [H_element102,C_element112,N_element044,O_element096]
  conduct = 2
  density = 1
  expand = 3
  formula = G4_TISSUE-METHANE
  name = G4_TISSUE-METHANE
  specific = 4
FEATURE [App::DocumentObjectGroupPython] H_element103  label="H_element : 0.103"  # scripted group (container) (typed FeaturePython)
  n = 0.102672
FEATURE [App::DocumentObjectGroupPython] C_element113  label="C_element : 0.569"  # scripted group (container) (typed FeaturePython)
  n = 0.56894
FEATURE [App::DocumentObjectGroupPython] N_element045  label="N_element : 0.762"  # scripted group (container) (typed FeaturePython)
  n = 0.035022
FEATURE [App::DocumentObjectGroupPython] O_element097  label="O_element : 0.293"  # scripted group (container) (typed FeaturePython)
  n = 0.293366
FEATURE [App::DocumentObjectGroupPython] G4_TISSUE_PROPANE  label="G4_TISSUE-PROPANE"  # scripted group (container) (typed FeaturePython)
  Dunit = g/cm3
  Dvalue = 0.00182628
  Group = -> [H_element103,C_element113,N_element045,O_element097]
  conduct = 2
  density = 1
  expand = 3
  formula = G4_TISSUE-PROPANE
  name = G4_TISSUE-PROPANE
  specific = 4
FEATURE [App::DocumentObjectGroupPython] Ti_element003  label="Ti_element : 1"  # scripted group (container) (typed FeaturePython)
  n = 1
  ref = Ti_element
FEATURE [App::DocumentObjectGroupPython] O_element098  label="O_element : 052"  # scripted group (container) (typed FeaturePython)
  n = 2
  ref = O_element
FEATURE [App::DocumentObjectGroupPython] G4_TITANIUM_DIOXIDE  # scripted group (container) (typed FeaturePython)
  Dunit = g/cm3
  Dvalue = 4.26
  Group = -> [Ti_element003,O_element098]
  conduct = 2
  density = 1
  expand = 3
  formula = G4_TITANIUM_DIOXIDE
  name = G4_TITANIUM_DIOXIDE
  specific = 4
FEATURE [App::DocumentObjectGroupPython] C_element114  label="C_element : 061"  # scripted group (container) (typed FeaturePython)
  n = 7
  ref = C_element
FEATURE [App::DocumentObjectGroupPython] H_element104  label="H_element : 055"  # scripted group (container) (typed FeaturePython)
  n = 8
  ref = H_element
FEATURE [App::DocumentObjectGroupPython] G4_TOLUENE  # scripted group (container) (typed FeaturePython)
  Dunit = g/cm3
  Dvalue = 0.8669
  Group = -> [C_element114,H_element104]
  conduct = 2
  density = 1
  expand = 3
  formula = G4_TOLUENE
  name = G4_TOLUENE
  specific = 4
FEATURE [App::DocumentObjectGroupPython] C_element115  label="C_element : 062"  # scripted group (container) (typed FeaturePython)
  n = 2
  ref = C_element
FEATURE [App::DocumentObjectGroupPython] H_element105  label="H_element : 056"  # scripted group (container) (typed FeaturePython)
  n = 1
  ref = H_element
FEATURE [App::DocumentObjectGroupPython] Cl_element028  label="Cl_element : 014"  # scripted group (container) (typed FeaturePython)
  n = 3
  ref = Cl_element
FEATURE [App::DocumentObjectGroupPython] G4_TRICHLOROETHYLENE  # scripted group (container) (typed FeaturePython)
  Dunit = g/cm3
  Dvalue = 1.46
  Group = -> [C_element115,H_element105,Cl_element028]
  conduct = 2
  density = 1
  expand = 3
  formula = G4_TRICHLOROETHYLENE
  name = G4_TRICHLOROETHYLENE
  specific = 4
FEATURE [App::DocumentObjectGroupPython] C_element116  label="C_element : 063"  # scripted group (container) (typed FeaturePython)
  n = 6
  ref = C_element
FEATURE [App::DocumentObjectGroupPython] H_element106  label="H_element : 15"  # scripted group (container) (typed FeaturePython)
  n = 15
  ref = H_element
FEATURE [App::DocumentObjectGroupPython] O_element099  label="O_element : 053"  # scripted group (container) (typed FeaturePython)
  n = 4
  ref = O_element
FEATURE [App::DocumentObjectGroupPython] P_element012  label="P_element : 1"  # scripted group (container) (typed FeaturePython)
  n = 1
  ref = P_element
FEATURE [App::DocumentObjectGroupPython] G4_TRIETHYL_PHOSPHATE  # scripted group (container) (typed FeaturePython)
  Dunit = g/cm3
  Dvalue = 1.07
  Group = -> [C_element116,H_element106,O_element099,P_element012]
  conduct = 2
  density = 1
  expand = 3
  formula = G4_TRIETHYL_PHOSPHATE
  name = G4_TRIETHYL_PHOSPHATE
  specific = 4
FEATURE [App::DocumentObjectGroupPython] W_element003  label="W_element : 003"  # scripted group (container) (typed FeaturePython)
  n = 1
  ref = W_element
FEATURE [App::DocumentObjectGroupPython] F_element017  label="F_element : 6"  # scripted group (container) (typed FeaturePython)
  n = 6
  ref = F_element
FEATURE [App::DocumentObjectGroupPython] G4_TUNGSTEN_HEXAFLUORIDE  # scripted group (container) (typed FeaturePython)
  Dunit = g/cm3
  Dvalue = 2.4
  Group = -> [W_element003,F_element017]
  conduct = 2
  density = 1
  expand = 3
  formula = G4_TUNGSTEN_HEXAFLUORIDE
  name = G4_TUNGSTEN_HEXAFLUORIDE
  specific = 4
FEATURE [App::DocumentObjectGroupPython] U_element001  label="U_element : 1"  # scripted group (container) (typed FeaturePython)
  n = 1
  ref = U_element
FEATURE [App::DocumentObjectGroupPython] C_element117  label="C_element : 064"  # scripted group (container) (typed FeaturePython)
  n = 2
  ref = C_element
FEATURE [App::DocumentObjectGroupPython] G4_URANIUM_DICARBIDE  # scripted group (container) (typed FeaturePython)
  Dunit = g/cm3
  Dvalue = 11.28
  Group = -> [U_element001,C_element117]
  conduct = 2
  density = 1
  expand = 3
  formula = G4_URANIUM_DICARBIDE
  name = G4_URANIUM_DICARBIDE
  specific = 4
FEATURE [App::DocumentObjectGroupPython] U_element002  label="U_element : 002"  # scripted group (container) (typed FeaturePython)
  n = 1
  ref = U_element
FEATURE [App::DocumentObjectGroupPython] C_element118  label="C_element : 065"  # scripted group (container) (typed FeaturePython)
  n = 1
  ref = C_element
FEATURE [App::DocumentObjectGroupPython] G4_URANIUM_MONOCARBIDE  # scripted group (container) (typed FeaturePython)
  Dunit = g/cm3
  Dvalue = 13.63
  Group = -> [U_element002,C_element118]
  conduct = 2
  density = 1
  expand = 3
  formula = G4_URANIUM_MONOCARBIDE
  name = G4_URANIUM_MONOCARBIDE
  specific = 4
FEATURE [App::DocumentObjectGroupPython] U_element003  label="U_element : 003"  # scripted group (container) (typed FeaturePython)
  n = 1
  ref = U_element
FEATURE [App::DocumentObjectGroupPython] O_element100  label="O_element : 054"  # scripted group (container) (typed FeaturePython)
  n = 2
  ref = O_element
FEATURE [App::DocumentObjectGroupPython] G4_URANIUM_OXIDE  # scripted group (container) (typed FeaturePython)
  Dunit = g/cm3
  Dvalue = 10.96
  Group = -> [U_element003,O_element100]
  conduct = 2
  density = 1
  expand = 3
  formula = G4_URANIUM_OXIDE
  name = G4_URANIUM_OXIDE
  specific = 4
FEATURE [App::DocumentObjectGroupPython] C_element119  label="C_element : 066"  # scripted group (container) (typed FeaturePython)
  n = 1
  ref = C_element
FEATURE [App::DocumentObjectGroupPython] H_element107  label="H_element : 057"  # scripted group (container) (typed FeaturePython)
  n = 4
  ref = H_element
FEATURE [App::DocumentObjectGroupPython] N_element046  label="N_element : 019"  # scripted group (container) (typed FeaturePython)
  n = 2
  ref = N_element
FEATURE [App::DocumentObjectGroupPython] O_element101  label="O_element : 055"  # scripted group (container) (typed FeaturePython)
  n = 1
  ref = O_element
FEATURE [App::DocumentObjectGroupPython] G4_UREA  # scripted group (container) (typed FeaturePython)
  Dunit = g/cm3
  Dvalue = 1.323
  Group = -> [C_element119,H_element107,N_element046,O_element101]
  conduct = 2
  density = 1
  expand = 3
  formula = G4_UREA
  name = G4_UREA
  specific = 4
FEATURE [App::DocumentObjectGroupPython] C_element120  label="C_element : 067"  # scripted group (container) (typed FeaturePython)
  n = 5
  ref = C_element
FEATURE [App::DocumentObjectGroupPython] H_element108  label="H_element : 058"  # scripted group (container) (typed FeaturePython)
  n = 11
  ref = H_element
FEATURE [App::DocumentObjectGroupPython] N_element047  label="N_element : 020"  # scripted group (container) (typed FeaturePython)
  n = 1
  ref = N_element
FEATURE [App::DocumentObjectGroupPython] O_element102  label="O_element : 056"  # scripted group (container) (typed FeaturePython)
  n = 2
  ref = O_element
FEATURE [App::DocumentObjectGroupPython] G4_VALINE  # scripted group (container) (typed FeaturePython)
  Dunit = g/cm3
  Dvalue = 1.23
  Group = -> [C_element120,H_element108,N_element047,O_element102]
  conduct = 2
  density = 1
  expand = 3
  formula = G4_VALINE
  name = G4_VALINE
  specific = 4
FEATURE [App::DocumentObjectGroupPython] H_element109  label="H_element : 0.009"  # scripted group (container) (typed FeaturePython)
  n = 0.009417
FEATURE [App::DocumentObjectGroupPython] C_element121  label="C_element : 0.281"  # scripted group (container) (typed FeaturePython)
  n = 0.280555
FEATURE [App::DocumentObjectGroupPython] F_element018  label="F_element : 0.710"  # scripted group (container) (typed FeaturePython)
  n = 0.710028
FEATURE [App::DocumentObjectGroupPython] G4_VITON  # scripted group (container) (typed FeaturePython)
  Dunit = g/cm3
  Dvalue = 1.8
  Group = -> [H_element109,C_element121,F_element018]
  conduct = 2
  density = 1
  expand = 3
  formula = G4_VITON
  name = G4_VITON
  specific = 4
FEATURE [App::DocumentObjectGroupPython] H_element110  label="H_element : 059"  # scripted group (container) (typed FeaturePython)
  n = 2
  ref = H_element
FEATURE [App::DocumentObjectGroupPython] O_element103  label="O_element : 057"  # scripted group (container) (typed FeaturePython)
  n = 1
  ref = O_element
FEATURE [App::DocumentObjectGroupPython] G4_WATER  # scripted group (container) (typed FeaturePython)
  Dunit = g/cm3
  Dvalue = 1
  Group = -> [H_element110,O_element103]
  conduct = 2
  density = 1
  expand = 3
  formula = G4_WATER
  name = G4_WATER
  specific = 4
FEATURE [App::DocumentObjectGroupPython] H_element111  label="H_element : 060"  # scripted group (container) (typed FeaturePython)
  n = 2
  ref = H_element
FEATURE [App::DocumentObjectGroupPython] O_element104  label="O_element : 058"  # scripted group (container) (typed FeaturePython)
  n = 1
  ref = O_element
FEATURE [App::DocumentObjectGroupPython] G4_WATER_VAPOR  # scripted group (container) (typed FeaturePython)
  Dunit = g/cm3
  Dvalue = 0.000756182
  Group = -> [H_element111,O_element104]
  conduct = 2
  density = 1
  expand = 3
  formula = G4_WATER_VAPOR
  name = G4_WATER_VAPOR
  specific = 4
FEATURE [App::DocumentObjectGroupPython] C_element122  label="C_element : 068"  # scripted group (container) (typed FeaturePython)
  n = 8
  ref = C_element
FEATURE [App::DocumentObjectGroupPython] H_element112  label="H_element : 061"  # scripted group (container) (typed FeaturePython)
  n = 10
  ref = H_element
FEATURE [App::DocumentObjectGroupPython] G4_XYLENE  # scripted group (container) (typed FeaturePython)
  Dunit = g/cm3
  Dvalue = 0.87
  Group = -> [C_element122,H_element112]
  conduct = 2
  density = 1
  expand = 3
  formula = G4_XYLENE
  name = G4_XYLENE
  specific = 4
FEATURE [App::DocumentObjectGroupPython] C_element123  label="C_element : 069"  # scripted group (container) (typed FeaturePython)
  n = 1
  ref = C_element
FEATURE [App::DocumentObjectGroupPython] G4_GRAPHITE  # scripted group (container) (typed FeaturePython)
  Dunit = g/cm3
  Dvalue = 2.21
  Group = -> [C_element123]
  conduct = 2
  density = 1
  expand = 3
  formula = G4_GRAPHITE
  name = G4_GRAPHITE
  specific = 4
FEATURE [App::DocumentObjectGroupPython] NIST  # scripted group (container) (typed FeaturePython)
  Group = -> [G4_A_150_TISSUE,G4_ACETONE,G4_ACETYLENE,G4_ADENINE,G4_ADIPOSE_TISSUE_ICRP,G4_AIR,G4_ALANINE,G4_ALUMINUM_OXIDE,G4_AMBER,G4_AMMONIA,G4_ANILINE,G4_ANTHRACENE,G4_B_100_BONE,G4_BAKELITE,G4_BARIUM_FLUORIDE,G4_BARIUM_SULFATE,G4_BENZENE,G4_BERYLLIUM_OXIDE,G4_BGO,G4_BLOOD_ICRP,G4_BONE_COMPACT_ICRU,G4_BONE_CORTICAL_ICRP,G4_BORON_CARBIDE,G4_BORON_OXIDE,G4_BRAIN_ICRP,G4_BUTANE,G4_N_BUTYL_ALCOHOL,G4_C_552,+152 more]
FEATURE [App::DocumentObjectGroupPython] H_element113  label="H_element : 062"  # scripted group (container) (typed FeaturePython)
  n = 1
  ref = H_element
FEATURE [App::DocumentObjectGroupPython] G4_H  # scripted group (container) (typed FeaturePython)
  Dunit = g/cm3
  Dvalue = 8.3748e-05
  Group = -> [H_element113]
  conduct = 2
  density = 1
  expand = 3
  formula = H
  name = G4_H
  specific = 4
FEATURE [App::DocumentObjectGroupPython] He_element001  label="He_element : 1"  # scripted group (container) (typed FeaturePython)
  n = 1
  ref = He_element
FEATURE [App::DocumentObjectGroupPython] G4_He  # scripted group (container) (typed FeaturePython)
  Dunit = g/cm3
  Dvalue = 0.000166322
  Group = -> [He_element001]
  conduct = 2
  density = 1
  expand = 3
  formula = He
  name = G4_He
  specific = 4
FEATURE [App::DocumentObjectGroupPython] Li_element008  label="Li_element : 008"  # scripted group (container) (typed FeaturePython)
  n = 1
  ref = Li_element
FEATURE [App::DocumentObjectGroupPython] G4_Li  # scripted group (container) (typed FeaturePython)
  Dunit = g/cm3
  Dvalue = 0.534
  Group = -> [Li_element008]
  conduct = 2
  density = 1
  expand = 3
  formula = Li
  name = G4_Li
  specific = 4
FEATURE [App::DocumentObjectGroupPython] Be_element002  label="Be_element : 002"  # scripted group (container) (typed FeaturePython)
  n = 1
  ref = Be_element
FEATURE [App::DocumentObjectGroupPython] G4_Be  # scripted group (container) (typed FeaturePython)
  Dunit = g/cm3
  Dvalue = 1.848
  Group = -> [Be_element002]
  conduct = 2
  density = 1
  expand = 3
  formula = Be
  name = G4_Be
  specific = 4
FEATURE [App::DocumentObjectGroupPython] B_element007  label="B_element : 007"  # scripted group (container) (typed FeaturePython)
  n = 1
  ref = B_element
FEATURE [App::DocumentObjectGroupPython] G4_B  # scripted group (container) (typed FeaturePython)
  Dunit = g/cm3
  Dvalue = 2.37
  Group = -> [B_element007]
  conduct = 2
  density = 1
  expand = 3
  formula = B
  name = G4_B
  specific = 4
FEATURE [App::DocumentObjectGroupPython] C_element124  label="C_element : 070"  # scripted group (container) (typed FeaturePython)
  n = 1
  ref = C_element
FEATURE [App::DocumentObjectGroupPython] G4_C  # scripted group (container) (typed FeaturePython)
  Dunit = g/cm3
  Dvalue = 2
  Group = -> [C_element124]
  conduct = 2
  density = 1
  expand = 3
  formula = C
  name = G4_C
  specific = 4
FEATURE [App::DocumentObjectGroupPython] N_element048  label="N_element : 021"  # scripted group (container) (typed FeaturePython)
  n = 1
  ref = N_element
FEATURE [App::DocumentObjectGroupPython] G4_N  # scripted group (container) (typed FeaturePython)
  Dunit = g/cm3
  Dvalue = 0.0011652
  Group = -> [N_element048]
  conduct = 2
  density = 1
  expand = 3
  formula = N
  name = G4_N
  specific = 4
FEATURE [App::DocumentObjectGroupPython] O_element105  label="O_element : 059"  # scripted group (container) (typed FeaturePython)
  n = 1
  ref = O_element
FEATURE [App::DocumentObjectGroupPython] G4_O  # scripted group (container) (typed FeaturePython)
  Dunit = g/cm3
  Dvalue = 0.00133151
  Group = -> [O_element105]
  conduct = 2
  density = 1
  expand = 3
  formula = O
  name = G4_O
  specific = 4
FEATURE [App::DocumentObjectGroupPython] F_element019  label="F_element : 008"  # scripted group (container) (typed FeaturePython)
  n = 1
  ref = F_element
FEATURE [App::DocumentObjectGroupPython] G4_F  # scripted group (container) (typed FeaturePython)
  Dunit = g/cm3
  Dvalue = 0.00158029
  Group = -> [F_element019]
  conduct = 2
  density = 1
  expand = 3
  formula = F
  name = G4_F
  specific = 4
FEATURE [App::DocumentObjectGroupPython] Ne_element001  label="Ne_element : 1"  # scripted group (container) (typed FeaturePython)
  n = 1
  ref = Ne_element
FEATURE [App::DocumentObjectGroupPython] G4_Ne  # scripted group (container) (typed FeaturePython)
  Dunit = g/cm3
  Dvalue = 0.000838505
  Group = -> [Ne_element001]
  conduct = 2
  density = 1
  expand = 3
  formula = Ne
  name = G4_Ne
  specific = 4
FEATURE [App::DocumentObjectGroupPython] Na_element020  label="Na_element : 005"  # scripted group (container) (typed FeaturePython)
  n = 1
  ref = Na_element
FEATURE [App::DocumentObjectGroupPython] G4_Na  # scripted group (container) (typed FeaturePython)
  Dunit = g/cm3
  Dvalue = 0.971
  Group = -> [Na_element020]
  conduct = 2
  density = 1
  expand = 3
  formula = Na
  name = G4_Na
  specific = 4
FEATURE [App::DocumentObjectGroupPython] Mg_element011  label="Mg_element : 005"  # scripted group (container) (typed FeaturePython)
  n = 1
  ref = Mg_element
FEATURE [App::DocumentObjectGroupPython] G4_Mg  # scripted group (container) (typed FeaturePython)
  Dunit = g/cm3
  Dvalue = 1.74
  Group = -> [Mg_element011]
  conduct = 2
  density = 1
  expand = 3
  formula = Mg
  name = G4_Mg
  specific = 4
FEATURE [App::DocumentObjectGroupPython] Al_element004  label="Al_element : 1"  # scripted group (container) (typed FeaturePython)
  n = 1
  ref = Al_element
FEATURE [App::DocumentObjectGroupPython] G4_Al  # scripted group (container) (typed FeaturePython)
  Dunit = g/cm3
  Dvalue = 2.699
  Group = -> [Al_element004]
  conduct = 2
  density = 1
  expand = 3
  formula = Al
  name = G4_Al
  specific = 4
FEATURE [App::DocumentObjectGroupPython] Si_element007  label="Si_element : 002"  # scripted group (container) (typed FeaturePython)
  n = 1
  ref = Si_element
FEATURE [App::DocumentObjectGroupPython] G4_Si  # scripted group (container) (typed FeaturePython)
  Dunit = g/cm3
  Dvalue = 2.33
  Group = -> [Si_element007]
  conduct = 2
  density = 1
  expand = 3
  formula = Si
  name = G4_Si
  specific = 4
FEATURE [App::DocumentObjectGroupPython] P_element013  label="P_element : 002"  # scripted group (container) (typed FeaturePython)
  n = 1
  ref = P_element
FEATURE [App::DocumentObjectGroupPython] G4_P  # scripted group (container) (typed FeaturePython)
  Dunit = g/cm3
  Dvalue = 2.2
  Group = -> [P_element013]
  conduct = 2
  density = 1
  expand = 3
  formula = P
  name = G4_P
  specific = 4
FEATURE [App::DocumentObjectGroupPython] S_element023  label="S_element : 007"  # scripted group (container) (typed FeaturePython)
  n = 1
  ref = S_element
FEATURE [App::DocumentObjectGroupPython] G4_S  # scripted group (container) (typed FeaturePython)
  Dunit = g/cm3
  Dvalue = 2
  Group = -> [S_element023]
  conduct = 2
  density = 1
  expand = 3
  formula = S
  name = G4_S
  specific = 4
FEATURE [App::DocumentObjectGroupPython] Cl_element029  label="Cl_element : 015"  # scripted group (container) (typed FeaturePython)
  n = 1
  ref = Cl_element
FEATURE [App::DocumentObjectGroupPython] G4_Cl  # scripted group (container) (typed FeaturePython)
  Dunit = g/cm3
  Dvalue = 0.00299473
  Group = -> [Cl_element029]
  conduct = 2
  density = 1
  expand = 3
  formula = Cl
  name = G4_Cl
  specific = 4
FEATURE [App::DocumentObjectGroupPython] Ar_element002  label="Ar_element : 1"  # scripted group (container) (typed FeaturePython)
  n = 1
  ref = Ar_element
FEATURE [App::DocumentObjectGroupPython] G4_Ar  # scripted group (container) (typed FeaturePython)
  Dunit = g/cm3
  Dvalue = 0.00166201
  Group = -> [Ar_element002]
  conduct = 2
  density = 1
  expand = 3
  formula = Ar
  name = G4_Ar
  specific = 4
FEATURE [App::DocumentObjectGroupPython] K_element013  label="K_element : 003"  # scripted group (container) (typed FeaturePython)
  n = 1
  ref = K_element
FEATURE [App::DocumentObjectGroupPython] G4_K  # scripted group (container) (typed FeaturePython)
  Dunit = g/cm3
  Dvalue = 0.862
  Group = -> [K_element013]
  conduct = 2
  density = 1
  expand = 3
  formula = K
  name = G4_K
  specific = 4
FEATURE [App::DocumentObjectGroupPython] Ca_element014  label="Ca_element : 007"  # scripted group (container) (typed FeaturePython)
  n = 1
  ref = Ca_element
FEATURE [App::DocumentObjectGroupPython] G4_Ca  # scripted group (container) (typed FeaturePython)
  Dunit = g/cm3
  Dvalue = 1.55
  Group = -> [Ca_element014]
  conduct = 2
  density = 1
  expand = 3
  formula = Ca
  name = G4_Ca
  specific = 4
FEATURE [App::DocumentObjectGroupPython] Sc_element001  label="Sc_element : 1"  # scripted group (container) (typed FeaturePython)
  n = 1
  ref = Sc_element
FEATURE [App::DocumentObjectGroupPython] G4_Sc  # scripted group (container) (typed FeaturePython)
  Dunit = g/cm3
  Dvalue = 2.989
  Group = -> [Sc_element001]
  conduct = 2
  density = 1
  expand = 3
  formula = Sc
  name = G4_Sc
  specific = 4
FEATURE [App::DocumentObjectGroupPython] Ti_element004  label="Ti_element : 002"  # scripted group (container) (typed FeaturePython)
  n = 1
  ref = Ti_element
FEATURE [App::DocumentObjectGroupPython] G4_Ti  # scripted group (container) (typed FeaturePython)
  Dunit = g/cm3
  Dvalue = 4.54
  Group = -> [Ti_element004]
  conduct = 2
  density = 1
  expand = 3
  formula = Ti
  name = G4_Ti
  specific = 4
FEATURE [App::DocumentObjectGroupPython] V_element001  label="V_element : 1"  # scripted group (container) (typed FeaturePython)
  n = 1
  ref = V_element
FEATURE [App::DocumentObjectGroupPython] G4_V  # scripted group (container) (typed FeaturePython)
  Dunit = g/cm3
  Dvalue = 6.11
  Group = -> [V_element001]
  conduct = 2
  density = 1
  expand = 3
  formula = V
  name = G4_V
  specific = 4
FEATURE [App::DocumentObjectGroupPython] Cr_element001  label="Cr_element : 1"  # scripted group (container) (typed FeaturePython)
  n = 1
  ref = Cr_element
FEATURE [App::DocumentObjectGroupPython] G4_Cr  # scripted group (container) (typed FeaturePython)
  Dunit = g/cm3
  Dvalue = 7.18
  Group = -> [Cr_element001]
  conduct = 2
  density = 1
  expand = 3
  formula = Cr
  name = G4_Cr
  specific = 4
FEATURE [App::DocumentObjectGroupPython] Mn_element001  label="Mn_element : 1"  # scripted group (container) (typed FeaturePython)
  n = 1
  ref = Mn_element
FEATURE [App::DocumentObjectGroupPython] G4_Mn  # scripted group (container) (typed FeaturePython)
  Dunit = g/cm3
  Dvalue = 7.44
  Group = -> [Mn_element001]
  conduct = 2
  density = 1
  expand = 3
  formula = Mn
  name = G4_Mn
  specific = 4
FEATURE [App::DocumentObjectGroupPython] Fe_element007  label="Fe_element : 004"  # scripted group (container) (typed FeaturePython)
  n = 1
  ref = Fe_element
FEATURE [App::DocumentObjectGroupPython] G4_Fe  # scripted group (container) (typed FeaturePython)
  Dunit = g/cm3
  Dvalue = 7.874
  Group = -> [Fe_element007]
  conduct = 2
  density = 1
  expand = 3
  formula = Fe
  name = G4_Fe
  specific = 4
FEATURE [App::DocumentObjectGroupPython] Co_element001  label="Co_element : 1"  # scripted group (container) (typed FeaturePython)
  n = 1
  ref = Co_element
FEATURE [App::DocumentObjectGroupPython] G4_Co  # scripted group (container) (typed FeaturePython)
  Dunit = g/cm3
  Dvalue = 8.9
  Group = -> [Co_element001]
  conduct = 2
  density = 1
  expand = 3
  formula = Co
  name = G4_Co
  specific = 4
FEATURE [App::DocumentObjectGroupPython] Ni_element001  label="Ni_element : 1"  # scripted group (container) (typed FeaturePython)
  n = 1
  ref = Ni_element
FEATURE [App::DocumentObjectGroupPython] G4_Ni  # scripted group (container) (typed FeaturePython)
  Dunit = g/cm3
  Dvalue = 8.902
  Group = -> [Ni_element001]
  conduct = 2
  density = 1
  expand = 3
  formula = Ni
  name = G4_Ni
  specific = 4
FEATURE [App::DocumentObjectGroupPython] Cu_element001  label="Cu_element : 1"  # scripted group (container) (typed FeaturePython)
  n = 1
  ref = Cu_element
FEATURE [App::DocumentObjectGroupPython] G4_Cu  # scripted group (container) (typed FeaturePython)
  Dunit = g/cm3
  Dvalue = 8.96
  Group = -> [Cu_element001]
  conduct = 2
  density = 1
  expand = 3
  formula = Cu
  name = G4_Cu
  specific = 4
FEATURE [App::DocumentObjectGroupPython] Zn_element001  label="Zn_element : 1"  # scripted group (container) (typed FeaturePython)
  n = 1
  ref = Zn_element
FEATURE [App::DocumentObjectGroupPython] G4_Zn  # scripted group (container) (typed FeaturePython)
  Dunit = g/cm3
  Dvalue = 7.133
  Group = -> [Zn_element001]
  conduct = 2
  density = 1
  expand = 3
  formula = Zn
  name = G4_Zn
  specific = 4
FEATURE [App::DocumentObjectGroupPython] Ga_element002  label="Ga_element : 002"  # scripted group (container) (typed FeaturePython)
  n = 1
  ref = Ga_element
FEATURE [App::DocumentObjectGroupPython] G4_Ga  # scripted group (container) (typed FeaturePython)
  Dunit = g/cm3
  Dvalue = 5.904
  Group = -> [Ga_element002]
  conduct = 2
  density = 1
  expand = 3
  formula = Ga
  name = G4_Ga
  specific = 4
FEATURE [App::DocumentObjectGroupPython] Ge_element002  label="Ge_element : 1"  # scripted group (container) (typed FeaturePython)
  n = 1
  ref = Ge_element
FEATURE [App::DocumentObjectGroupPython] G4_Ge  # scripted group (container) (typed FeaturePython)
  Dunit = g/cm3
  Dvalue = 5.323
  Group = -> [Ge_element002]
  conduct = 2
  density = 1
  expand = 3
  formula = Ge
  name = G4_Ge
  specific = 4
FEATURE [App::DocumentObjectGroupPython] As_element003  label="As_element : 002"  # scripted group (container) (typed FeaturePython)
  n = 1
  ref = As_element
FEATURE [App::DocumentObjectGroupPython] G4_As  # scripted group (container) (typed FeaturePython)
  Dunit = g/cm3
  Dvalue = 5.73
  Group = -> [As_element003]
  conduct = 2
  density = 1
  expand = 3
  formula = As
  name = G4_As
  specific = 4
FEATURE [App::DocumentObjectGroupPython] Se_element001  label="Se_element : 1"  # scripted group (container) (typed FeaturePython)
  n = 1
  ref = Se_element
FEATURE [App::DocumentObjectGroupPython] G4_Se  # scripted group (container) (typed FeaturePython)
  Dunit = g/cm3
  Dvalue = 4.5
  Group = -> [Se_element001]
  conduct = 2
  density = 1
  expand = 3
  formula = Se
  name = G4_Se
  specific = 4
FEATURE [App::DocumentObjectGroupPython] Br_element007  label="Br_element : 004"  # scripted group (container) (typed FeaturePython)
  n = 1
  ref = Br_element
FEATURE [App::DocumentObjectGroupPython] G4_Br  # scripted group (container) (typed FeaturePython)
  Dunit = g/cm3
  Dvalue = 0.0070721
  Group = -> [Br_element007]
  conduct = 2
  density = 1
  expand = 3
  formula = Br
  name = G4_Br
  specific = 4
FEATURE [App::DocumentObjectGroupPython] Kr_element001  label="Kr_element : 1"  # scripted group (container) (typed FeaturePython)
  n = 1
  ref = Kr_element
FEATURE [App::DocumentObjectGroupPython] G4_Kr  # scripted group (container) (typed FeaturePython)
  Dunit = g/cm3
  Dvalue = 0.00347832
  Group = -> [Kr_element001]
  conduct = 2
  density = 1
  expand = 3
  formula = Kr
  name = G4_Kr
  specific = 4
FEATURE [App::DocumentObjectGroupPython] Rb_element001  label="Rb_element : 1"  # scripted group (container) (typed FeaturePython)
  n = 1
  ref = Rb_element
FEATURE [App::DocumentObjectGroupPython] G4_Rb  # scripted group (container) (typed FeaturePython)
  Dunit = g/cm3
  Dvalue = 1.532
  Group = -> [Rb_element001]
  conduct = 2
  density = 1
  expand = 3
  formula = Rb
  name = G4_Rb
  specific = 4
FEATURE [App::DocumentObjectGroupPython] Sr_element001  label="Sr_element : 1"  # scripted group (container) (typed FeaturePython)
  n = 1
  ref = Sr_element
FEATURE [App::DocumentObjectGroupPython] G4_Sr  # scripted group (container) (typed FeaturePython)
  Dunit = g/cm3
  Dvalue = 2.54
  Group = -> [Sr_element001]
  conduct = 2
  density = 1
  expand = 3
  formula = Sr
  name = G4_Sr
  specific = 4
FEATURE [App::DocumentObjectGroupPython] Y_element001  label="Y_element : 1"  # scripted group (container) (typed FeaturePython)
  n = 1
  ref = Y_element
FEATURE [App::DocumentObjectGroupPython] G4_Y  # scripted group (container) (typed FeaturePython)
  Dunit = g/cm3
  Dvalue = 4.469
  Group = -> [Y_element001]
  conduct = 2
  density = 1
  expand = 3
  formula = Y
  name = G4_Y
  specific = 4
FEATURE [App::DocumentObjectGroupPython] Zr_element001  label="Zr_element : 1"  # scripted group (container) (typed FeaturePython)
  n = 1
  ref = Zr_element
FEATURE [App::DocumentObjectGroupPython] G4_Zr  # scripted group (container) (typed FeaturePython)
  Dunit = g/cm3
  Dvalue = 6.506
  Group = -> [Zr_element001]
  conduct = 2
  density = 1
  expand = 3
  formula = Zr
  name = G4_Zr
  specific = 4
FEATURE [App::DocumentObjectGroupPython] Nb_element001  label="Nb_element : 1"  # scripted group (container) (typed FeaturePython)
  n = 1
  ref = Nb_element
FEATURE [App::DocumentObjectGroupPython] G4_Nb  # scripted group (container) (typed FeaturePython)
  Dunit = g/cm3
  Dvalue = 8.57
  Group = -> [Nb_element001]
  conduct = 2
  density = 1
  expand = 3
  formula = Nb
  name = G4_Nb
  specific = 4
FEATURE [App::DocumentObjectGroupPython] Mo_element001  label="Mo_element : 1"  # scripted group (container) (typed FeaturePython)
  n = 1
  ref = Mo_element
FEATURE [App::DocumentObjectGroupPython] G4_Mo  # scripted group (container) (typed FeaturePython)
  Dunit = g/cm3
  Dvalue = 10.22
  Group = -> [Mo_element001]
  conduct = 2
  density = 1
  expand = 3
  formula = Mo
  name = G4_Mo
  specific = 4
FEATURE [App::DocumentObjectGroupPython] Tc_element001  label="Tc_element : 1"  # scripted group (container) (typed FeaturePython)
  n = 1
  ref = Tc_element
FEATURE [App::DocumentObjectGroupPython] G4_Tc  # scripted group (container) (typed FeaturePython)
  Dunit = g/cm3
  Dvalue = 11.5
  Group = -> [Tc_element001]
  conduct = 2
  density = 1
  expand = 3
  formula = Tc
  name = G4_Tc
  specific = 4
FEATURE [App::DocumentObjectGroupPython] Ru_element001  label="Ru_element : 1"  # scripted group (container) (typed FeaturePython)
  n = 1
  ref = Ru_element
FEATURE [App::DocumentObjectGroupPython] G4_Ru  # scripted group (container) (typed FeaturePython)
  Dunit = g/cm3
  Dvalue = 12.41
  Group = -> [Ru_element001]
  conduct = 2
  density = 1
  expand = 3
  formula = Ru
  name = G4_Ru
  specific = 4
FEATURE [App::DocumentObjectGroupPython] Rh_element001  label="Rh_element : 1"  # scripted group (container) (typed FeaturePython)
  n = 1
  ref = Rh_element
FEATURE [App::DocumentObjectGroupPython] G4_Rh  # scripted group (container) (typed FeaturePython)
  Dunit = g/cm3
  Dvalue = 12.41
  Group = -> [Rh_element001]
  conduct = 2
  density = 1
  expand = 3
  formula = Rh
  name = G4_Rh
  specific = 4
FEATURE [App::DocumentObjectGroupPython] Pd_element001  label="Pd_element : 1"  # scripted group (container) (typed FeaturePython)
  n = 1
  ref = Pd_element
FEATURE [App::DocumentObjectGroupPython] G4_Pd  # scripted group (container) (typed FeaturePython)
  Dunit = g/cm3
  Dvalue = 12.02
  Group = -> [Pd_element001]
  conduct = 2
  density = 1
  expand = 3
  formula = Pd
  name = G4_Pd
  specific = 4
FEATURE [App::DocumentObjectGroupPython] Ag_element006  label="Ag_element : 004"  # scripted group (container) (typed FeaturePython)
  n = 1
  ref = Ag_element
FEATURE [App::DocumentObjectGroupPython] G4_Ag  # scripted group (container) (typed FeaturePython)
  Dunit = g/cm3
  Dvalue = 10.5
  Group = -> [Ag_element006]
  conduct = 2
  density = 1
  expand = 3
  formula = Ag
  name = G4_Ag
  specific = 4
FEATURE [App::DocumentObjectGroupPython] Cd_element003  label="Cd_element : 003"  # scripted group (container) (typed FeaturePython)
  n = 1
  ref = Cd_element
FEATURE [App::DocumentObjectGroupPython] G4_Cd  # scripted group (container) (typed FeaturePython)
  Dunit = g/cm3
  Dvalue = 8.65
  Group = -> [Cd_element003]
  conduct = 2
  density = 1
  expand = 3
  formula = Cd
  name = G4_Cd
  specific = 4
FEATURE [App::DocumentObjectGroupPython] In_element001  label="In_element : 1"  # scripted group (container) (typed FeaturePython)
  n = 1
  ref = In_element
FEATURE [App::DocumentObjectGroupPython] G4_In  # scripted group (container) (typed FeaturePython)
  Dunit = g/cm3
  Dvalue = 7.31
  Group = -> [In_element001]
  conduct = 2
  density = 1
  expand = 3
  formula = In
  name = G4_In
  specific = 4
FEATURE [App::DocumentObjectGroupPython] Sn_element001  label="Sn_element : 1"  # scripted group (container) (typed FeaturePython)
  n = 1
  ref = Sn_element
FEATURE [App::DocumentObjectGroupPython] G4_Sn  # scripted group (container) (typed FeaturePython)
  Dunit = g/cm3
  Dvalue = 7.31
  Group = -> [Sn_element001]
  conduct = 2
  density = 1
  expand = 3
  formula = Sn
  name = G4_Sn
  specific = 4
FEATURE [App::DocumentObjectGroupPython] Sb_element001  label="Sb_element : 1"  # scripted group (container) (typed FeaturePython)
  n = 1
  ref = Sb_element
FEATURE [App::DocumentObjectGroupPython] G4_Sb  # scripted group (container) (typed FeaturePython)
  Dunit = g/cm3
  Dvalue = 6.691
  Group = -> [Sb_element001]
  conduct = 2
  density = 1
  expand = 3
  formula = Sb
  name = G4_Sb
  specific = 4
FEATURE [App::DocumentObjectGroupPython] Te_element002  label="Te_element : 002"  # scripted group (container) (typed FeaturePython)
  n = 1
  ref = Te_element
FEATURE [App::DocumentObjectGroupPython] G4_Te  # scripted group (container) (typed FeaturePython)
  Dunit = g/cm3
  Dvalue = 6.24
  Group = -> [Te_element002]
  conduct = 2
  density = 1
  expand = 3
  formula = Te
  name = G4_Te
  specific = 4
FEATURE [App::DocumentObjectGroupPython] I_element010  label="I_element : 006"  # scripted group (container) (typed FeaturePython)
  n = 1
  ref = I_element
FEATURE [App::DocumentObjectGroupPython] G4_I  # scripted group (container) (typed FeaturePython)
  Dunit = g/cm3
  Dvalue = 4.93
  Group = -> [I_element010]
  conduct = 2
  density = 1
  expand = 3
  formula = I
  name = G4_I
  specific = 4
FEATURE [App::DocumentObjectGroupPython] Xe_element001  label="Xe_element : 1"  # scripted group (container) (typed FeaturePython)
  n = 1
  ref = Xe_element
FEATURE [App::DocumentObjectGroupPython] G4_Xe  # scripted group (container) (typed FeaturePython)
  Dunit = g/cm3
  Dvalue = 0.00548536
  Group = -> [Xe_element001]
  conduct = 2
  density = 1
  expand = 3
  formula = Xe
  name = G4_Xe
  specific = 4
FEATURE [App::DocumentObjectGroupPython] Cs_element003  label="Cs_element : 003"  # scripted group (container) (typed FeaturePython)
  n = 1
  ref = Cs_element
FEATURE [App::DocumentObjectGroupPython] G4_Cs  # scripted group (container) (typed FeaturePython)
  Dunit = g/cm3
  Dvalue = 1.873
  Group = -> [Cs_element003]
  conduct = 2
  density = 1
  expand = 3
  formula = Cs
  name = G4_Cs
  specific = 4
FEATURE [App::DocumentObjectGroupPython] Ba_element003  label="Ba_element : 003"  # scripted group (container) (typed FeaturePython)
  n = 1
  ref = Ba_element
FEATURE [App::DocumentObjectGroupPython] G4_Ba  # scripted group (container) (typed FeaturePython)
  Dunit = g/cm3
  Dvalue = 3.5
  Group = -> [Ba_element003]
  conduct = 2
  density = 1
  expand = 3
  formula = Ba
  name = G4_Ba
  specific = 4
FEATURE [App::DocumentObjectGroupPython] La_element003  label="La_element : 003"  # scripted group (container) (typed FeaturePython)
  n = 1
  ref = La_element
FEATURE [App::DocumentObjectGroupPython] G4_La  # scripted group (container) (typed FeaturePython)
  Dunit = g/cm3
  Dvalue = 6.154
  Group = -> [La_element003]
  conduct = 2
  density = 1
  expand = 3
  formula = La
  name = G4_La
  specific = 4
FEATURE [App::DocumentObjectGroupPython] Ce_element002  label="Ce_element : 1"  # scripted group (container) (typed FeaturePython)
  n = 1
  ref = Ce_element
FEATURE [App::DocumentObjectGroupPython] G4_Ce  # scripted group (container) (typed FeaturePython)
  Dunit = g/cm3
  Dvalue = 6.657
  Group = -> [Ce_element002]
  conduct = 2
  density = 1
  expand = 3
  formula = Ce
  name = G4_Ce
  specific = 4
FEATURE [App::DocumentObjectGroupPython] Pr_element001  label="Pr_element : 1"  # scripted group (container) (typed FeaturePython)
  n = 1
  ref = Pr_element
FEATURE [App::DocumentObjectGroupPython] G4_Pr  # scripted group (container) (typed FeaturePython)
  Dunit = g/cm3
  Dvalue = 6.71
  Group = -> [Pr_element001]
  conduct = 2
  density = 1
  expand = 3
  formula = Pr
  name = G4_Pr
  specific = 4
FEATURE [App::DocumentObjectGroupPython] Nd_element001  label="Nd_element : 1"  # scripted group (container) (typed FeaturePython)
  n = 1
  ref = Nd_element
FEATURE [App::DocumentObjectGroupPython] G4_Nd  # scripted group (container) (typed FeaturePython)
  Dunit = g/cm3
  Dvalue = 6.9
  Group = -> [Nd_element001]
  conduct = 2
  density = 1
  expand = 3
  formula = Nd
  name = G4_Nd
  specific = 4
FEATURE [App::DocumentObjectGroupPython] Pm_element001  label="Pm_element : 1"  # scripted group (container) (typed FeaturePython)
  n = 1
  ref = Pm_element
FEATURE [App::DocumentObjectGroupPython] G4_Pm  # scripted group (container) (typed FeaturePython)
  Dunit = g/cm3
  Dvalue = 7.22
  Group = -> [Pm_element001]
  conduct = 2
  density = 1
  expand = 3
  formula = Pm
  name = G4_Pm
  specific = 4
FEATURE [App::DocumentObjectGroupPython] Sm_element001  label="Sm_element : 1"  # scripted group (container) (typed FeaturePython)
  n = 1
  ref = Sm_element
FEATURE [App::DocumentObjectGroupPython] G4_Sm  # scripted group (container) (typed FeaturePython)
  Dunit = g/cm3
  Dvalue = 7.46
  Group = -> [Sm_element001]
  conduct = 2
  density = 1
  expand = 3
  formula = Sm
  name = G4_Sm
  specific = 4
FEATURE [App::DocumentObjectGroupPython] Eu_element001  label="Eu_element : 1"  # scripted group (container) (typed FeaturePython)
  n = 1
  ref = Eu_element
FEATURE [App::DocumentObjectGroupPython] G4_Eu  # scripted group (container) (typed FeaturePython)
  Dunit = g/cm3
  Dvalue = 5.243
  Group = -> [Eu_element001]
  conduct = 2
  density = 1
  expand = 3
  formula = Eu
  name = G4_Eu
  specific = 4
FEATURE [App::DocumentObjectGroupPython] Gd_element002  label="Gd_element : 1"  # scripted group (container) (typed FeaturePython)
  n = 1
  ref = Gd_element
FEATURE [App::DocumentObjectGroupPython] G4_Gd  # scripted group (container) (typed FeaturePython)
  Dunit = g/cm3
  Dvalue = 7.9004
  Group = -> [Gd_element002]
  conduct = 2
  density = 1
  expand = 3
  formula = Gd
  name = G4_Gd
  specific = 4
FEATURE [App::DocumentObjectGroupPython] Tb_element001  label="Tb_element : 1"  # scripted group (container) (typed FeaturePython)
  n = 1
  ref = Tb_element
FEATURE [App::DocumentObjectGroupPython] G4_Tb  # scripted group (container) (typed FeaturePython)
  Dunit = g/cm3
  Dvalue = 8.229
  Group = -> [Tb_element001]
  conduct = 2
  density = 1
  expand = 3
  formula = Tb
  name = G4_Tb
  specific = 4
FEATURE [App::DocumentObjectGroupPython] Dy_element001  label="Dy_element : 1"  # scripted group (container) (typed FeaturePython)
  n = 1
  ref = Dy_element
FEATURE [App::DocumentObjectGroupPython] G4_Dy  # scripted group (container) (typed FeaturePython)
  Dunit = g/cm3
  Dvalue = 8.55
  Group = -> [Dy_element001]
  conduct = 2
  density = 1
  expand = 3
  formula = Dy
  name = G4_Dy
  specific = 4
FEATURE [App::DocumentObjectGroupPython] Ho_element001  label="Ho_element : 1"  # scripted group (container) (typed FeaturePython)
  n = 1
  ref = Ho_element
FEATURE [App::DocumentObjectGroupPython] G4_Ho  # scripted group (container) (typed FeaturePython)
  Dunit = g/cm3
  Dvalue = 8.795
  Group = -> [Ho_element001]
  conduct = 2
  density = 1
  expand = 3
  formula = Ho
  name = G4_Ho
  specific = 4
FEATURE [App::DocumentObjectGroupPython] Er_element001  label="Er_element : 1"  # scripted group (container) (typed FeaturePython)
  n = 1
  ref = Er_element
FEATURE [App::DocumentObjectGroupPython] G4_Er  # scripted group (container) (typed FeaturePython)
  Dunit = g/cm3
  Dvalue = 9.066
  Group = -> [Er_element001]
  conduct = 2
  density = 1
  expand = 3
  formula = Er
  name = G4_Er
  specific = 4
FEATURE [App::DocumentObjectGroupPython] Tm_element001  label="Tm_element : 1"  # scripted group (container) (typed FeaturePython)
  n = 1
  ref = Tm_element
FEATURE [App::DocumentObjectGroupPython] G4_Tm  # scripted group (container) (typed FeaturePython)
  Dunit = g/cm3
  Dvalue = 9.321
  Group = -> [Tm_element001]
  conduct = 2
  density = 1
  expand = 3
  formula = Tm
  name = G4_Tm
  specific = 4
FEATURE [App::DocumentObjectGroupPython] Yb_element001  label="Yb_element : 1"  # scripted group (container) (typed FeaturePython)
  n = 1
  ref = Yb_element
FEATURE [App::DocumentObjectGroupPython] G4_Yb  # scripted group (container) (typed FeaturePython)
  Dunit = g/cm3
  Dvalue = 6.73
  Group = -> [Yb_element001]
  conduct = 2
  density = 1
  expand = 3
  formula = Yb
  name = G4_Yb
  specific = 4
FEATURE [App::DocumentObjectGroupPython] Lu_element001  label="Lu_element : 1"  # scripted group (container) (typed FeaturePython)
  n = 1
  ref = Lu_element
FEATURE [App::DocumentObjectGroupPython] G4_Lu  # scripted group (container) (typed FeaturePython)
  Dunit = g/cm3
  Dvalue = 9.84
  Group = -> [Lu_element001]
  conduct = 2
  density = 1
  expand = 3
  formula = Lu
  name = G4_Lu
  specific = 4
FEATURE [App::DocumentObjectGroupPython] Hf_element001  label="Hf_element : 1"  # scripted group (container) (typed FeaturePython)
  n = 1
  ref = Hf_element
FEATURE [App::DocumentObjectGroupPython] G4_Hf  # scripted group (container) (typed FeaturePython)
  Dunit = g/cm3
  Dvalue = 13.31
  Group = -> [Hf_element001]
  conduct = 2
  density = 1
  expand = 3
  formula = Hf
  name = G4_Hf
  specific = 4
FEATURE [App::DocumentObjectGroupPython] Ta_element001  label="Ta_element : 1"  # scripted group (container) (typed FeaturePython)
  n = 1
  ref = Ta_element
FEATURE [App::DocumentObjectGroupPython] G4_Ta  # scripted group (container) (typed FeaturePython)
  Dunit = g/cm3
  Dvalue = 16.654
  Group = -> [Ta_element001]
  conduct = 2
  density = 1
  expand = 3
  formula = Ta
  name = G4_Ta
  specific = 4
FEATURE [App::DocumentObjectGroupPython] W_element004  label="W_element : 004"  # scripted group (container) (typed FeaturePython)
  n = 1
  ref = W_element
FEATURE [App::DocumentObjectGroupPython] G4_W  # scripted group (container) (typed FeaturePython)
  Dunit = g/cm3
  Dvalue = 19.3
  Group = -> [W_element004]
  conduct = 2
  density = 1
  expand = 3
  formula = W
  name = G4_W
  specific = 4
FEATURE [App::DocumentObjectGroupPython] Re_element001  label="Re_element : 1"  # scripted group (container) (typed FeaturePython)
  n = 1
  ref = Re_element
FEATURE [App::DocumentObjectGroupPython] G4_Re  # scripted group (container) (typed FeaturePython)
  Dunit = g/cm3
  Dvalue = 21.02
  Group = -> [Re_element001]
  conduct = 2
  density = 1
  expand = 3
  formula = Re
  name = G4_Re
  specific = 4
FEATURE [App::DocumentObjectGroupPython] Os_element001  label="Os_element : 1"  # scripted group (container) (typed FeaturePython)
  n = 1
  ref = Os_element
FEATURE [App::DocumentObjectGroupPython] G4_Os  # scripted group (container) (typed FeaturePython)
  Dunit = g/cm3
  Dvalue = 22.57
  Group = -> [Os_element001]
  conduct = 2
  density = 1
  expand = 3
  formula = Os
  name = G4_Os
  specific = 4
FEATURE [App::DocumentObjectGroupPython] Ir_element001  label="Ir_element : 1"  # scripted group (container) (typed FeaturePython)
  n = 1
  ref = Ir_element
FEATURE [App::DocumentObjectGroupPython] G4_Ir  # scripted group (container) (typed FeaturePython)
  Dunit = g/cm3
  Dvalue = 22.42
  Group = -> [Ir_element001]
  conduct = 2
  density = 1
  expand = 3
  formula = Ir
  name = G4_Ir
  specific = 4
FEATURE [App::DocumentObjectGroupPython] Pt_element001  label="Pt_element : 1"  # scripted group (container) (typed FeaturePython)
  n = 1
  ref = Pt_element
FEATURE [App::DocumentObjectGroupPython] G4_Pt  # scripted group (container) (typed FeaturePython)
  Dunit = g/cm3
  Dvalue = 21.45
  Group = -> [Pt_element001]
  conduct = 2
  density = 1
  expand = 3
  formula = Pt
  name = G4_Pt
  specific = 4
FEATURE [App::DocumentObjectGroupPython] Au_element001  label="Au_element : 1"  # scripted group (container) (typed FeaturePython)
  n = 1
  ref = Au_element
FEATURE [App::DocumentObjectGroupPython] G4_Au  # scripted group (container) (typed FeaturePython)
  Dunit = g/cm3
  Dvalue = 19.32
  Group = -> [Au_element001]
  conduct = 2
  density = 1
  expand = 3
  formula = Au
  name = G4_Au
  specific = 4
FEATURE [App::DocumentObjectGroupPython] Hg_element002  label="Hg_element : 002"  # scripted group (container) (typed FeaturePython)
  n = 1
  ref = Hg_element
FEATURE [App::DocumentObjectGroupPython] G4_Hg  # scripted group (container) (typed FeaturePython)
  Dunit = g/cm3
  Dvalue = 13.546
  Group = -> [Hg_element002]
  conduct = 2
  density = 1
  expand = 3
  formula = Hg
  name = G4_Hg
  specific = 4
FEATURE [App::DocumentObjectGroupPython] Tl_element002  label="Tl_element : 002"  # scripted group (container) (typed FeaturePython)
  n = 1
  ref = Tl_element
FEATURE [App::DocumentObjectGroupPython] G4_Tl  # scripted group (container) (typed FeaturePython)
  Dunit = g/cm3
  Dvalue = 11.72
  Group = -> [Tl_element002]
  conduct = 2
  density = 1
  expand = 3
  formula = Tl
  name = G4_Tl
  specific = 4
FEATURE [App::DocumentObjectGroupPython] Pb_element003  label="Pb_element : 1"  # scripted group (container) (typed FeaturePython)
  n = 1
  ref = Pb_element
FEATURE [App::DocumentObjectGroupPython] G4_Pb  # scripted group (container) (typed FeaturePython)
  Dunit = g/cm3
  Dvalue = 11.35
  Group = -> [Pb_element003]
  conduct = 2
  density = 1
  expand = 3
  formula = Pb
  name = G4_Pb
  specific = 4
FEATURE [App::DocumentObjectGroupPython] Bi_element002  label="Bi_element : 1"  # scripted group (container) (typed FeaturePython)
  n = 1
  ref = Bi_element
FEATURE [App::DocumentObjectGroupPython] G4_Bi  # scripted group (container) (typed FeaturePython)
  Dunit = g/cm3
  Dvalue = 9.747
  Group = -> [Bi_element002]
  conduct = 2
  density = 1
  expand = 3
  formula = Bi
  name = G4_Bi
  specific = 4
FEATURE [App::DocumentObjectGroupPython] Po_element001  label="Po_element : 1"  # scripted group (container) (typed FeaturePython)
  n = 1
  ref = Po_element
FEATURE [App::DocumentObjectGroupPython] G4_Po  # scripted group (container) (typed FeaturePython)
  Dunit = g/cm3
  Dvalue = 9.32
  Group = -> [Po_element001]
  conduct = 2
  density = 1
  expand = 3
  formula = Po
  name = G4_Po
  specific = 4
FEATURE [App::DocumentObjectGroupPython] At_element001  label="At_element : 1"  # scripted group (container) (typed FeaturePython)
  n = 1
  ref = At_element
FEATURE [App::DocumentObjectGroupPython] G4_At  # scripted group (container) (typed FeaturePython)
  Dunit = g/cm3
  Dvalue = 9.32
  Group = -> [At_element001]
  conduct = 2
  density = 1
  expand = 3
  formula = At
  name = G4_At
  specific = 4
FEATURE [App::DocumentObjectGroupPython] Rn_element001  label="Rn_element : 1"  # scripted group (container) (typed FeaturePython)
  n = 1
  ref = Rn_element
FEATURE [App::DocumentObjectGroupPython] G4_Rn  # scripted group (container) (typed FeaturePython)
  Dunit = g/cm3
  Dvalue = 0.00900662
  Group = -> [Rn_element001]
  conduct = 2
  density = 1
  expand = 3
  formula = Rn
  name = G4_Rn
  specific = 4
FEATURE [App::DocumentObjectGroupPython] Fr_element001  label="Fr_element : 1"  # scripted group (container) (typed FeaturePython)
  n = 1
  ref = Fr_element
FEATURE [App::DocumentObjectGroupPython] G4_Fr  # scripted group (container) (typed FeaturePython)
  Dunit = g/cm3
  Dvalue = 1
  Group = -> [Fr_element001]
  conduct = 2
  density = 1
  expand = 3
  formula = Fr
  name = G4_Fr
  specific = 4
FEATURE [App::DocumentObjectGroupPython] Ra_element001  label="Ra_element : 1"  # scripted group (container) (typed FeaturePython)
  n = 1
  ref = Ra_element
FEATURE [App::DocumentObjectGroupPython] G4_Ra  # scripted group (container) (typed FeaturePython)
  Dunit = g/cm3
  Dvalue = 5
  Group = -> [Ra_element001]
  conduct = 2
  density = 1
  expand = 3
  formula = Ra
  name = G4_Ra
  specific = 4
FEATURE [App::DocumentObjectGroupPython] Ac_element001  label="Ac_element : 1"  # scripted group (container) (typed FeaturePython)
  n = 1
  ref = Ac_element
FEATURE [App::DocumentObjectGroupPython] G4_Ac  # scripted group (container) (typed FeaturePython)
  Dunit = g/cm3
  Dvalue = 10.07
  Group = -> [Ac_element001]
  conduct = 2
  density = 1
  expand = 3
  formula = Ac
  name = G4_Ac
  specific = 4
FEATURE [App::DocumentObjectGroupPython] Th_element001  label="Th_element : 1"  # scripted group (container) (typed FeaturePython)
  n = 1
  ref = Th_element
FEATURE [App::DocumentObjectGroupPython] G4_Th  # scripted group (container) (typed FeaturePython)
  Dunit = g/cm3
  Dvalue = 11.72
  Group = -> [Th_element001]
  conduct = 2
  density = 1
  expand = 3
  formula = Th
  name = G4_Th
  specific = 4
FEATURE [App::DocumentObjectGroupPython] Pa_element001  label="Pa_element : 1"  # scripted group (container) (typed FeaturePython)
  n = 1
  ref = Pa_element
FEATURE [App::DocumentObjectGroupPython] G4_Pa  # scripted group (container) (typed FeaturePython)
  Dunit = g/cm3
  Dvalue = 15.37
  Group = -> [Pa_element001]
  conduct = 2
  density = 1
  expand = 3
  formula = Pa
  name = G4_Pa
  specific = 4
FEATURE [App::DocumentObjectGroupPython] U_element004  label="U_element : 004"  # scripted group (container) (typed FeaturePython)
  n = 1
  ref = U_element
FEATURE [App::DocumentObjectGroupPython] G4_U  # scripted group (container) (typed FeaturePython)
  Dunit = g/cm3
  Dvalue = 18.95
  Group = -> [U_element004]
  conduct = 2
  density = 1
  expand = 3
  formula = U
  name = G4_U
  specific = 4
FEATURE [App::DocumentObjectGroupPython] Np_element001  label="Np_element : 1"  # scripted group (container) (typed FeaturePython)
  n = 1
  ref = Np_element
FEATURE [App::DocumentObjectGroupPython] G4_Np  # scripted group (container) (typed FeaturePython)
  Dunit = g/cm3
  Dvalue = 20.25
  Group = -> [Np_element001]
  conduct = 2
  density = 1
  expand = 3
  formula = Np
  name = G4_Np
  specific = 4
FEATURE [App::DocumentObjectGroupPython] Pu_element002  label="Pu_element : 002"  # scripted group (container) (typed FeaturePython)
  n = 1
  ref = Pu_element
FEATURE [App::DocumentObjectGroupPython] G4_Pu  # scripted group (container) (typed FeaturePython)
  Dunit = g/cm3
  Dvalue = 19.84
  Group = -> [Pu_element002]
  conduct = 2
  density = 1
  expand = 3
  formula = Pu
  name = G4_Pu
  specific = 4
FEATURE [App::DocumentObjectGroupPython] Am_element001  label="Am_element : 1"  # scripted group (container) (typed FeaturePython)
  n = 1
  ref = Am_element
FEATURE [App::DocumentObjectGroupPython] G4_Am  # scripted group (container) (typed FeaturePython)
  Dunit = g/cm3
  Dvalue = 13.67
  Group = -> [Am_element001]
  conduct = 2
  density = 1
  expand = 3
  formula = Am
  name = G4_Am
  specific = 4
FEATURE [App::DocumentObjectGroupPython] Cm_element001  label="Cm_element : 1"  # scripted group (container) (typed FeaturePython)
  n = 1
  ref = Cm_element
FEATURE [App::DocumentObjectGroupPython] G4_Cm  # scripted group (container) (typed FeaturePython)
  Dunit = g/cm3
  Dvalue = 13.51
  Group = -> [Cm_element001]
  conduct = 2
  density = 1
  expand = 3
  formula = Cm
  name = G4_Cm
  specific = 4
FEATURE [App::DocumentObjectGroupPython] Bk_element001  label="Bk_element : 1"  # scripted group (container) (typed FeaturePython)
  n = 1
  ref = Bk_element
FEATURE [App::DocumentObjectGroupPython] G4_Bk  # scripted group (container) (typed FeaturePython)
  Dunit = g/cm3
  Dvalue = 14
  Group = -> [Bk_element001]
  conduct = 2
  density = 1
  expand = 3
  formula = Bk
  name = G4_Bk
  specific = 4
FEATURE [App::DocumentObjectGroupPython] Cf_element001  label="Cf_element : 1"  # scripted group (container) (typed FeaturePython)
  n = 1
  ref = Cf_element
FEATURE [App::DocumentObjectGroupPython] G4_Cf  # scripted group (container) (typed FeaturePython)
  Dunit = g/cm3
  Dvalue = 10
  Group = -> [Cf_element001]
  conduct = 2
  density = 1
  expand = 3
  formula = Cf
  name = G4_Cf
  specific = 4
FEATURE [App::DocumentObjectGroupPython] Element  # scripted group (container) (typed FeaturePython)
  Group = -> [G4_H,G4_He,G4_Li,G4_Be,G4_B,G4_C,G4_N,G4_O,G4_F,G4_Ne,G4_Na,G4_Mg,G4_Al,G4_Si,G4_P,G4_S,G4_Cl,G4_Ar,G4_K,G4_Ca,G4_Sc,G4_Ti,G4_V,G4_Cr,G4_Mn,G4_Fe,G4_Co,G4_Ni,G4_Cu,G4_Zn,G4_Ga,G4_Ge,G4_As,G4_Se,G4_Br,G4_Kr,G4_Rb,G4_Sr,G4_Y,G4_Zr,G4_Nb,G4_Mo,G4_Tc,G4_Ru,G4_Rh,G4_Pd,G4_Ag,G4_Cd,G4_In,G4_Sn,G4_Sb,G4_Te,G4_I,G4_Xe,G4_Cs,G4_Ba,G4_La,G4_Ce,G4_Pr,G4_Nd,G4_Pm,G4_Sm,G4_Eu,G4_Gd,G4_Tb,G4_Dy,G4_Ho,G4_Er,+30 more]
FEATURE [App::DocumentObjectGroupPython] H_element114  label="H_element : 063"  # scripted group (container) (typed FeaturePython)
  n = 2
  ref = H_element
FEATURE [App::DocumentObjectGroupPython] G4_lH2  # scripted group (container) (typed FeaturePython)
  Dunit = g/cm3
  Dvalue = 0.0708
  Group = -> [H_element114]
  conduct = 2
  density = 1
  expand = 3
  formula = G4_lH2
  name = G4_lH2
  specific = 4
FEATURE [App::DocumentObjectGroupPython] N_element049  label="N_element : 022"  # scripted group (container) (typed FeaturePython)
  n = 2
  ref = N_element
FEATURE [App::DocumentObjectGroupPython] G4_lN2  # scripted group (container) (typed FeaturePython)
  Dunit = g/cm3
  Dvalue = 0.807
  Group = -> [N_element049]
  conduct = 2
  density = 1
  expand = 3
  formula = G4_lN2
  name = G4_lN2
  specific = 4
FEATURE [App::DocumentObjectGroupPython] O_element106  label="O_element : 060"  # scripted group (container) (typed FeaturePython)
  n = 2
  ref = O_element
FEATURE [App::DocumentObjectGroupPython] G4_lO2  # scripted group (container) (typed FeaturePython)
  Dunit = g/cm3
  Dvalue = 1.141
  Group = -> [O_element106]
  conduct = 2
  density = 1
  expand = 3
  formula = G4_lO2
  name = G4_lO2
  specific = 4
FEATURE [App::DocumentObjectGroupPython] Ar  label="Ar : 1"  # scripted group (container) (typed FeaturePython)
  n = 1
  ref = Ar
FEATURE [App::DocumentObjectGroupPython] G4_lAr  # scripted group (container) (typed FeaturePython)
  Dunit = g/cm3
  Dvalue = 1.396
  Group = -> [Ar]
  conduct = 2
  density = 1
  expand = 3
  formula = G4_lAr
  name = G4_lAr
  specific = 4
FEATURE [App::DocumentObjectGroupPython] Br  label="Br : 1"  # scripted group (container) (typed FeaturePython)
  n = 1
  ref = Br
FEATURE [App::DocumentObjectGroupPython] G4_lBr  # scripted group (container) (typed FeaturePython)
  Dunit = g/cm3
  Dvalue = 3.1028
  Group = -> [Br]
  conduct = 2
  density = 1
  expand = 3
  formula = G4_lBr
  name = G4_lBr
  specific = 4
FEATURE [App::DocumentObjectGroupPython] Kr  label="Kr : 1"  # scripted group (container) (typed FeaturePython)
  n = 1
  ref = Kr
FEATURE [App::DocumentObjectGroupPython] G4_lKr  # scripted group (container) (typed FeaturePython)
  Dunit = g/cm3
  Dvalue = 2.418
  Group = -> [Kr]
  conduct = 2
  density = 1
  expand = 3
  formula = G4_lKr
  name = G4_lKr
  specific = 4
FEATURE [App::DocumentObjectGroupPython] Xe  label="Xe : 1"  # scripted group (container) (typed FeaturePython)
  n = 1
  ref = Xe
FEATURE [App::DocumentObjectGroupPython] G4_lXe  # scripted group (container) (typed FeaturePython)
  Dunit = g/cm3
  Dvalue = 2.953
  Group = -> [Xe]
  conduct = 2
  density = 1
  expand = 3
  formula = G4_lXe
  name = G4_lXe
  specific = 4
FEATURE [App::DocumentObjectGroupPython] O_element107  label="O_element : 061"  # scripted group (container) (typed FeaturePython)
  n = 4
  ref = O_element
FEATURE [App::DocumentObjectGroupPython] Pb_element004  label="Pb_element : 002"  # scripted group (container) (typed FeaturePython)
  n = 1
  ref = Pb_element
FEATURE [App::DocumentObjectGroupPython] W_element005  label="W_element : 005"  # scripted group (container) (typed FeaturePython)
  n = 1
  ref = W_element
FEATURE [App::DocumentObjectGroupPython] G4_PbWO4  # scripted group (container) (typed FeaturePython)
  Dunit = g/cm3
  Dvalue = 8.28
  Group = -> [O_element107,Pb_element004,W_element005]
  conduct = 2
  density = 1
  expand = 3
  formula = G4_PbWO4
  name = G4_PbWO4
  specific = 4
FEATURE [App::DocumentObjectGroupPython] alactic  label="alactic : 1"  # scripted group (container) (typed FeaturePython)
  n = 1
  ref = alactic
FEATURE [App::DocumentObjectGroupPython] G4_Galactic  # scripted group (container) (typed FeaturePython)
  Dunit = g/cm3
  Dvalue = 0
  Group = -> [alactic]
  conduct = 2
  density = 1
  expand = 3
  formula = G4_Galactic
  name = G4_Galactic
  specific = 4
FEATURE [App::DocumentObjectGroupPython] RAPHITE_POROUS  label="RAPHITE_POROUS : 1"  # scripted group (container) (typed FeaturePython)
  n = 1
  ref = RAPHITE_POROUS
FEATURE [App::DocumentObjectGroupPython] G4_GRAPHITE_POROUS  # scripted group (container) (typed FeaturePython)
  Dunit = g/cm3
  Dvalue = 1.7
  Group = -> [RAPHITE_POROUS]
  conduct = 2
  density = 1
  expand = 3
  formula = G4_GRAPHITE_POROUS
  name = G4_GRAPHITE_POROUS
  specific = 4
FEATURE [App::DocumentObjectGroupPython] H_element115  label="H_element : 0.150"  # scripted group (container) (typed FeaturePython)
  n = 0.080538
FEATURE [App::DocumentObjectGroupPython] C_element125  label="C_element : 0.600"  # scripted group (container) (typed FeaturePython)
  n = 0.599848
FEATURE [App::DocumentObjectGroupPython] O_element108  label="O_element : 0.320"  # scripted group (container) (typed FeaturePython)
  n = 0.319614
FEATURE [App::DocumentObjectGroupPython] G4_LUCITE  # scripted group (container) (typed FeaturePython)
  Dunit = g/cm3
  Dvalue = 1.19
  Group = -> [H_element115,C_element125,O_element108]
  conduct = 2
  density = 1
  expand = 3
  formula = G4_LUCITE
  name = G4_LUCITE
  specific = 4
FEATURE [App::DocumentObjectGroupPython] Cu_element002  label="Cu_element : 62"  # scripted group (container) (typed FeaturePython)
  n = 62
  ref = Cu_element
FEATURE [App::DocumentObjectGroupPython] Zn_element002  label="Zn_element : 35"  # scripted group (container) (typed FeaturePython)
  n = 35
  ref = Zn_element
FEATURE [App::DocumentObjectGroupPython] Pb_element005  label="Pb_element : 3"  # scripted group (container) (typed FeaturePython)
  n = 3
  ref = Pb_element
FEATURE [App::DocumentObjectGroupPython] G4_BRASS  # scripted group (container) (typed FeaturePython)
  Dunit = g/cm3
  Dvalue = 8.52
  Group = -> [Cu_element002,Zn_element002,Pb_element005]
  conduct = 2
  density = 1
  expand = 3
  formula = G4_BRASS
  name = G4_BRASS
  specific = 4
FEATURE [App::DocumentObjectGroupPython] Cu_element003  label="Cu_element : 89"  # scripted group (container) (typed FeaturePython)
  n = 89
  ref = Cu_element
FEATURE [App::DocumentObjectGroupPython] Zn_element003  label="Zn_element : 9"  # scripted group (container) (typed FeaturePython)
  n = 9
  ref = Zn_element
FEATURE [App::DocumentObjectGroupPython] Pb_element006  label="Pb_element : 2"  # scripted group (container) (typed FeaturePython)
  n = 2
  ref = Pb_element
FEATURE [App::DocumentObjectGroupPython] G4_BRONZE  # scripted group (container) (typed FeaturePython)
  Dunit = g/cm3
  Dvalue = 8.82
  Group = -> [Cu_element003,Zn_element003,Pb_element006]
  conduct = 2
  density = 1
  expand = 3
  formula = G4_BRONZE
  name = G4_BRONZE
  specific = 4
FEATURE [App::DocumentObjectGroupPython] Fe_element008  label="Fe_element : 74"  # scripted group (container) (typed FeaturePython)
  n = 74
  ref = Fe_element
FEATURE [App::DocumentObjectGroupPython] Cr_element002  label="Cr_element : 18"  # scripted group (container) (typed FeaturePython)
  n = 18
  ref = Cr_element
FEATURE [App::DocumentObjectGroupPython] Ni_element002  label="Ni_element : 8"  # scripted group (container) (typed FeaturePython)
  n = 8
  ref = Ni_element
FEATURE [App::DocumentObjectGroupPython] G4_STAINLESS_STEEL  label="G4_STAINLESS-STEEL"  # scripted group (container) (typed FeaturePython)
  Dunit = g/cm3
  Dvalue = 8
  Group = -> [Fe_element008,Cr_element002,Ni_element002]
  conduct = 2
  density = 1
  expand = 3
  formula = G4_STAINLESS-STEEL
  name = G4_STAINLESS-STEEL
  specific = 4
FEATURE [App::DocumentObjectGroupPython] H_element116  label="H_element : 064"  # scripted group (container) (typed FeaturePython)
  n = 18
  ref = H_element
FEATURE [App::DocumentObjectGroupPython] C_element126  label="C_element : 071"  # scripted group (container) (typed FeaturePython)
  n = 12
  ref = C_element
FEATURE [App::DocumentObjectGroupPython] O_element109  label="O_element : 062"  # scripted group (container) (typed FeaturePython)
  n = 7
  ref = O_element
FEATURE [App::DocumentObjectGroupPython] G4_CR39  # scripted group (container) (typed FeaturePython)
  Dunit = g/cm3
  Dvalue = 1.32
  Group = -> [H_element116,C_element126,O_element109]
  conduct = 2
  density = 1
  expand = 3
  formula = G4_CR39
  name = G4_CR39
  specific = 4
FEATURE [App::DocumentObjectGroupPython] H_element117  label="H_element : 38"  # scripted group (container) (typed FeaturePython)
  n = 38
  ref = H_element
FEATURE [App::DocumentObjectGroupPython] C_element127  label="C_element : 072"  # scripted group (container) (typed FeaturePython)
  n = 18
  ref = C_element
FEATURE [App::DocumentObjectGroupPython] O_element110  label="O_element : 063"  # scripted group (container) (typed FeaturePython)
  n = 1
  ref = O_element
FEATURE [App::DocumentObjectGroupPython] G4_OCTADECANOL  # scripted group (container) (typed FeaturePython)
  Dunit = g/cm3
  Dvalue = 0.812
  Group = -> [H_element117,C_element127,O_element110]
  conduct = 2
  density = 1
  expand = 3
  formula = G4_OCTADECANOL
  name = G4_OCTADECANOL
  specific = 4
FEATURE [App::DocumentObjectGroupPython] HEP  # scripted group (container) (typed FeaturePython)
  Group = -> [G4_lH2,G4_lN2,G4_lO2,G4_lAr,G4_lBr,G4_lKr,G4_lXe,G4_PbWO4,G4_Galactic,G4_GRAPHITE_POROUS,G4_LUCITE,G4_BRASS,G4_BRONZE,G4_STAINLESS_STEEL,G4_CR39,G4_OCTADECANOL]
FEATURE [App::DocumentObjectGroupPython] C_element128  label="C_element : 073"  # scripted group (container) (typed FeaturePython)
  n = 14
  ref = C_element
FEATURE [App::DocumentObjectGroupPython] H_element118  label="H_element : 065"  # scripted group (container) (typed FeaturePython)
  n = 10
  ref = H_element
FEATURE [App::DocumentObjectGroupPython] O_element111  label="O_element : 064"  # scripted group (container) (typed FeaturePython)
  n = 2
  ref = O_element
FEATURE [App::DocumentObjectGroupPython] N_element050  label="N_element : 023"  # scripted group (container) (typed FeaturePython)
  n = 2
  ref = N_element
FEATURE [App::DocumentObjectGroupPython] G4_KEVLAR  # scripted group (container) (typed FeaturePython)
  Dunit = g/cm3
  Dvalue = 1.44
  Group = -> [C_element128,H_element118,O_element111,N_element050]
  conduct = 2
  density = 1
  expand = 3
  formula = G4_KEVLAR
  name = G4_KEVLAR
  specific = 4
FEATURE [App::DocumentObjectGroupPython] C_element129  label="C_element : 074"  # scripted group (container) (typed FeaturePython)
  n = 10
  ref = C_element
FEATURE [App::DocumentObjectGroupPython] H_element119  label="H_element : 066"  # scripted group (container) (typed FeaturePython)
  n = 8
  ref = H_element
FEATURE [App::DocumentObjectGroupPython] O_element112  label="O_element : 065"  # scripted group (container) (typed FeaturePython)
  n = 4
  ref = O_element
FEATURE [App::DocumentObjectGroupPython] G4_DACRON  # scripted group (container) (typed FeaturePython)
  Dunit = g/cm3
  Dvalue = 1.4
  Group = -> [C_element129,H_element119,O_element112]
  conduct = 2
  density = 1
  expand = 3
  formula = G4_DACRON
  name = G4_DACRON
  specific = 4
FEATURE [App::DocumentObjectGroupPython] C_element130  label="C_element : 075"  # scripted group (container) (typed FeaturePython)
  n = 4
  ref = C_element
FEATURE [App::DocumentObjectGroupPython] H_element120  label="H_element : 067"  # scripted group (container) (typed FeaturePython)
  n = 5
  ref = H_element
FEATURE [App::DocumentObjectGroupPython] Cl_element030  label="Cl_element : 016"  # scripted group (container) (typed FeaturePython)
  n = 1
  ref = Cl_element
FEATURE [App::DocumentObjectGroupPython] G4_NEOPRENE  # scripted group (container) (typed FeaturePython)
  Dunit = g/cm3
  Dvalue = 1.23
  Group = -> [C_element130,H_element120,Cl_element030]
  conduct = 2
  density = 1
  expand = 3
  formula = G4_NEOPRENE
  name = G4_NEOPRENE
  specific = 4
FEATURE [App::DocumentObjectGroupPython] Space  # scripted group (container) (typed FeaturePython)
  Group = -> [G4_KEVLAR,G4_DACRON,G4_NEOPRENE]
FEATURE [App::DocumentObjectGroupPython] H_element121  label="H_element : 068"  # scripted group (container) (typed FeaturePython)
  n = 5
  ref = H_element
FEATURE [App::DocumentObjectGroupPython] C_element131  label="C_element : 076"  # scripted group (container) (typed FeaturePython)
  n = 4
  ref = C_element
FEATURE [App::DocumentObjectGroupPython] N_element051  label="N_element : 3"  # scripted group (container) (typed FeaturePython)
  n = 3
  ref = N_element
FEATURE [App::DocumentObjectGroupPython] O_element113  label="O_element : 066"  # scripted group (container) (typed FeaturePython)
  n = 1
  ref = O_element
FEATURE [App::DocumentObjectGroupPython] G4_CYTOSINE  # scripted group (container) (typed FeaturePython)
  Dunit = g/cm3
  Dvalue = 1.55
  Group = -> [H_element121,C_element131,N_element051,O_element113]
  conduct = 2
  density = 1
  expand = 3
  formula = G4_CYTOSINE
  name = G4_CYTOSINE
  specific = 4
FEATURE [App::DocumentObjectGroupPython] H_element122  label="H_element : 069"  # scripted group (container) (typed FeaturePython)
  n = 6
  ref = H_element
FEATURE [App::DocumentObjectGroupPython] C_element132  label="C_element : 077"  # scripted group (container) (typed FeaturePython)
  n = 5
  ref = C_element
FEATURE [App::DocumentObjectGroupPython] N_element052  label="N_element : 024"  # scripted group (container) (typed FeaturePython)
  n = 2
  ref = N_element
FEATURE [App::DocumentObjectGroupPython] O_element114  label="O_element : 067"  # scripted group (container) (typed FeaturePython)
  n = 2
  ref = O_element
FEATURE [App::DocumentObjectGroupPython] G4_THYMINE  # scripted group (container) (typed FeaturePython)
  Dunit = g/cm3
  Dvalue = 1.23
  Group = -> [H_element122,C_element132,N_element052,O_element114]
  conduct = 2
  density = 1
  expand = 3
  formula = G4_THYMINE
  name = G4_THYMINE
  specific = 4
FEATURE [App::DocumentObjectGroupPython] H_element123  label="H_element : 070"  # scripted group (container) (typed FeaturePython)
  n = 4
  ref = H_element
FEATURE [App::DocumentObjectGroupPython] C_element133  label="C_element : 078"  # scripted group (container) (typed FeaturePython)
  n = 4
  ref = C_element
FEATURE [App::DocumentObjectGroupPython] N_element053  label="N_element : 025"  # scripted group (container) (typed FeaturePython)
  n = 2
  ref = N_element
FEATURE [App::DocumentObjectGroupPython] O_element115  label="O_element : 068"  # scripted group (container) (typed FeaturePython)
  n = 2
  ref = O_element
FEATURE [App::DocumentObjectGroupPython] G4_URACIL  # scripted group (container) (typed FeaturePython)
  Dunit = g/cm3
  Dvalue = 1.32
  Group = -> [H_element123,C_element133,N_element053,O_element115]
  conduct = 2
  density = 1
  expand = 3
  formula = G4_URACIL
  name = G4_URACIL
  specific = 4
FEATURE [App::DocumentObjectGroupPython] H_element124  label="H_element : 071"  # scripted group (container) (typed FeaturePython)
  n = 4
  ref = H_element
FEATURE [App::DocumentObjectGroupPython] C_element134  label="C_element : 079"  # scripted group (container) (typed FeaturePython)
  n = 5
  ref = C_element
FEATURE [App::DocumentObjectGroupPython] N_element054  label="N_element : 026"  # scripted group (container) (typed FeaturePython)
  n = 5
  ref = N_element
FEATURE [App::DocumentObjectGroupPython] G4_DNA_ADENINE  # scripted group (container) (typed FeaturePython)
  Dunit = g/cm3
  Dvalue = 1
  Group = -> [H_element124,C_element134,N_element054]
  conduct = 2
  density = 1
  expand = 3
  formula = G4_DNA_ADENINE
  name = G4_DNA_ADENINE
  specific = 4
FEATURE [App::DocumentObjectGroupPython] H_element125  label="H_element : 072"  # scripted group (container) (typed FeaturePython)
  n = 4
  ref = H_element
FEATURE [App::DocumentObjectGroupPython] C_element135  label="C_element : 080"  # scripted group (container) (typed FeaturePython)
  n = 5
  ref = C_element
FEATURE [App::DocumentObjectGroupPython] N_element055  label="N_element : 027"  # scripted group (container) (typed FeaturePython)
  n = 5
  ref = N_element
FEATURE [App::DocumentObjectGroupPython] O_element116  label="O_element : 069"  # scripted group (container) (typed FeaturePython)
  n = 1
  ref = O_element
FEATURE [App::DocumentObjectGroupPython] G4_DNA_GUANINE  # scripted group (container) (typed FeaturePython)
  Dunit = g/cm3
  Dvalue = 1
  Group = -> [H_element125,C_element135,N_element055,O_element116]
  conduct = 2
  density = 1
  expand = 3
  formula = G4_DNA_GUANINE
  name = G4_DNA_GUANINE
  specific = 4
FEATURE [App::DocumentObjectGroupPython] H_element126  label="H_element : 073"  # scripted group (container) (typed FeaturePython)
  n = 4
  ref = H_element
FEATURE [App::DocumentObjectGroupPython] C_element136  label="C_element : 081"  # scripted group (container) (typed FeaturePython)
  n = 4
  ref = C_element
FEATURE [App::DocumentObjectGroupPython] N_element056  label="N_element : 028"  # scripted group (container) (typed FeaturePython)
  n = 3
  ref = N_element
FEATURE [App::DocumentObjectGroupPython] O_element117  label="O_element : 070"  # scripted group (container) (typed FeaturePython)
  n = 1
  ref = O_element
FEATURE [App::DocumentObjectGroupPython] G4_DNA_CYTOSINE  # scripted group (container) (typed FeaturePython)
  Dunit = g/cm3
  Dvalue = 1
  Group = -> [H_element126,C_element136,N_element056,O_element117]
  conduct = 2
  density = 1
  expand = 3
  formula = G4_DNA_CYTOSINE
  name = G4_DNA_CYTOSINE
  specific = 4
FEATURE [App::DocumentObjectGroupPython] H_element127  label="H_element : 074"  # scripted group (container) (typed FeaturePython)
  n = 5
  ref = H_element
FEATURE [App::DocumentObjectGroupPython] C_element137  label="C_element : 082"  # scripted group (container) (typed FeaturePython)
  n = 5
  ref = C_element
FEATURE [App::DocumentObjectGroupPython] N_element057  label="N_element : 029"  # scripted group (container) (typed FeaturePython)
  n = 2
  ref = N_element
FEATURE [App::DocumentObjectGroupPython] O_element118  label="O_element : 071"  # scripted group (container) (typed FeaturePython)
  n = 2
  ref = O_element
FEATURE [App::DocumentObjectGroupPython] G4_DNA_THYMINE  # scripted group (container) (typed FeaturePython)
  Dunit = g/cm3
  Dvalue = 1
  Group = -> [H_element127,C_element137,N_element057,O_element118]
  conduct = 2
  density = 1
  expand = 3
  formula = G4_DNA_THYMINE
  name = G4_DNA_THYMINE
  specific = 4
FEATURE [App::DocumentObjectGroupPython] H_element128  label="H_element : 075"  # scripted group (container) (typed FeaturePython)
  n = 3
  ref = H_element
FEATURE [App::DocumentObjectGroupPython] C_element138  label="C_element : 083"  # scripted group (container) (typed FeaturePython)
  n = 4
  ref = C_element
FEATURE [App::DocumentObjectGroupPython] N_element058  label="N_element : 030"  # scripted group (container) (typed FeaturePython)
  n = 2
  ref = N_element
FEATURE [App::DocumentObjectGroupPython] O_element119  label="O_element : 072"  # scripted group (container) (typed FeaturePython)
  n = 2
  ref = O_element
FEATURE [App::DocumentObjectGroupPython] G4_DNA_URACIL  # scripted group (container) (typed FeaturePython)
  Dunit = g/cm3
  Dvalue = 1
  Group = -> [H_element128,C_element138,N_element058,O_element119]
  conduct = 2
  density = 1
  expand = 3
  formula = G4_DNA_URACIL
  name = G4_DNA_URACIL
  specific = 4
FEATURE [App::DocumentObjectGroupPython] H_element129  label="H_element : 076"  # scripted group (container) (typed FeaturePython)
  n = 10
  ref = H_element
FEATURE [App::DocumentObjectGroupPython] C_element139  label="C_element : 084"  # scripted group (container) (typed FeaturePython)
  n = 10
  ref = C_element
FEATURE [App::DocumentObjectGroupPython] N_element059  label="N_element : 031"  # scripted group (container) (typed FeaturePython)
  n = 5
  ref = N_element
FEATURE [App::DocumentObjectGroupPython] O_element120  label="O_element : 073"  # scripted group (container) (typed FeaturePython)
  n = 4
  ref = O_element
FEATURE [App::DocumentObjectGroupPython] G4_DNA_ADENOSINE  # scripted group (container) (typed FeaturePython)
  Dunit = g/cm3
  Dvalue = 1
  Group = -> [H_element129,C_element139,N_element059,O_element120]
  conduct = 2
  density = 1
  expand = 3
  formula = G4_DNA_ADENOSINE
  name = G4_DNA_ADENOSINE
  specific = 4
FEATURE [App::DocumentObjectGroupPython] H_element130  label="H_element : 077"  # scripted group (container) (typed FeaturePython)
  n = 10
  ref = H_element
FEATURE [App::DocumentObjectGroupPython] C_element140  label="C_element : 085"  # scripted group (container) (typed FeaturePython)
  n = 10
  ref = C_element
FEATURE [App::DocumentObjectGroupPython] N_element060  label="N_element : 032"  # scripted group (container) (typed FeaturePython)
  n = 5
  ref = N_element
FEATURE [App::DocumentObjectGroupPython] O_element121  label="O_element : 074"  # scripted group (container) (typed FeaturePython)
  n = 5
  ref = O_element
FEATURE [App::DocumentObjectGroupPython] G4_DNA_GUANOSINE  # scripted group (container) (typed FeaturePython)
  Dunit = g/cm3
  Dvalue = 1
  Group = -> [H_element130,C_element140,N_element060,O_element121]
  conduct = 2
  density = 1
  expand = 3
  formula = G4_DNA_GUANOSINE
  name = G4_DNA_GUANOSINE
  specific = 4
FEATURE [App::DocumentObjectGroupPython] H_element131  label="H_element : 078"  # scripted group (container) (typed FeaturePython)
  n = 10
  ref = H_element
FEATURE [App::DocumentObjectGroupPython] C_element141  label="C_element : 086"  # scripted group (container) (typed FeaturePython)
  n = 9
  ref = C_element
FEATURE [App::DocumentObjectGroupPython] N_element061  label="N_element : 033"  # scripted group (container) (typed FeaturePython)
  n = 3
  ref = N_element
FEATURE [App::DocumentObjectGroupPython] O_element122  label="O_element : 075"  # scripted group (container) (typed FeaturePython)
  n = 5
  ref = O_element
FEATURE [App::DocumentObjectGroupPython] G4_DNA_CYTIDINE  # scripted group (container) (typed FeaturePython)
  Dunit = g/cm3
  Dvalue = 1
  Group = -> [H_element131,C_element141,N_element061,O_element122]
  conduct = 2
  density = 1
  expand = 3
  formula = G4_DNA_CYTIDINE
  name = G4_DNA_CYTIDINE
  specific = 4
FEATURE [App::DocumentObjectGroupPython] H_element132  label="H_element : 079"  # scripted group (container) (typed FeaturePython)
  n = 9
  ref = H_element
FEATURE [App::DocumentObjectGroupPython] C_element142  label="C_element : 087"  # scripted group (container) (typed FeaturePython)
  n = 9
  ref = C_element
FEATURE [App::DocumentObjectGroupPython] N_element062  label="N_element : 034"  # scripted group (container) (typed FeaturePython)
  n = 2
  ref = N_element
FEATURE [App::DocumentObjectGroupPython] O_element123  label="O_element : 076"  # scripted group (container) (typed FeaturePython)
  n = 6
  ref = O_element
FEATURE [App::DocumentObjectGroupPython] G4_DNA_URIDINE  # scripted group (container) (typed FeaturePython)
  Dunit = g/cm3
  Dvalue = 1
  Group = -> [H_element132,C_element142,N_element062,O_element123]
  conduct = 2
  density = 1
  expand = 3
  formula = G4_DNA_URIDINE
  name = G4_DNA_URIDINE
  specific = 4
FEATURE [App::DocumentObjectGroupPython] H_element133  label="H_element : 080"  # scripted group (container) (typed FeaturePython)
  n = 11
  ref = H_element
FEATURE [App::DocumentObjectGroupPython] C_element143  label="C_element : 088"  # scripted group (container) (typed FeaturePython)
  n = 10
  ref = C_element
FEATURE [App::DocumentObjectGroupPython] N_element063  label="N_element : 035"  # scripted group (container) (typed FeaturePython)
  n = 2
  ref = N_element
FEATURE [App::DocumentObjectGroupPython] O_element124  label="O_element : 077"  # scripted group (container) (typed FeaturePython)
  n = 6
  ref = O_element
FEATURE [App::DocumentObjectGroupPython] G4_DNA_METHYLURIDINE  # scripted group (container) (typed FeaturePython)
  Dunit = g/cm3
  Dvalue = 1
  Group = -> [H_element133,C_element143,N_element063,O_element124]
  conduct = 2
  density = 1
  expand = 3
  formula = G4_DNA_METHYLURIDINE
  name = G4_DNA_METHYLURIDINE
  specific = 4
FEATURE [App::DocumentObjectGroupPython] P_element014  label="P_element : 003"  # scripted group (container) (typed FeaturePython)
  n = 1
  ref = P_element
FEATURE [App::DocumentObjectGroupPython] O_element125  label="O_element : 078"  # scripted group (container) (typed FeaturePython)
  n = 3
  ref = O_element
FEATURE [App::DocumentObjectGroupPython] G4_DNA_MONOPHOSPHATE  # scripted group (container) (typed FeaturePython)
  Dunit = g/cm3
  Dvalue = 1
  Group = -> [P_element014,O_element125]
  conduct = 2
  density = 1
  expand = 3
  formula = G4_DNA_MONOPHOSPHATE
  name = G4_DNA_MONOPHOSPHATE
  specific = 4
FEATURE [App::DocumentObjectGroupPython] H_element134  label="H_element : 081"  # scripted group (container) (typed FeaturePython)
  n = 10
  ref = H_element
FEATURE [App::DocumentObjectGroupPython] C_element144  label="C_element : 089"  # scripted group (container) (typed FeaturePython)
  n = 10
  ref = C_element
FEATURE [App::DocumentObjectGroupPython] N_element064  label="N_element : 036"  # scripted group (container) (typed FeaturePython)
  n = 5
  ref = N_element
FEATURE [App::DocumentObjectGroupPython] O_element126  label="O_element : 079"  # scripted group (container) (typed FeaturePython)
  n = 7
  ref = O_element
FEATURE [App::DocumentObjectGroupPython] P_element015  label="P_element : 004"  # scripted group (container) (typed FeaturePython)
  n = 1
  ref = P_element
FEATURE [App::DocumentObjectGroupPython] G4_DNA_A  # scripted group (container) (typed FeaturePython)
  Dunit = g/cm3
  Dvalue = 1
  Group = -> [H_element134,C_element144,N_element064,O_element126,P_element015]
  conduct = 2
  density = 1
  expand = 3
  formula = G4_DNA_A
  name = G4_DNA_A
  specific = 4
FEATURE [App::DocumentObjectGroupPython] H_element135  label="H_element : 082"  # scripted group (container) (typed FeaturePython)
  n = 10
  ref = H_element
FEATURE [App::DocumentObjectGroupPython] C_element145  label="C_element : 090"  # scripted group (container) (typed FeaturePython)
  n = 10
  ref = C_element
FEATURE [App::DocumentObjectGroupPython] N_element065  label="N_element : 037"  # scripted group (container) (typed FeaturePython)
  n = 5
  ref = N_element
FEATURE [App::DocumentObjectGroupPython] O_element127  label="O_element : 8"  # scripted group (container) (typed FeaturePython)
  n = 8
  ref = O_element
FEATURE [App::DocumentObjectGroupPython] P_element016  label="P_element : 005"  # scripted group (container) (typed FeaturePython)
  n = 1
  ref = P_element
FEATURE [App::DocumentObjectGroupPython] G4_DNA_G  # scripted group (container) (typed FeaturePython)
  Dunit = g/cm3
  Dvalue = 1
  Group = -> [H_element135,C_element145,N_element065,O_element127,P_element016]
  conduct = 2
  density = 1
  expand = 3
  formula = G4_DNA_G
  name = G4_DNA_G
  specific = 4
FEATURE [App::DocumentObjectGroupPython] H_element136  label="H_element : 083"  # scripted group (container) (typed FeaturePython)
  n = 10
  ref = H_element
FEATURE [App::DocumentObjectGroupPython] C_element146  label="C_element : 091"  # scripted group (container) (typed FeaturePython)
  n = 9
  ref = C_element
FEATURE [App::DocumentObjectGroupPython] N_element066  label="N_element : 038"  # scripted group (container) (typed FeaturePython)
  n = 3
  ref = N_element
FEATURE [App::DocumentObjectGroupPython] O_element128  label="O_element : 080"  # scripted group (container) (typed FeaturePython)
  n = 8
  ref = O_element
FEATURE [App::DocumentObjectGroupPython] P_element017  label="P_element : 006"  # scripted group (container) (typed FeaturePython)
  n = 1
  ref = P_element
FEATURE [App::DocumentObjectGroupPython] G4_DNA_C  # scripted group (container) (typed FeaturePython)
  Dunit = g/cm3
  Dvalue = 1
  Group = -> [H_element136,C_element146,N_element066,O_element128,P_element017]
  conduct = 2
  density = 1
  expand = 3
  formula = G4_DNA_C
  name = G4_DNA_C
  specific = 4
FEATURE [App::DocumentObjectGroupPython] H_element137  label="H_element : 084"  # scripted group (container) (typed FeaturePython)
  n = 9
  ref = H_element
FEATURE [App::DocumentObjectGroupPython] C_element147  label="C_element : 092"  # scripted group (container) (typed FeaturePython)
  n = 9
  ref = C_element
FEATURE [App::DocumentObjectGroupPython] N_element067  label="N_element : 039"  # scripted group (container) (typed FeaturePython)
  n = 2
  ref = N_element
FEATURE [App::DocumentObjectGroupPython] O_element129  label="O_element : 9"  # scripted group (container) (typed FeaturePython)
  n = 9
  ref = O_element
FEATURE [App::DocumentObjectGroupPython] P_element018  label="P_element : 007"  # scripted group (container) (typed FeaturePython)
  n = 1
  ref = P_element
FEATURE [App::DocumentObjectGroupPython] G4_DNA_U  # scripted group (container) (typed FeaturePython)
  Dunit = g/cm3
  Dvalue = 1
  Group = -> [H_element137,C_element147,N_element067,O_element129,P_element018]
  conduct = 2
  density = 1
  expand = 3
  formula = G4_DNA_U
  name = G4_DNA_U
  specific = 4
FEATURE [App::DocumentObjectGroupPython] H_element138  label="H_element : 085"  # scripted group (container) (typed FeaturePython)
  n = 11
  ref = H_element
FEATURE [App::DocumentObjectGroupPython] C_element148  label="C_element : 093"  # scripted group (container) (typed FeaturePython)
  n = 10
  ref = C_element
FEATURE [App::DocumentObjectGroupPython] N_element068  label="N_element : 040"  # scripted group (container) (typed FeaturePython)
  n = 2
  ref = N_element
FEATURE [App::DocumentObjectGroupPython] O_element130  label="O_element : 081"  # scripted group (container) (typed FeaturePython)
  n = 9
  ref = O_element
FEATURE [App::DocumentObjectGroupPython] P_element019  label="P_element : 008"  # scripted group (container) (typed FeaturePython)
  n = 1
  ref = P_element
FEATURE [App::DocumentObjectGroupPython] G4_DNA_MU  # scripted group (container) (typed FeaturePython)
  Dunit = g/cm3
  Dvalue = 1
  Group = -> [H_element138,C_element148,N_element068,O_element130,P_element019]
  conduct = 2
  density = 1
  expand = 3
  formula = G4_DNA_MU
  name = G4_DNA_MU
  specific = 4
FEATURE [App::DocumentObjectGroupPython] BioChemical  # scripted group (container) (typed FeaturePython)
  Group = -> [G4_CYTOSINE,G4_THYMINE,G4_URACIL,G4_DNA_ADENINE,G4_DNA_GUANINE,G4_DNA_CYTOSINE,G4_DNA_THYMINE,G4_DNA_URACIL,G4_DNA_ADENOSINE,G4_DNA_GUANOSINE,G4_DNA_CYTIDINE,G4_DNA_URIDINE,G4_DNA_METHYLURIDINE,G4_DNA_MONOPHOSPHATE,G4_DNA_A,G4_DNA_G,G4_DNA_C,G4_DNA_U,G4_DNA_MU]
FEATURE [App::DocumentObjectGroupPython] G4Materials  # scripted group (container) (typed FeaturePython)
  Group = -> [NIST,Element,HEP,Space,BioChemical]
  version = 1
FEATURE [App::DocumentObjectGroupPython] Geant4  # scripted group (container) (typed FeaturePython)
  Group = -> [G4Isotopes,G4Elements,G4Materials]
FEATURE [App::DocumentObjectGroupPython] Materials  # scripted group (container) (typed FeaturePython)
  Group = -> [Geant4]
FEATURE [Part::FeaturePython] GDMLBox_WorldBox  # WARN: FeaturePython — macro-defined, semantics opaque (R4)
  lunit = 2
  material = 5
  x = 100
  y = 100
  z = 100
FEATURE [Part::Part2DObjectPython] Circle  # Draft 2D object (typed FeaturePython)
  Area = 5026.55
  FirstAngle = 0
  LastAngle = 0
  MakeFace = true
  Placement = pos=(-6.62621,-53.6724,-16.5942) rot=(-0.574466,0.143177,0.805909;3.50816rad)
  Radius = 40
FEATURE [Part::FeaturePython] GDMLBox_Box  # WARN: FeaturePython — macro-defined, semantics opaque (R4)
  lunit = 2
  material = 0
  x = 10
  y = 10
  z = 10
FEATURE [App::Part] LV_Box001
  Group = -> [GDMLBox_Box,Circle]
  Origin = -> Origin002
FEATURE [App::Part] worldVOL
  Group = -> [GDMLBox_WorldBox,LV_Box001]
  Origin = -> Origin
FEATURE [Part::FeaturePython] PathArray  # WARN: FeaturePython — macro-defined, semantics opaque (R4)
  Align = false
  AlignMode = 0
  Base = -> GDMLBox_Box
  Count = 4
  ExtraTranslation = (0,0,0)
  ForceVertical = false
  PathObject = -> Circle
  TangentVector = (1,0,0)
  VerticalVector = (0,0,1)
